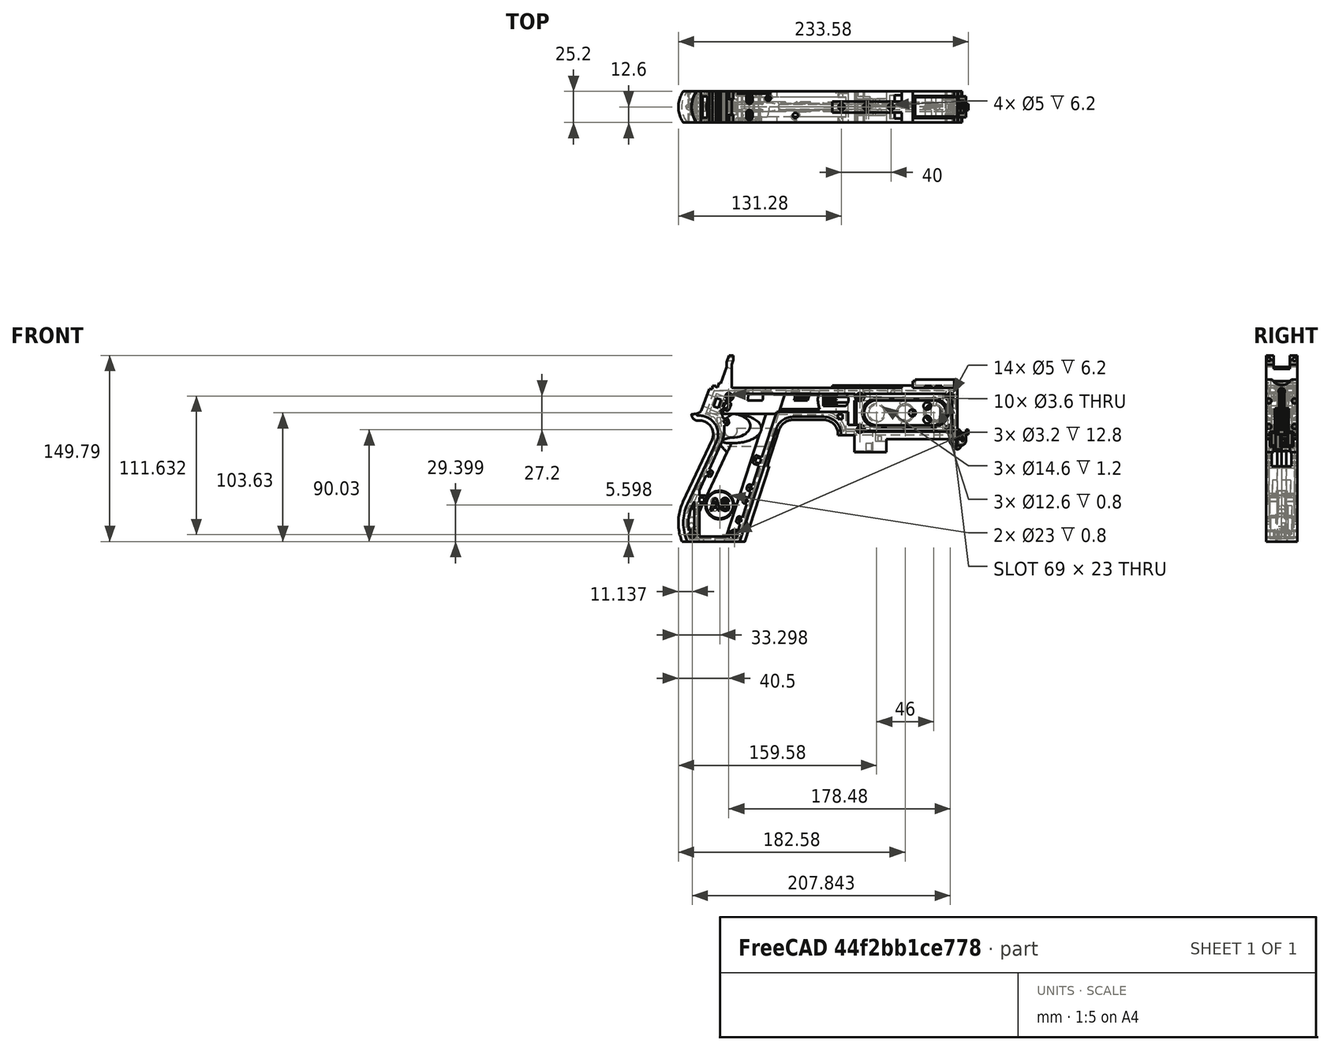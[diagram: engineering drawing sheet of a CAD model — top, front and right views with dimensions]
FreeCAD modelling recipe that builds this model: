
FCSTD DOCUMENT  (FreeCAD 1.0R39319 (Git))
Label: PICON-OF_ver_49
License: All rights reserved
LicenseURL: https://en.wikipedia.org/wiki/All_rights_reserved
objects: Sketcher::SketchObject×121, Part::Extrusion×62, Part::Cut×48, PartDesign::Pad×29, PartDesign::Pocket×20, PartDesign::Chamfer×15, PartDesign::Body×10, PartDesign::Fillet×6, Part::MultiFuse×4, Part::Part2DObjectPython×4, PartDesign::SubtractivePipe×4, PartDesign::SubtractiveLoft×4, PartDesign::Plane×2, PartDesign::SubShapeBinder×2, Part::Sweep×1, PartDesign::ShapeBinder×1, Mesh::Feature×1
note: 610 computed .brp shape members not serialized (recipe doc carries the construction recipe); baked Part::Feature solids carry a one-line shape summary decoded from their .brp

FEATURE [Sketcher::SketchObject] Sketch  label="corpo principale"
  ArcFitTolerance = 1e-06
  AttacherType = Attacher::AttachEngine3D
  AttachmentSupport = -> [XZ_Plane]
  FullyConstrained = true
  MakeInternals = false
  MapMode = 5
  Placement = pos=(0,0,0) rot=(1,0,0;1.5708rad)
  sketch-geometry (65):
    g0: LineSegment StartX=0 StartY=0 StartZ=0 EndX=-57.2 EndY=0 EndZ=0
    g1: LineSegment StartX=-57.2 StartY=0 StartZ=0 EndX=-57.2 EndY=-10.4 EndZ=0
    g2: LineSegment StartX=-57.2 StartY=-10.4 StartZ=0 EndX=-82.8 EndY=-10.4 EndZ=0
    g3: LineSegment StartX=-82.8 StartY=-10.4 StartZ=0 EndX=-82.8 EndY=3.2 EndZ=0
    g4: LineSegment StartX=-82.8 StartY=3.2 StartZ=0 EndX=-93.6 EndY=3.2 EndZ=0
    g5: LineSegment StartX=-93.6 StartY=3.2 StartZ=0 EndX=-93.6 EndY=4 EndZ=0
    g6: LineSegment StartX=-107.6 StartY=18 StartZ=0 EndX=-132.428 EndY=18 EndZ=0
    g7: LineSegment StartX=-145.743 StartY=8.32624 StartZ=0 EndX=-175.232 EndY=-82.4316 EndZ=0
    g8: LineSegment StartX=-175.232 StartY=-82.4316 StartZ=0 EndX=-217.232 EndY=-82.4316 EndZ=0
    g9: LineSegment StartX=-217.232 StartY=-52.1862 StartZ=0 EndX=-193.988 EndY=-2.33927 EndZ=0
    g10: LineSegment StartX=-206.196 StartY=23.0857 StartZ=0 EndX=-199.861 EndY=40.4914 EndZ=0
    g11: LineSegment StartX=-199.861 StartY=40.4914 StartZ=0 EndX=-197.061 EndY=40.4914 EndZ=0
    g12: LineSegment StartX=-197.061 StartY=40.4914 StartZ=0 EndX=-197.061 EndY=42.8914 EndZ=0
    g13: LineSegment StartX=-197.061 StartY=42.8914 StartZ=0 EndX=-194.261 EndY=42.8914 EndZ=0
    g14: LineSegment StartX=-194.261 StartY=42.8914 StartZ=0 EndX=-194.535 EndY=42.1397 EndZ=0
    g15: LineSegment StartX=-194.535 StartY=42.1397 StartZ=0 EndX=-193.031 EndY=41.5924 EndZ=0
    g16: LineSegment StartX=-193.031 StartY=41.5924 StartZ=0 EndX=-191.663 EndY=45.3512 EndZ=0
    g17: LineSegment StartX=-191.663 StartY=45.3512 StartZ=0 EndX=-190.536 EndY=44.9408 EndZ=0
    g18: LineSegment StartX=-190.536 StartY=44.9408 StartZ=0 EndX=-185.747 EndY=58.0965 EndZ=0
    g19: LineSegment StartX=-185.747 StartY=58.0965 StartZ=0 EndX=-185.747 EndY=62.0965 EndZ=0
    g20: LineSegment StartX=-185.747 StartY=62.0965 StartZ=0 EndX=-183.832 EndY=67.3588 EndZ=0
    g21: LineSegment StartX=-183.832 StartY=67.3588 StartZ=0 EndX=-180.232 EndY=67.3588 EndZ=0
    g22: LineSegment StartX=-180.232 StartY=67.3588 StartZ=0 EndX=-180.232 EndY=63.7588 EndZ=0
    g23: LineSegment StartX=-180.232 StartY=63.7588 StartZ=0 EndX=-181.6 EndY=60 EndZ=0
    g24: LineSegment StartX=-181.6 StartY=60 StartZ=0 EndX=-181.6 EndY=41.2 EndZ=0
    g25: LineSegment StartX=-181.6 StartY=41.2 StartZ=0 EndX=-100.8 EndY=41.2 EndZ=0
    g26: LineSegment StartX=-36 StartY=43.2 StartZ=0 EndX=-36 EndY=41.2 EndZ=0
    g27: LineSegment StartX=0 StartY=48 StartZ=0 EndX=0 EndY=0 EndZ=0
    g28: LineSegment StartX=-209.901 StartY=19.85 StartZ=0 EndX=-209.901 EndY=20.1 EndZ=0
    g29: LineSegment StartX=-208.001 StartY=22 StartZ=0 EndX=-207.747 EndY=22 EndZ=0
    g30: LineSegment StartX=-207.583 StartY=19 StartZ=0 EndX=-209.051 EndY=19 EndZ=0
    g31: ArcOfCircle CenterX=-208.001 CenterY=20.1 CenterZ=0 NormalX=0 NormalY=0 NormalZ=1 AngleXU=0 Radius=1.9 StartAngle=1.5708 EndAngle=3.14159
    g32: GeomPoint [constr] X=-209.901 Y=22 Z=0
    g33: ArcOfCircle CenterX=-209.051 CenterY=19.85 CenterZ=0 NormalX=0 NormalY=0 NormalZ=1 AngleXU=0 Radius=0.85 StartAngle=3.14159 EndAngle=4.71239
    g34: GeomPoint [constr] X=-209.901 Y=19 Z=0
    g35: ArcOfCircle CenterX=-207.747 CenterY=23.65 CenterZ=0 NormalX=0 NormalY=0 NormalZ=1 AngleXU=0 Radius=1.65 StartAngle=4.71239 EndAngle=5.93412
    g36: GeomPoint [constr] X=-206.591 Y=22 Z=0
    g37: LineSegment StartX=-4 StartY=6 StartZ=0 EndX=-4 EndY=36.4 EndZ=0
    g38: LineSegment StartX=-4 StartY=36.4 StartZ=0 EndX=-185.2 EndY=36.4 EndZ=0
    g39: LineSegment StartX=-185.2 StartY=36.4 StartZ=0 EndX=-190.441 EndY=22 EndZ=0
    g40: LineSegment StartX=-214.575 StartY=-78.4316 StartZ=0 EndX=-178.142 EndY=-78.4316 EndZ=0
    g41: LineSegment StartX=-178.142 StartY=-78.4316 StartZ=0 EndX=-145.51 EndY=22 EndZ=0
    g42: LineSegment StartX=-145.51 StartY=22 StartZ=0 EndX=-87.91 EndY=22 EndZ=0
    g43: LineSegment StartX=-87.91 StartY=22 StartZ=0 EndX=-87.91 EndY=11.6 EndZ=0
    g44: LineSegment StartX=-87.91 StartY=11.6 StartZ=0 EndX=-80.11 EndY=11.6 EndZ=0
    g45: LineSegment StartX=-80.11 StartY=11.6 StartZ=0 EndX=-80.11 EndY=6 EndZ=0
    g46: LineSegment StartX=-80.11 StartY=6 StartZ=0 EndX=-4 EndY=6 EndZ=0
    g47: LineSegment StartX=-190.363 StartY=-4.02975 StartZ=0 EndX=-213.607 EndY=-53.8767 EndZ=0
    g48: ArcOfCircle CenterX=-132.428 CenterY=4 CenterZ=0 NormalX=0 NormalY=0 NormalZ=1 AngleXU=0 Radius=14 StartAngle=1.5708 EndAngle=2.82743
    g49: GeomPoint [constr] X=-142.6 Y=18 Z=0
    g50: ArcOfCircle CenterX=-107.6 CenterY=4 CenterZ=0 NormalX=0 NormalY=0 NormalZ=1 AngleXU=0 Radius=14 StartAngle=0 EndAngle=1.5708
    g51: GeomPoint [constr] X=-93.6 Y=18 Z=0
    g52: ArcOfCircle CenterX=-184.801 CenterY=-67.3089 CenterZ=0 NormalX=0 NormalY=0 NormalZ=1 AngleXU=0 Radius=35.7833 StartAngle=2.70526 EndAngle=3.57792
    g53: ArcOfCircle CenterX=-207.583 CenterY=4 CenterZ=0 NormalX=0 NormalY=0 NormalZ=1 AngleXU=0 Radius=15 StartAngle=5.84685 EndAngle=7.85398
    g54: LineSegment [constr] StartX=-213.607 StartY=-53.8767 StartZ=0 EndX=-217.232 EndY=-52.1862 EndZ=0
    g55: ArcOfCircle CenterX=-184.801 CenterY=-67.3089 CenterZ=0 NormalX=0 NormalY=0 NormalZ=1 AngleXU=0 Radius=31.7833 StartAngle=2.70526 EndAngle=3.49911
    g56: ArcOfCircle CenterX=-218.095 CenterY=8.90192 CenterZ=0 NormalX=0 NormalY=0 NormalZ=1 AngleXU=0 Radius=30.5989 StartAngle=5.84685 EndAngle=6.72553
    g57: LineSegment StartX=-44.6 StartY=43.2 StartZ=0 EndX=-36 EndY=43.2 EndZ=0
    g58: LineSegment StartX=-100.8 StartY=41.2 StartZ=0 EndX=-44.6 EndY=41.2 EndZ=0
    g59: LineSegment StartX=-44.6 StartY=41.2 StartZ=0 EndX=-44.6 EndY=43.2 EndZ=0
    g60: LineSegment StartX=-2.4 StartY=48 StartZ=0 EndX=0 EndY=48 EndZ=0
    g61: LineSegment StartX=-36 StartY=41.2 StartZ=0 EndX=-2.4 EndY=41.2 EndZ=0
    g62: LineSegment StartX=-2.4 StartY=41.2 StartZ=0 EndX=-2.4 EndY=48 EndZ=0
    g63: LineSegment [constr] StartX=-181.6 StartY=36.4 StartZ=0 EndX=-152.209 EndY=36.4 EndZ=0
    g64: LineSegment [constr] StartX=-181.6 StartY=36.4 StartZ=0 EndX=-130.41 EndY=36.4 EndZ=0
  constraints (183):
    c: Coincident(g-1,g0)
    c: PointOnObject(g0,g-1)
    c: Coincident(g0,g1)
    c: Vertical(g1)
    c: Coincident(g1,g2)
    c: Horizontal(g2)
    c: Coincident(g2,g3)
    c: Vertical(g3)
    c: Coincident(g3,g4)
    c: Coincident(g4,g5)
    c: Vertical(g5)
    c: Horizontal(g6)
    c: Coincident(g7,g8)
    c: Horizontal(g8)
    c: Coincident(g10,g11)
    c: Horizontal(g11)
    c: Coincident(g11,g12)
    c: Vertical(g12)
    c: Coincident(g12,g13)
    c: Horizontal(g13)
    c: Coincident(g13,g14)
    c: Coincident(g14,g15)
    c: Coincident(g15,g16)
    c: Coincident(g16,g17)
    c: Coincident(g17,g18)
    c: Coincident(g18,g19)
    c: Vertical(g19)
    c: Coincident(g19,g20)
    c: Coincident(g20,g21)
    c: Horizontal(g21)
    c: Coincident(g21,g22)
    c: Vertical(g22)
    c: Coincident(g22,g23)
    c: Coincident(g23,g24)
    c: Vertical(g24)
    c: Coincident(g24,g25)
    c: Horizontal(g25)
    c: Coincident(g57,g26)
    c: Vertical(g26)
    c: Coincident(g26,g61)
    c: PointOnObject(g60,g-2)
    c: Coincident(g60,g27)
    c: Coincident(g27,g0)
    c: DistanceY(g27,g27) = 48
    c: DistanceY(g1,g1) = 10.4
    c: DistanceX(g0,g0) = 57.2
    c: DistanceX(g2,g2) = 25.6
    c: Horizontal(g4)
    c: DistanceY(g3,g3) = 13.6
    c: DistanceX(g4,g4) = 10.8
    c: DistanceY(g5,g51) = 14.8
    c: DistanceX(g49,g51) = 49
    c: Distance(g7,g49) = 105.6
    c: DistanceX(g61,g60) = 36
    c: DistanceX(g25,g25) = 80.8
    c: DistanceY(g24,g24) = 18.8
    c: DistanceY(g22,g22) = 3.6
    c: Distance(g23) = 4
    c: Angle(g-1,g23) = 1.22173
    c: DistanceX(g21,g21) = 3.6
    c: Distance(g20) = 5.6
    c: Angle(g-1,g20) = 1.22173
    c: DistanceY(g19,g19) = 4
    c: Distance(g18) = 14
    c: Angle(g-1,g18) = 1.22173
    c: Distance(g17) = 1.2
    c: Distance(g16) = 4
    c: Angle(g16) = 1.22173
    c: Perpendicular(g18,g17)
    c: Distance(g15) = 1.6
    c: Perpendicular(g16,g15)
    c: Distance(g14) = 0.8
    c: DistanceX(g13,g13) = 2.8
    c: Perpendicular(g15,g14)
    c: DistanceY(g12,g12) = 2.4
    c: DistanceX(g11,g11) = 2.8
    c: Distance(g9) = 55
    c: Angle(g9,g-1) = 2.00713
    c: Horizontal(g29)
    c: Vertical(g28)
    c: Horizontal(g30)
    c: PointOnObject(g32,g29)
    c: PointOnObject(g32,g28)
    c: Tangent(g29,g31) = 1.5708
    c: Tangent(g28,g31) = 1.5708
    c: PointOnObject(g34,g28)
    c: PointOnObject(g34,g30)
    c: Tangent(g28,g33) = 1.5708
    c: Tangent(g30,g33) = 1.5708
    c: PointOnObject(g36,g29)
    c: PointOnObject(g36,g10)
    c: Tangent(g29,g35) = -1.5708
    c: Tangent(g10,g35) = -1.5708
    c: Angle(g-1,g10) = 1.22173
    c: Radius(g35) = 1.65
    c: Vertical(g37)
    c: Coincident(g37,g38)
    c: Horizontal(g38)
    c: Coincident(g38,g39)
    c: Horizontal(g40)
    c: Coincident(g40,g41)
    c: Coincident(g41,g42)
    c: Horizontal(g42)
    c: Coincident(g42,g43)
    c: Vertical(g43)
    c: Coincident(g43,g44)
    c: Horizontal(g44)
    c: Coincident(g44,g45)
    c: Vertical(g45)
    c: Coincident(g45,g46)
    c: Coincident(g46,g37)
    c: Horizontal(g46)
    c: DistanceY(g0,g37) = 6
    c: DistanceX(g37,g0) = 4
    c: DistanceY(g37,g25) = 4.8
    c: DistanceX(g38,g38) = 181.2
    c: DistanceX(g42,g42) = 57.6
    c: DistanceY(g49,g41) = 4
    c: DistanceX(g41,g49) = 2.91
    c: DistanceY(g43,g43) = 10.4
    c: DistanceX(g44,g44) = 7.8
    c: DistanceY(g7,g40) = 4
    c: Distance(g47) = 55
    c: Angle(g-1,g39) = 1.22173
    c: PointOnObject(g49,g7)
    c: PointOnObject(g49,g6)
    c: Tangent(g7,g48) = -1.5708
    c: Tangent(g6,g48) = -1.5708
    c: PointOnObject(g51,g5)
    c: PointOnObject(g51,g6)
    c: Tangent(g5,g50) = -1.5708
    c: Tangent(g6,g50) = -1.5708
    c: Radius(g50) = 14
    c: Radius(g48) = 14
    c: DistanceX(g8,g8) = 42
    c: Angle(g7,g-1) = 1.88496
    c: Parallel(g41,g7)
    c: Parallel(g47,g9)
    c: Coincident(g52,g8)
    c: Tangent(g52,g9) = 1.5708
    c: DistanceX(g9,g8) = 0
    c: Tangent(g53,g9) = -1.5708
    c: Tangent(g53,g30) = -1.5708
    c: Diameter(g53) = 30
    c: DistanceY(g53,g0) = -4
    c: Coincident(g54,g47)
    c: Distance(g54) = 4
    c: Coincident(g54,g9)
    c: Coincident(g55,g40)
    c: Tangent(g55,g47) = -1.5708
    c: Coincident(g52,g55)
    c: Coincident(g56,g39)
    c: Tangent(g56,g47) = 1.5708
    c: Horizontal(g57)
    c: DistanceX(g57,g57) = 8.6
    c: Coincident(g58,g25)
    c: Horizontal(g58)
    c: Coincident(g59,g58)
    c: Vertical(g59)
    c: DistanceY(g58,g57) = 2
    c: DistanceX(g58,g58) = 56.2
    c: Coincident(g59,g57)
    c: DistanceY(g41,g36) = 0
    c: DistanceY(g36,g39) = 0
    c: DistanceY(g28,g28) = 0.25
    c: DistanceX(g30,g36) = 2.46
    c: DistanceX(g28,g29) = 1.9
    c: Coincident(g62,g60)
    c: Horizontal(g60)
    c: DistanceX(g62,g27) = 2.4
    c: Coincident(g61,g62)
    c: DistanceY(g26,g26) = 2
    c: Vertical(g62)
    c: DistanceY(g61,g60) = 6.8
    c: Horizontal(g61)
    c: Distance(g63) = 29.391
    c: PointOnObject(g63,g38)
    c: PointOnObject(g63,g38)
    c: Distance(g64) = 51.19
    c: PointOnObject(g64,g38)
    c: PointOnObject(g64,g38)
    c: DistanceX(g24,g63) = 0
    c: DistanceX(g24,g64) = 0
FEATURE [Part::Extrusion] Extrude  label="Extrude corpo principale"
  Base = -> Sketch
  Dir = (0,-1,2e-16)
  DirMode = 2
  FaceMakerClass = Part::FaceMakerBullseye
  FaceMakerMode = 3
  LengthFwd = 25.2
  LengthRev = 12.6
  Solid = true
  Symmetric = true
FEATURE [Sketcher::SketchObject] Sketch002  label="scavo grilletto"
  ArcFitTolerance = 1e-06
  AttachmentSupport = -> [XZ_Plane]
  ExternalGeometry = -> [Sketch]
  FullyConstrained = true
  MakeInternals = false
  MapMode = 5
  Placement = pos=(0,0,0) rot=(1,0,0;1.5708rad)
  sketch-geometry (4):
    g0: LineSegment StartX=-89.51 StartY=22 StartZ=0 EndX=-152.71 EndY=22 EndZ=0
    g1: LineSegment StartX=-152.71 StartY=22 StartZ=0 EndX=-167.006 EndY=-22 EndZ=0
    g2: LineSegment StartX=-167.006 StartY=-22 StartZ=0 EndX=-89.51 EndY=-22 EndZ=0
    g3: LineSegment StartX=-89.51 StartY=-22 StartZ=0 EndX=-89.51 EndY=22 EndZ=0
  constraints (12):
    c: Horizontal(g0)
    c: Coincident(g0,g1)
    c: Coincident(g1,g2)
    c: Horizontal(g2)
    c: Coincident(g2,g3)
    c: Coincident(g3,g0)
    c: Vertical(g3)
    c: Angle(g1,g0) = 1.88496
    c: DistanceY(g3,g3) = 44
    c: DistanceX(g0,g0) = 63.2
    c: DistanceX(g0,g-3) = 1.6
    c: DistanceY(g-3,g0) = 0
FEATURE [Sketcher::SketchObject] Sketch004  label="traiettoria arrotondamento impugnatura anteriore"
  ArcFitTolerance = 1e-06
  AttachmentSupport = -> [XZ_Plane]
  ExternalGeometry = -> [Sketch]
  FullyConstrained = true
  MakeInternals = false
  MapMode = 5
  Placement = pos=(0,0,0) rot=(1,0,0;1.5708rad)
  sketch-geometry (13):
    g0: LineSegment StartX=-175.232 StartY=-82.4316 StartZ=0 EndX=-145.743 EndY=8.32624 EndZ=0
    g1: LineSegment StartX=-93.6 StartY=3.2 StartZ=0 EndX=-93.6 EndY=4 EndZ=0
    g2: LineSegment StartX=-132.428 StartY=18 StartZ=0 EndX=-107.6 EndY=18 EndZ=0
    g3: ArcOfCircle CenterX=-132.428 CenterY=4 CenterZ=0 NormalX=0 NormalY=0 NormalZ=1 AngleXU=0 Radius=14 StartAngle=1.5708 EndAngle=2.82743
    g4: ArcOfCircle CenterX=-107.6 CenterY=4 CenterZ=0 NormalX=0 NormalY=0 NormalZ=1 AngleXU=0 Radius=14 StartAngle=0 EndAngle=1.5708
    g5: LineSegment StartX=-175.232 StartY=-82.4316 StartZ=0 EndX=-217.232 EndY=-82.4316 EndZ=0
    g6: LineSegment StartX=-217.232 StartY=-52.1862 StartZ=0 EndX=-193.988 EndY=-2.33927 EndZ=0
    g7: LineSegment StartX=-209.051 StartY=19 StartZ=0 EndX=-207.583 EndY=19 EndZ=0
    g8: LineSegment StartX=-209.901 StartY=20.1 StartZ=0 EndX=-209.901 EndY=19.85 EndZ=0
    g9: ArcOfCircle CenterX=-184.801 CenterY=-67.3089 CenterZ=0 NormalX=0 NormalY=0 NormalZ=1 AngleXU=0 Radius=35.7833 StartAngle=2.70526 EndAngle=3.57792
    g10: ArcOfCircle CenterX=-207.583 CenterY=4 CenterZ=0 NormalX=0 NormalY=0 NormalZ=1 AngleXU=0 Radius=15 StartAngle=5.84685 EndAngle=7.85398
    g11: ArcOfCircle CenterX=-209.051 CenterY=19.85 CenterZ=0 NormalX=0 NormalY=0 NormalZ=1 AngleXU=0 Radius=0.85 StartAngle=3.14159 EndAngle=4.71239
    g12: ArcOfCircle CenterX=-208.001 CenterY=20.1 CenterZ=0 NormalX=0 NormalY=0 NormalZ=1 AngleXU=0 Radius=1.9 StartAngle=1.5708 EndAngle=3.14159
  constraints (26):
    c: Coincident(g0,g-3)
    c: Coincident(g0,g-6)
    c: Coincident(g1,g-8)
    c: Coincident(g1,g-7)
    c: Coincident(g2,g-5)
    c: Coincident(g2,g-4)
    c: Coincident(g3,g2)
    c: Tangent(g3,g0) = 1.5708
    c: Coincident(g4,g1)
    c: Tangent(g4,g2) = 1.5708
    c: Coincident(g5,g0)
    c: Coincident(g5,g-9)
    c: Coincident(g6,g-12)
    c: Coincident(g6,g-11)
    c: Coincident(g7,g-15)
    c: Coincident(g7,g-14)
    c: Coincident(g8,g-16)
    c: Coincident(g8,g-17)
    c: Tangent(g9,g6) = 1.5708
    c: Coincident(g9,g5)
    c: Coincident(g10,g7)
    c: Tangent(g10,g6) = -1.5708
    c: Tangent(g11,g7) = -1.5708
    c: Coincident(g11,g8)
    c: Tangent(g12,g8) = -1.5708
    c: Coincident(g12,g-17)
FEATURE [PartDesign::Plane] DatumPlane  label="Piano per disegno arrotondamento impugnatura"
  AttachmentSupport = -> [Sketch]
  Length = 73.6581
  MapMode = 7
  Placement = pos=(-145.743,1.8e-15,8.32624) rot=(0.154555,0.154555,0.97582;1.59527rad)
  ResizeMode = 0
  Width = 303.511
FEATURE [Sketcher::SketchObject] Sketch005  label="forma arrotondamento impugnatura anteriore"
  ArcFitTolerance = 1e-06
  AttachmentSupport = -> [DatumPlane]
  FullyConstrained = true
  MakeInternals = false
  MapMode = 5
  Placement = pos=(-145.743,1.8e-15,8.32624) rot=(0.154555,0.154555,0.97582;1.59527rad)
  sketch-geometry (5):
    g0: GeomPoint [constr] X=0 Y=-4 Z=0
    g1: GeomPoint [constr] X=-12.6 Y=7.1e-15 Z=0
    g2: GeomPoint [constr] X=12.6 Y=4.97e-14 Z=0
    g3: LineSegment StartX=-12.6 StartY=7.1e-15 StartZ=0 EndX=12.6 EndY=4.97e-14 EndZ=0
    g4: ArcOfCircle CenterX=-3.88e-14 CenterY=17.845 CenterZ=0 NormalX=0 NormalY=0 NormalZ=1 AngleXU=0 Radius=21.845 StartAngle=4.09759 EndAngle=5.32718
  constraints (11):
    c: DistanceY(g0,g-1) = 4
    c: DistanceX(g-1,g0) = 0
    c: DistanceX(g1,g-1) = 12.6
    c: DistanceX(g-1,g2) = 12.6
    c: DistanceY(g-1,g2) = 0
    c: DistanceY(g-1,g1) = 0
    c: Coincident(g3,g1)
    c: Coincident(g3,g2)
    c: Coincident(g4,g1)
    c: Coincident(g4,g2)
    c: PointOnObject(g0,g4)
FEATURE [Part::Sweep] Sweep  label="Sweep impugnatura"
  Frenet = true
  Sections = -> [Sketch005]
  Solid = true
  Spine = -> Sketch [Edge32,Edge33,Edge34,Edge35,Edge36,Edge37,Edge38,Edge39,Edge40,Edge41,Edge42,Edge43,Edge44]
  Transition = 1
FEATURE [Sketcher::SketchObject] Sketch008  label="buchi e pulizie varie"
  ArcFitTolerance = 1e-06
  AttachmentSupport = -> [XZ_Plane]
  ExternalGeometry = -> [Sketch]
  FullyConstrained = true
  MakeInternals = false
  MapMode = 5
  Placement = pos=(0,0,0) rot=(1,0,0;1.5708rad)
  sketch-geometry (26):
    g0: LineSegment StartX=-96.278 StartY=20.155 StartZ=0 EndX=-92.278 EndY=20.155 EndZ=0
    g1: LineSegment StartX=-92.278 StartY=20.155 StartZ=0 EndX=-92.278 EndY=16.155 EndZ=0
    g2: LineSegment StartX=-92.278 StartY=16.155 StartZ=0 EndX=-96.278 EndY=16.155 EndZ=0
    g3: LineSegment StartX=-96.278 StartY=16.155 StartZ=0 EndX=-96.278 EndY=20.155 EndZ=0
    g4: LineSegment StartX=-222.232 StartY=-82.4316 StartZ=0 EndX=-170.232 EndY=-82.4316 EndZ=0
    g5: LineSegment StartX=-170.232 StartY=-82.4316 StartZ=0 EndX=-170.232 EndY=-86.4316 EndZ=0
    g6: LineSegment StartX=-170.232 StartY=-86.4316 StartZ=0 EndX=-222.232 EndY=-86.4316 EndZ=0
    g7: LineSegment StartX=-222.232 StartY=-86.4316 StartZ=0 EndX=-222.232 EndY=-82.4316 EndZ=0
    g8: LineSegment StartX=-213.901 StartY=20.1 StartZ=0 EndX=-213.901 EndY=26 EndZ=0
    g9: LineSegment StartX=-213.901 StartY=26 StartZ=0 EndX=-206.196 EndY=26 EndZ=0
    g10: LineSegment StartX=-17.4 StartY=42.8 StartZ=0 EndX=-12.4 EndY=42.8 EndZ=0
    g11: LineSegment StartX=-12.4 StartY=42.8 StartZ=0 EndX=-12.4 EndY=41.2 EndZ=0
    g12: LineSegment StartX=-12.4 StartY=41.2 StartZ=0 EndX=-17.4 EndY=41.2 EndZ=0
    g13: LineSegment StartX=-17.4 StartY=41.2 StartZ=0 EndX=-17.4 EndY=42.8 EndZ=0
    g14: LineSegment StartX=-25.9 StartY=42.8 StartZ=0 EndX=-20.9 EndY=42.8 EndZ=0
    g15: LineSegment StartX=-20.9 StartY=42.8 StartZ=0 EndX=-20.9 EndY=41.2 EndZ=0
    g16: LineSegment StartX=-20.9 StartY=41.2 StartZ=0 EndX=-25.9 EndY=41.2 EndZ=0
    g17: LineSegment StartX=-25.9 StartY=41.2 StartZ=0 EndX=-25.9 EndY=42.8 EndZ=0
    g18: GeomPoint [constr] X=-206.196 Y=23.0857 Z=0
    g19: GeomPoint [constr] X=-213.901 Y=20.1 Z=0
    g20: BSplineCurve PolesCount=4 KnotsCount=2 Degree=3 IsPeriodic=0
    g21-g24: Circle [constr] x4 (B-spline internal-alignment scaffolding for g20; pole/knot coordinates omitted)
    g25: LineSegment StartX=-206.196 StartY=26 StartZ=0 EndX=-206.196 EndY=23.0857 EndZ=0
  constraints (73):
    c: Horizontal(g0)
    c: Coincident(g1,g0)
    c: Vertical(g1)
    c: Coincident(g2,g1)
    c: Horizontal(g2)
    c: Coincident(g3,g2)
    c: Coincident(g3,g0)
    c: Vertical(g3)
    c: DistanceX(g0,g-4) = 4.368
    c: DistanceY(g0,g-4) = 1.845
    c: DistanceY(g1,g1) = 4
    c: DistanceX(g2,g2) = 4
    c: Horizontal(g4)
    c: Coincident(g5,g4)
    c: Vertical(g5)
    c: Coincident(g6,g5)
    c: Horizontal(g6)
    c: Coincident(g7,g6)
    c: Coincident(g7,g4)
    c: Vertical(g7)
    c: DistanceY(g7,g7) = 4
    c: DistanceX(g4,g-5) = 5
    c: DistanceX(g-5,g4) = 5
    c: DistanceY(g4,g-5) = 0
    c: Coincident(g9,g8)
    c: Parallel(g9,g-6)
    c: DistanceX(g8,g-8) = 4
    c: Horizontal(g10)
    c: Coincident(g11,g10)
    c: Vertical(g11)
    c: Coincident(g12,g11)
    c: Horizontal(g12)
    c: Coincident(g13,g12)
    c: Coincident(g13,g10)
    c: Vertical(g13)
    c: Horizontal(g14)
    c: Coincident(g15,g14)
    c: Vertical(g15)
    c: Coincident(g16,g15)
    c: Horizontal(g16)
    c: Coincident(g17,g16)
    c: Coincident(g17,g14)
    c: Vertical(g17)
    c: DistanceY(g11,g10) = 1.6
    c: DistanceX(g10,g10) = 5
    c: DistanceY(g15,g14) = 1.6
    c: DistanceX(g14,g14) = 5
    c: DistanceX(g15,g12) = 3.5
    c: DistanceX(g11,g-9) = 10
    c: DistanceY(g-9,g11) = 0
    c: DistanceY(g-9,g15) = 0
    c: Perpendicular(g8,g9)
    c: DistanceY(g-7,g9) = 4
    c: DistanceY(g8,g-8) = 0
    c: InternalAlignment(g18,g20)
    c: InternalAlignment(g19,g20)
    c: InternalAlignment(g21,g20)
    c: Weight(g21) = 1
    c: InternalAlignment(g22,g20)
    c: Equal(g22,g21)
    c: InternalAlignment(g23,g20)
    c: Equal(g23,g21)
    c: InternalAlignment(g24,g20)
    c: Equal(g24,g21)
    c: Coincident(g18,g-12)
    c: Coincident(g19,g8)
    c: Coincident(g25,g9)
    c: Coincident(g25,g20)
    c: Vertical(g25)
    c: DistanceY(g20,g23) = 0
    c: DistanceY(g22,g18) = 2.26
    c: DistanceX(g22,g18) = 0.93
    c: DistanceX(g20,g23) = 2.9
FEATURE [Part::Extrusion] Extrude004  label="Extrude Buchi e pulizie varie"
  Base = -> Sketch008
  Dir = (0,-1,2e-16)
  DirMode = 2
  FaceMakerClass = Part::FaceMakerBullseye
  FaceMakerMode = 3
  LengthFwd = 25.2
  LengthRev = 0
  Solid = true
  Symmetric = true
FEATURE [Sketcher::SketchObject] Sketch009  label="rinforzi"
  ArcFitTolerance = 1e-06
  AttachmentSupport = -> [XZ_Plane]
  ExternalGeometry = -> [Sketch]
  FullyConstrained = true
  MakeInternals = false
  MapMode = 5
  Placement = pos=(0,0,0) rot=(1,0,0;1.5708rad)
  sketch-geometry (9):
    g0: LineSegment StartX=-87.91 StartY=22 StartZ=0 EndX=-87.91 EndY=36.4 EndZ=0
    g1: LineSegment StartX=-87.91 StartY=36.4 StartZ=0 EndX=-97.91 EndY=36.4 EndZ=0
    g2: LineSegment StartX=-97.91 StartY=36.4 StartZ=0 EndX=-97.91 EndY=22 EndZ=0
    g3: LineSegment StartX=-97.91 StartY=22 StartZ=0 EndX=-87.91 EndY=22 EndZ=0
    g4: LineSegment StartX=-149.713 StartY=9.06563 StartZ=0 EndX=-154.586 EndY=-5.93437 EndZ=0
    g5: LineSegment StartX=-154.586 StartY=-5.93437 StartZ=0 EndX=-191.863 EndY=-5.93437 EndZ=0
    g6: LineSegment StartX=-191.863 StartY=-5.93437 StartZ=0 EndX=-191.863 EndY=9.06563 EndZ=0
    g7: LineSegment StartX=-191.863 StartY=9.06563 StartZ=0 EndX=-149.713 EndY=9.06563 EndZ=0
    g8: LineSegment [constr] StartX=-145.51 StartY=22 StartZ=0 EndX=-149.713 EndY=9.06563 EndZ=0
  constraints (25):
    c: Vertical(g0)
    c: Coincident(g1,g0)
    c: Horizontal(g1)
    c: Coincident(g2,g1)
    c: Vertical(g2)
    c: Coincident(g3,g2)
    c: Coincident(g3,g0)
    c: Horizontal(g3)
    c: Coincident(g0,g-4)
    c: DistanceX(g3,g3) = 10
    c: DistanceY(g0,g-3) = 0
    c: Coincident(g5,g4)
    c: Horizontal(g5)
    c: Coincident(g6,g5)
    c: Vertical(g6)
    c: Coincident(g7,g6)
    c: Coincident(g7,g4)
    c: Horizontal(g7)
    c: Distance(g8) = 13.6
    c: Parallel(g-6,g8)
    c: Coincident(g-6,g8)
    c: Parallel(g4,g-6)
    c: DistanceY(g4,g4) = 15
    c: Coincident(g4,g8)
    c: DistanceX(g-5,g5) = -1.5
FEATURE [Part::Extrusion] Extrude001  label="Extrude scavo grilletto"
  Base = -> Sketch002
  Dir = (0,-1,2e-16)
  DirMode = 2
  FaceMakerClass = Part::FaceMakerBullseye
  FaceMakerMode = 3
  LengthFwd = 16
  LengthRev = 0
  Solid = true
  Symmetric = true
FEATURE [Part::Extrusion] Extrude005  label="Extrude Rinforzi"
  Base = -> Sketch009
  Dir = (0,-1,2e-16)
  DirMode = 2
  FaceMakerClass = Part::FaceMakerBullseye
  FaceMakerMode = 3
  LengthFwd = 2
  LengthRev = 0
  Placement = pos=(0,12.6,0) rot=(0,0,1;0rad)
  Solid = true
  Symmetric = false
FEATURE [PartDesign::ShapeBinder] CopyCut
  TraceSupport = false
FEATURE [PartDesign::Plane] DatumPlane001
  AttachmentSupport = -> [CopyCut]
  Length = 283.944
  MapMode = 5
  Placement = pos=(0,12.6,0) rot=(0,0.707107,0.707107;3.14159rad)
  ResizeMode = 0
  Width = 188.15
FEATURE [Sketcher::SketchObject] Sketch010  label="buco neopixel"
  ArcFitTolerance = 1e-06
  AttachmentSupport = -> [XZ_Plane]
  ExternalGeometry = -> [Sketch]
  FullyConstrained = true
  MakeInternals = false
  MapMode = 5
  Placement = pos=(0,0,0) rot=(1,0,0;1.5708rad)
  sketch-geometry (5):
    g0: LineSegment [constr] StartX=-199.861 StartY=40.4914 StartZ=0 EndX=-201.368 EndY=36.3521 EndZ=0
    g1: LineSegment StartX=-201.368 StartY=36.3521 StartZ=0 EndX=-204.932 EndY=26.5605 EndZ=0
    g2: LineSegment StartX=-201.368 StartY=36.3521 StartZ=0 EndX=-180.2 EndY=28.6477 EndZ=0
    g3: LineSegment StartX=-180.2 StartY=28.6477 StartZ=0 EndX=-183.764 EndY=18.8561 EndZ=0
    g4: LineSegment StartX=-183.764 StartY=18.8561 StartZ=0 EndX=-204.932 EndY=26.5605 EndZ=0
  constraints (14):
    c: Parallel(g0,g-3)
    c: Distance(g0) = 4.405
    c: Coincident(g0,g-3)
    c: Coincident(g2,g1)
    c: Coincident(g3,g2)
    c: Coincident(g4,g3)
    c: Coincident(g4,g1)
    c: Parallel(g1,g-3)
    c: Distance(g1) = 10.42
    c: Coincident(g1,g0)
    c: Parallel(g2,g4)
    c: Perpendicular(g1,g2)
    c: DistanceX(g-4,g2) = 5
    c: Parallel(g3,g1)
FEATURE [Part::Extrusion] Extrude006  label="Extrude buco neopixel"
  Base = -> Sketch010
  Dir = (0,-1,2e-16)
  DirMode = 2
  FaceMakerClass = Part::FaceMakerBullseye
  FaceMakerMode = 3
  LengthFwd = 17.2
  LengthRev = 0
  Solid = true
  Symmetric = true
FEATURE [Sketcher::SketchObject] Sketch011  label="fermo grilletto"
  ArcFitTolerance = 1e-06
  AttachmentSupport = -> [XZ_Plane]
  ExternalGeometry = -> [Sketch]
  FullyConstrained = true
  MakeInternals = false
  MapMode = 5
  Placement = pos=(0,0,0) rot=(1,0,0;1.5708rad)
  sketch-geometry (18):
    g0: LineSegment [constr] StartX=-145.51 StartY=22 StartZ=0 EndX=-157.347 EndY=-14.4293 EndZ=0
    g1: LineSegment [constr] StartX=-157.347 StartY=-14.4293 StartZ=0 EndX=-157.841 EndY=-15.951 EndZ=0
    g2: LineSegment StartX=-161.151 StartY=-13.1932 StartZ=0 EndX=-155.825 EndY=-14.9237 EndZ=0
    g3: LineSegment StartX=-163.167 StartY=-14.2205 StartZ=0 EndX=-164.403 EndY=-18.0247 EndZ=0
    g4: LineSegment StartX=-163.376 StartY=-20.0408 StartZ=0 EndX=-158.05 EndY=-21.7713 EndZ=0
    g5: LineSegment StartX=-158.05 StartY=-21.7713 StartZ=0 EndX=-155.825 EndY=-14.9237 EndZ=0
    g6: LineSegment StartX=-161.645 StartY=-14.7149 StartZ=0 EndX=-157.841 EndY=-15.951 EndZ=0
    g7: LineSegment StartX=-157.841 StartY=-15.951 StartZ=0 EndX=-159.077 EndY=-19.7552 EndZ=0
    g8: LineSegment StartX=-159.077 StartY=-19.7552 StartZ=0 EndX=-162.881 EndY=-18.5191 EndZ=0
    g9: LineSegment StartX=-162.881 StartY=-18.5191 StartZ=0 EndX=-161.645 EndY=-14.7149 EndZ=0
    g10: LineSegment [constr] StartX=-161.645 StartY=-14.7149 StartZ=0 EndX=-161.151 EndY=-13.1932 EndZ=0
    g11: LineSegment [constr] StartX=-159.077 StartY=-19.7552 StartZ=0 EndX=-157.555 EndY=-20.2496 EndZ=0
    g12: LineSegment [constr] StartX=-159.077 StartY=-19.7552 StartZ=0 EndX=-159.572 EndY=-21.2769 EndZ=0
    g13: LineSegment [constr] StartX=-161.645 StartY=-14.7149 StartZ=0 EndX=-163.167 EndY=-14.2205 EndZ=0
    g14: ArcOfCircle CenterX=-161.645 CenterY=-14.7149 CenterZ=0 NormalX=0 NormalY=0 NormalZ=1 AngleXU=0 Radius=1.6 StartAngle=1.25664 EndAngle=2.82743
    g15: GeomPoint [constr] X=-162.673 Y=-12.6988 Z=0
    g16: ArcOfCircle CenterX=-162.881 CenterY=-18.5191 CenterZ=0 NormalX=0 NormalY=0 NormalZ=1 AngleXU=0 Radius=1.6 StartAngle=2.82743 EndAngle=4.39823
    g17: GeomPoint [constr] X=-164.897 Y=-19.5464 Z=0
  constraints (48):
    c: Parallel(g0,g-3)
    c: Distance(g0) = 38.304
    c: Coincident(g0,g-3)
    c: Parallel(g1,g-3)
    c: Distance(g1) = 1.6
    c: Coincident(g1,g0)
    c: Coincident(g5,g4)
    c: Coincident(g5,g2)
    c: Coincident(g7,g6)
    c: Coincident(g8,g7)
    c: Coincident(g9,g8)
    c: Coincident(g9,g6)
    c: Parallel(g7,g-3)
    c: Parallel(g9,g7)
    c: Perpendicular(g6,g7)
    c: Parallel(g6,g8)
    c: Distance(g6) = 4
    c: Distance(g9) = 4
    c: Parallel(g5,g7)
    c: Parallel(g9,g3)
    c: Parallel(g2,g6)
    c: Parallel(g4,g8)
    c: Parallel(g13,g6)
    c: Parallel(g10,g9)
    c: Parallel(g11,g8)
    c: Parallel(g12,g7)
    c: Distance(g10) = 1.6
    c: Distance(g13) = 1.6
    c: Distance(g12) = 1.6
    c: Distance(g11) = 1.6
    c: Coincident(g10,g6)
    c: Coincident(g13,g6)
    c: Coincident(g12,g7)
    c: Coincident(g11,g7)
    c: Distance(g10,g15) = 1.6
    c: Distance(g15,g13) = 1.6
    c: Distance(g4,g12) = 1.6
    c: Distance(g4,g11) = 1.6
    c: PointOnObject(g15,g2)
    c: Tangent(g3,g14) = -1.5708
    c: Tangent(g2,g14) = 1.5708
    c: PointOnObject(g17,g4)
    c: PointOnObject(g17,g3)
    c: Tangent(g4,g16) = -1.5708
    c: Tangent(g3,g16) = -1.5708
    c: Equal(g16,g14)
    c: Coincident(g16,g8)
    c: Coincident(g6,g1)
FEATURE [Part::Extrusion] Extrude007  label="Extrude fermo grilletto"
  Base = -> Sketch011
  Dir = (0,-1,2e-16)
  DirMode = 2
  FaceMakerClass = Part::FaceMakerBullseye
  FaceMakerMode = 3
  LengthFwd = 25.2
  LengthRev = 0
  Solid = true
  Symmetric = true
FEATURE [Sketcher::SketchObject] Sketch012  label="buco oled"
  ArcFitTolerance = 1e-06
  AttachmentSupport = -> [XZ_Plane]
  ExternalGeometry = -> [Sketch]
  FullyConstrained = true
  MakeInternals = false
  MapMode = 5
  Placement = pos=(0,0,0) rot=(1,0,0;1.5708rad)
  sketch-geometry (4):
    g0: LineSegment StartX=-185.747 StartY=58.0965 StartZ=0 EndX=-180.232 EndY=56.0891 EndZ=0
    g1: LineSegment StartX=-185.747 StartY=58.0965 StartZ=0 EndX=-185.747 EndY=67.3588 EndZ=0
    g2: LineSegment StartX=-185.747 StartY=67.3588 StartZ=0 EndX=-180.232 EndY=67.3588 EndZ=0
    g3: LineSegment StartX=-180.232 StartY=67.3588 StartZ=0 EndX=-180.232 EndY=56.0891 EndZ=0
  constraints (10):
    c: Coincident(g1,g0)
    c: Coincident(g2,g1)
    c: Coincident(g3,g2)
    c: Coincident(g3,g0)
    c: Parallel(g1,g-5)
    c: Perpendicular(g-3,g0)
    c: Parallel(g2,g-6)
    c: Parallel(g3,g-4)
    c: Coincident(g0,g-5)
    c: Coincident(g2,g-6)
FEATURE [Part::Extrusion] Extrude008  label="Extrude buco oled"
  Base = -> Sketch012
  Dir = (0,-1,2e-16)
  DirMode = 2
  FaceMakerClass = Part::FaceMakerBullseye
  FaceMakerMode = 3
  LengthFwd = 12.8
  LengthRev = 0
  Solid = true
  Symmetric = true
FEATURE [Sketcher::SketchObject] Sketch013  label="buco pompa"
  ArcFitTolerance = 1e-06
  AttachmentSupport = -> [XZ_Plane]
  ExternalGeometry = -> [Sketch]
  FullyConstrained = true
  MakeInternals = false
  MapMode = 5
  Placement = pos=(0,0,0) rot=(1,0,0;1.5708rad)
  sketch-geometry (8):
    g0: LineSegment StartX=-82.8 StartY=-10.4 StartZ=0 EndX=-82.8 EndY=-9.6 EndZ=0
    g1: LineSegment StartX=-82.8 StartY=-9.6 StartZ=0 EndX=-67.9 EndY=-9.6 EndZ=0
    g2: LineSegment StartX=-67.9 StartY=-9.6 StartZ=0 EndX=-67.9 EndY=6 EndZ=0
    g3: LineSegment StartX=-67.9 StartY=6 StartZ=0 EndX=-65.9 EndY=6 EndZ=0
    g4: LineSegment StartX=-65.9 StartY=6 StartZ=0 EndX=-65.9 EndY=-1.7 EndZ=0
    g5: LineSegment StartX=-65.9 StartY=-1.7 StartZ=0 EndX=-57.2 EndY=-1.7 EndZ=0
    g6: LineSegment StartX=-57.2 StartY=-1.7 StartZ=0 EndX=-57.2 EndY=-10.4 EndZ=0
    g7: LineSegment StartX=-57.2 StartY=-10.4 StartZ=0 EndX=-82.8 EndY=-10.4 EndZ=0
  constraints (22):
    c: Vertical(g0)
    c: Coincident(g1,g0)
    c: Horizontal(g1)
    c: Coincident(g2,g1)
    c: Vertical(g2)
    c: Coincident(g3,g2)
    c: Horizontal(g3)
    c: Coincident(g4,g3)
    c: Vertical(g4)
    c: Coincident(g5,g4)
    c: Horizontal(g5)
    c: Coincident(g6,g5)
    c: Vertical(g6)
    c: Coincident(g7,g6)
    c: Coincident(g7,g0)
    c: DistanceY(g0,g0) = 0.8
    c: DistanceY(g6,g6) = 8.7
    c: DistanceX(g1,g1) = 14.9
    c: DistanceX(g3,g3) = 2
    c: Coincident(g0,g-4)
    c: DistanceY(g2,g-6) = 0
    c: Coincident(g6,g-5)
FEATURE [Part::Extrusion] Extrude009  label="Extrude buco pompa"
  Base = -> Sketch013
  Dir = (0,-1,2e-16)
  DirMode = 2
  FaceMakerClass = Part::FaceMakerBullseye
  FaceMakerMode = 3
  LengthFwd = 13.2
  LengthRev = 0
  Solid = true
  Symmetric = true
FEATURE [Sketcher::SketchObject] Sketch014  label="buco frontale"
  ArcFitTolerance = 1e-06
  AttachmentSupport = -> [XZ_Plane]
  ExternalGeometry = -> [Sketch]
  FullyConstrained = true
  MakeInternals = false
  MapMode = 5
  Placement = pos=(0,0,0) rot=(1,0,0;1.5708rad)
  sketch-geometry (10):
    g0: LineSegment StartX=0 StartY=0 StartZ=0 EndX=0 EndY=24.671 EndZ=0
    g1: LineSegment StartX=0 StartY=24.671 StartZ=0 EndX=-4 EndY=24.671 EndZ=0
    g2: LineSegment StartX=-4 StartY=24.671 StartZ=0 EndX=-4 EndY=16 EndZ=0
    g3: LineSegment StartX=-4 StartY=16 StartZ=0 EndX=-2.4 EndY=16 EndZ=0
    g4: LineSegment StartX=-2.4 StartY=16 StartZ=0 EndX=-2.4 EndY=10 EndZ=0
    g5: LineSegment StartX=-2.4 StartY=10 StartZ=0 EndX=-12 EndY=10 EndZ=0
    g6: LineSegment StartX=-12 StartY=10 StartZ=0 EndX=-12 EndY=6 EndZ=0
    g7: LineSegment StartX=-12 StartY=6 StartZ=0 EndX=-2.4 EndY=6 EndZ=0
    g8: LineSegment StartX=-2.4 StartY=6 StartZ=0 EndX=-2.4 EndY=0 EndZ=0
    g9: LineSegment StartX=-2.4 StartY=0 StartZ=0 EndX=0 EndY=0 EndZ=0
  constraints (29):
    c: Vertical(g0)
    c: Coincident(g1,g0)
    c: Horizontal(g1)
    c: Coincident(g2,g1)
    c: Vertical(g2)
    c: Coincident(g3,g2)
    c: Horizontal(g3)
    c: Coincident(g4,g3)
    c: Vertical(g4)
    c: Coincident(g5,g4)
    c: Horizontal(g5)
    c: Coincident(g6,g5)
    c: Vertical(g6)
    c: Coincident(g7,g6)
    c: Coincident(g8,g7)
    c: Vertical(g8)
    c: Coincident(g9,g8)
    c: Coincident(g9,g0)
    c: Horizontal(g9)
    c: DistanceY(g0,g0) = 24.671
    c: Horizontal(g7)
    c: DistanceY(g6,g6) = 4
    c: DistanceY(g4,g4) = 6
    c: DistanceX(g9,g9) = 2.4
    c: Coincident(g0,g-1)
    c: DistanceY(g-3,g7) = 0
    c: DistanceX(g8,g4) = 0
    c: DistanceX(g-3,g1) = 0
    c: DistanceX(g6,g-3) = 8
FEATURE [Part::Extrusion] Extrude010  label="Extrude buco frontale"
  Base = -> Sketch014
  Dir = (0,-1,2e-16)
  DirMode = 2
  FaceMakerClass = Part::FaceMakerBullseye
  FaceMakerMode = 3
  LengthFwd = 11.2
  LengthRev = 0
  Solid = true
  Symmetric = true
FEATURE [Sketcher::SketchObject] Sketch015  label="guida rail"
  ArcFitTolerance = 1e-06
  AttachmentSupport = -> [XZ_Plane]
  ExternalGeometry = -> [Sketch]
  FullyConstrained = true
  MakeInternals = false
  MapMode = 5
  Placement = pos=(0,0,0) rot=(1,0,0;1.5708rad)
  sketch-geometry (4):
    g0: LineSegment StartX=-100.8 StartY=43.2 StartZ=0 EndX=-44.6 EndY=43.2 EndZ=0
    g1: LineSegment StartX=-44.6 StartY=43.2 StartZ=0 EndX=-44.6 EndY=41.2 EndZ=0
    g2: LineSegment StartX=-44.6 StartY=41.2 StartZ=0 EndX=-100.8 EndY=41.2 EndZ=0
    g3: LineSegment StartX=-100.8 StartY=41.2 StartZ=0 EndX=-100.8 EndY=43.2 EndZ=0
  constraints (9):
    c: Horizontal(g0)
    c: Coincident(g1,g0)
    c: Coincident(g2,g1)
    c: Coincident(g3,g2)
    c: Coincident(g3,g0)
    c: Vertical(g3)
    c: Coincident(g2,g-3)
    c: Coincident(g1,g-3)
    c: Coincident(g0,g-4)
FEATURE [Part::Extrusion] Extrude011  label="Extrude guida rail"
  Base = -> Sketch015
  Dir = (0,-1,2e-16)
  DirMode = 2
  FaceMakerClass = Part::FaceMakerBullseye
  FaceMakerMode = 3
  LengthFwd = 9
  LengthRev = 0
  Solid = true
  Symmetric = true
FEATURE [Sketcher::SketchObject] Sketch016  label="guide per coperture laterali"
  ArcFitTolerance = 1e-06
  AttachmentSupport = -> [XZ_Plane]
  ExternalGeometry = -> [Sketch]
  FullyConstrained = true
  MakeInternals = false
  MapMode = 5
  Placement = pos=(0,0,0) rot=(1,0,0;1.5708rad)
  sketch-geometry (14):
    g0: Circle CenterX=-5.6 CenterY=7.6 CenterZ=0 NormalX=0 NormalY=0 NormalZ=1 AngleXU=0 Radius=1.6
    g1: Circle CenterX=-5.6 CenterY=7.6 CenterZ=0 NormalX=0 NormalY=0 NormalZ=1 AngleXU=0 Radius=4
    g2: Circle CenterX=-5.6 CenterY=34.8 CenterZ=0 NormalX=0 NormalY=0 NormalZ=1 AngleXU=0 Radius=1.6
    g3: Circle CenterX=-5.6 CenterY=34.8 CenterZ=0 NormalX=0 NormalY=0 NormalZ=1 AngleXU=0 Radius=4
    g4: Circle CenterX=-184.08 CenterY=34.8 CenterZ=0 NormalX=0 NormalY=0 NormalZ=1 AngleXU=0 Radius=1.6
    g5: Circle CenterX=-184.08 CenterY=34.8 CenterZ=0 NormalX=0 NormalY=0 NormalZ=1 AngleXU=0 Radius=4
    g6: Circle CenterX=-179.305 CenterY=-76.8316 CenterZ=0 NormalX=0 NormalY=0 NormalZ=1 AngleXU=0 Radius=1.6
    g7: Circle CenterX=-179.305 CenterY=-76.8316 CenterZ=0 NormalX=0 NormalY=0 NormalZ=1 AngleXU=0 Radius=4
    g8: Circle CenterX=-213.443 CenterY=-76.8316 CenterZ=0 NormalX=0 NormalY=0 NormalZ=1 AngleXU=0 Radius=1.6
    g9: Circle CenterX=-213.443 CenterY=-76.8316 CenterZ=0 NormalX=0 NormalY=0 NormalZ=1 AngleXU=0 Radius=4
    g10: Circle CenterX=-78.51 CenterY=7.6 CenterZ=0 NormalX=0 NormalY=0 NormalZ=1 AngleXU=0 Radius=1.6
    g11: Circle CenterX=-78.51 CenterY=7.6 CenterZ=0 NormalX=0 NormalY=0 NormalZ=1 AngleXU=0 Radius=4
    g12: Circle CenterX=-78.51 CenterY=34.8 CenterZ=0 NormalX=0 NormalY=0 NormalZ=1 AngleXU=0 Radius=1.6
    g13: Circle CenterX=-78.51 CenterY=34.8 CenterZ=0 NormalX=0 NormalY=0 NormalZ=1 AngleXU=0 Radius=4
  constraints (35):
    c: Diameter(g0) = 3.2
    c: Diameter(g1) = 8
    c: Coincident(g0,g1)
    c: Diameter(g2) = 3.2
    c: Diameter(g3) = 8
    c: Coincident(g3,g2)
    c: Tangent(g2,g-7)
    c: Diameter(g4) = 3.2
    c: Diameter(g5) = 8
    c: Coincident(g5,g4)
    c: Tangent(g4,g-7)
    c: Tangent(g4,g-8)
    c: Diameter(g6) = 3.2
    c: Diameter(g7) = 8
    c: Coincident(g7,g6)
    c: Tangent(g6,g-9)
    c: Tangent(g6,g-10)
    c: Diameter(g8) = 3.2
    c: Diameter(g9) = 8
    c: Coincident(g9,g8)
    c: Tangent(g8,g-10)
    c: Tangent(g8,g-11)
    c: Diameter(g10) = 3.2
    c: Diameter(g11) = 8
    c: Diameter(g12) = 3.2
    c: Diameter(g13) = 8
    c: Coincident(g12,g13)
    c: Coincident(g10,g11)
    c: Tangent(g12,g-7)
    c: DistanceX(g12,g10) = 0
    c: Tangent(g2,g-6)
    c: Tangent(g0,g-6)
    c: Tangent(g0,g-3)
    c: Tangent(g10,g-3)
    c: Tangent(g10,g-4)
FEATURE [Part::Extrusion] Extrude012  label="extrude guide per coperture laterali"
  Base = -> Sketch016
  Dir = (0,-1,2e-16)
  DirMode = 2
  FaceMakerClass = Part::FaceMakerBullseye
  FaceMakerMode = 3
  LengthFwd = 25.2
  LengthRev = 0
  Solid = true
  Symmetric = true
FEATURE [Sketcher::SketchObject] Sketch017  label="supporto CAM"
  ArcFitTolerance = 1e-06
  AttachmentSupport = -> [XZ_Plane]
  ExternalGeometry = -> [Sketch]
  FullyConstrained = true
  MakeInternals = false
  MapMode = 5
  Placement = pos=(0,0,0) rot=(1,0,0;1.5708rad)
  sketch-geometry (6):
    g0: LineSegment StartX=-2.4 StartY=48 StartZ=0 EndX=-2.4 EndY=41.2 EndZ=0
    g1: LineSegment StartX=-2.4 StartY=48 StartZ=0 EndX=-34 EndY=48 EndZ=0
    g2: LineSegment StartX=-34 StartY=48 StartZ=0 EndX=-34 EndY=46.72 EndZ=0
    g3: LineSegment StartX=-34 StartY=46.72 StartZ=0 EndX=-36 EndY=46.72 EndZ=0
    g4: LineSegment StartX=-36 StartY=46.72 StartZ=0 EndX=-36 EndY=41.2 EndZ=0
    g5: LineSegment StartX=-36 StartY=41.2 StartZ=0 EndX=-2.4 EndY=41.2 EndZ=0
  constraints (15):
    c: Coincident(g1,g0)
    c: Horizontal(g1)
    c: Coincident(g2,g1)
    c: Vertical(g2)
    c: Coincident(g3,g2)
    c: Horizontal(g3)
    c: Coincident(g4,g3)
    c: Coincident(g5,g4)
    c: DistanceX(g1,g0) = 31.6
    c: Coincident(g5,g0)
    c: Vertical(g4)
    c: DistanceY(g2,g1) = 1.28
    c: Coincident(g0,g-3)
    c: Coincident(g0,g-3)
    c: Coincident(g4,g-4)
FEATURE [Part::Extrusion] Extrude013  label="Extrude supporto CAM"
  Base = -> Sketch017
  Dir = (0,-1,2e-16)
  DirMode = 2
  FaceMakerClass = Part::FaceMakerBullseye
  FaceMakerMode = 3
  LengthFwd = 17.8
  LengthRev = 0
  Solid = true
  Symmetric = true
FEATURE [Sketcher::SketchObject] Sketch018  label="Scavo CAM"
  ArcFitTolerance = 1e-06
  AttachmentSupport = -> [YZ_Plane]
  ExternalGeometry = -> [Sketch]
  FullyConstrained = true
  MakeInternals = false
  MapMode = 5
  Placement = pos=(0,0,0) rot=(0.57735,0.57735,0.57735;2.0944rad)
  sketch-geometry (4):
    g0: LineSegment StartX=-7.73 StartY=48 StartZ=0 EndX=7.73 EndY=48 EndZ=0
    g1: LineSegment [constr] StartX=1.07e-14 StartY=48 StartZ=0 EndX=0 EndY=43.5155 EndZ=0
    g2: ArcOfCircle CenterX=9e-15 CenterY=52.42 CenterZ=0 NormalX=0 NormalY=0 NormalZ=1 AngleXU=0 Radius=8.90445 StartAngle=3.66102 EndAngle=5.76376
    g3: Circle [constr] CenterX=9e-15 CenterY=52.42 CenterZ=0 NormalX=0 NormalY=0 NormalZ=1 AngleXU=0 Radius=8.9
  constraints (13):
    c: Horizontal(g0)
    c: DistanceY(g-3,g0) = 0
    c: DistanceX(g0,g0) = 15.46
    c: DistanceX(g0,g-3) = 7.73
    c: DistanceX(g-3) = 0
    c: Coincident(g1,g-3)
    c: PointOnObject(g1,g-2)
    c: Coincident(g2,g0)
    c: Coincident(g2,g0)
    c: PointOnObject(g1,g2)
    c: Diameter(g3) = 17.8
    c: DistanceY(g1,g3) = 4.42
    c: Coincident(g2,g3)
FEATURE [Part::Extrusion] Extrude014  label="Extrude Scavo CAM"
  Base = -> Sketch018
  Dir = (1,0,0)
  DirMode = 2
  FaceMakerClass = Part::FaceMakerBullseye
  FaceMakerMode = 3
  LengthFwd = -34
  LengthRev = 0
  Solid = true
  Symmetric = false
FEATURE [Sketcher::SketchObject] Sketch019  label="scavo rumble"
  ArcFitTolerance = 1e-06
  AttachmentSupport = -> [XZ_Plane]
  ExternalGeometry = -> [Sketch]
  FullyConstrained = true
  MakeInternals = false
  MapMode = 5
  Placement = pos=(0,0,0) rot=(1,0,0;1.5708rad)
  sketch-geometry (6):
    g0: LineSegment StartX=-163.771 StartY=-21.9058 StartZ=0 EndX=-158.636 EndY=-23.5745 EndZ=0
    g1: LineSegment StartX=-158.636 StartY=-23.5745 StartZ=0 EndX=-165.743 EndY=-45.4488 EndZ=0
    g2: LineSegment StartX=-165.743 StartY=-45.4488 StartZ=0 EndX=-170.879 EndY=-43.7801 EndZ=0
    g3: LineSegment StartX=-170.879 StartY=-43.7801 StartZ=0 EndX=-163.771 EndY=-21.9058 EndZ=0
    g4: LineSegment [constr] StartX=-145.51 StartY=22 StartZ=0 EndX=-160.157 EndY=-23.0801 EndZ=0
    g5: LineSegment [constr] StartX=-158.636 StartY=-23.5745 StartZ=0 EndX=-160.157 EndY=-23.0801 EndZ=0
  constraints (17):
    c: Coincident(g1,g0)
    c: Coincident(g2,g1)
    c: Coincident(g3,g2)
    c: Coincident(g3,g0)
    c: Parallel(g3,g-3)
    c: Parallel(g3,g1)
    c: Perpendicular(g3,g0)
    c: Perpendicular(g2,g3)
    c: Distance(g2,g0) = 23
    c: Parallel(g4,g-3)
    c: Distance(g4) = 47.4
    c: Coincident(g4,g-3)
    c: Parallel(g5,g0)
    c: Distance(g5) = 1.6
    c: Coincident(g5,g0)
    c: Distance(g5,g0) = 3.8
    c: Coincident(g5,g4)
FEATURE [Part::Extrusion] Extrude015  label="scavo rumble001"
  Base = -> Sketch019
  Dir = (0,-1,2e-16)
  DirMode = 2
  FaceMakerClass = Part::FaceMakerBullseye
  FaceMakerMode = 3
  LengthFwd = 21
  LengthRev = 0
  Solid = true
  Symmetric = true
FEATURE [Sketcher::SketchObject] Sketch020  label="fermo rumble"
  ArcFitTolerance = 1e-06
  AttachmentSupport = -> [XZ_Plane]
  ExternalGeometry = -> [Sketch019,Sketch]
  FullyConstrained = true
  MakeInternals = false
  MapMode = 5
  Placement = pos=(0,0,0) rot=(1,0,0;1.5708rad)
  sketch-geometry (16):
    g0: LineSegment [constr] StartX=-165.905 StartY=-40.7697 StartZ=0 EndX=-167.265 EndY=-44.9544 EndZ=0
    g1: LineSegment [constr] StartX=-167.265 StartY=-44.9544 StartZ=0 EndX=-165.743 EndY=-45.4488 EndZ=0
    g2: LineSegment StartX=-167.318 StartY=-37.9976 StartZ=0 EndX=-165.225 EndY=-38.6774 EndZ=0
    g3: LineSegment StartX=-165.225 StartY=-38.6774 StartZ=0 EndX=-165.905 EndY=-40.7697 EndZ=0
    g4: LineSegment StartX=-165.905 StartY=-40.7697 StartZ=0 EndX=-167.997 EndY=-40.0899 EndZ=0
    g5: LineSegment StartX=-167.997 StartY=-40.0899 StartZ=0 EndX=-167.318 EndY=-37.9976 EndZ=0
    g6: LineSegment StartX=-166.823 StartY=-36.4759 StartZ=0 EndX=-163.399 EndY=-37.5883 EndZ=0
    g7: LineSegment StartX=-163.399 StartY=-37.5883 StartZ=0 EndX=-165.006 EndY=-42.5338 EndZ=0
    g8: LineSegment StartX=-165.006 StartY=-42.5338 StartZ=0 EndX=-168.43 EndY=-41.4214 EndZ=0
    g9: LineSegment StartX=-169.457 StartY=-39.4053 StartZ=0 EndX=-168.839 EndY=-37.5031 EndZ=0
    g10: LineSegment [constr] StartX=-168.839 StartY=-37.5031 StartZ=0 EndX=-168.345 EndY=-35.9815 EndZ=0
    g11: LineSegment [constr] StartX=-168.345 StartY=-35.9815 StartZ=0 EndX=-166.823 EndY=-36.4759 EndZ=0
    g12: ArcOfCircle CenterX=-167.936 CenterY=-39.8997 CenterZ=0 NormalX=0 NormalY=0 NormalZ=1 AngleXU=0 Radius=1.6 StartAngle=2.82743 EndAngle=4.39823
    g13: GeomPoint [constr] X=-169.952 Y=-40.9269 Z=0
    g14: ArcOfCircle CenterX=-167.318 CenterY=-37.9976 CenterZ=0 NormalX=0 NormalY=0 NormalZ=1 AngleXU=0 Radius=1.6 StartAngle=1.25664 EndAngle=2.82743
    g15: GeomPoint [constr] X=-168.345 Y=-35.9815 Z=0
  constraints (42):
    c: Parallel(g0,g-4)
    c: Distance(g0) = 4.4
    c: Coincident(g1,g0)
    c: Perpendicular(g0,g1)
    c: Distance(g1) = 1.6
    c: Coincident(g1,g-5)
    c: Coincident(g3,g2)
    c: Coincident(g4,g3)
    c: Coincident(g5,g4)
    c: Coincident(g5,g2)
    c: Parallel(g3,g-4)
    c: Parallel(g3,g5)
    c: Perpendicular(g2,g3)
    c: Parallel(g4,g2)
    c: Distance(g2) = 2.2
    c: Distance(g3) = 2.2
    c: Coincident(g7,g6)
    c: Coincident(g8,g7)
    c: Parallel(g7,g-4)
    c: Parallel(g7,g9)
    c: Perpendicular(g6,g7)
    c: Parallel(g6,g8)
    c: Distance(g6,g15) = 5.2
    c: Distance(g7) = 5.2
    c: Coincident(g11,g10)
    c: Parallel(g10,g9)
    c: Parallel(g11,g6)
    c: Distance(g10) = 1.6
    c: Distance(g11) = 1.6
    c: Coincident(g10,g15)
    c: Distance(g11,g2) = 1.6
    c: Distance(g2,g10) = 1.6
    c: PointOnObject(g13,g8)
    c: PointOnObject(g13,g9)
    c: Tangent(g8,g12) = 1.5708
    c: Tangent(g9,g12) = 1.5708
    c: PointOnObject(g15,g9)
    c: Tangent(g6,g14) = 1.5708
    c: Tangent(g9,g14) = 1.5708
    c: Equal(g12,g14)
    c: Coincident(g6,g11)
    c: Coincident(g3,g0)
FEATURE [Part::Extrusion] Extrude016  label="Extrude fermo rumble"
  Base = -> Sketch020
  Dir = (0,-1,2e-16)
  DirMode = 2
  FaceMakerClass = Part::FaceMakerBullseye
  FaceMakerMode = 3
  LengthFwd = 25.2
  LengthRev = 0
  Solid = true
  Symmetric = true
FEATURE [Sketcher::SketchObject] Sketch021  label="perno fermo rumble001"
  ArcFitTolerance = 1e-06
  AttachmentSupport = -> [XZ_Plane001]
  FullyConstrained = true
  MakeInternals = false
  MapMode = 5
  Placement = pos=(0,0,0) rot=(1,0,0;1.5708rad)
  sketch-geometry (16):
    g0: LineSegment StartX=0 StartY=0.45 StartZ=0 EndX=0 EndY=1.55 EndZ=0
    g1: LineSegment StartX=0.45 StartY=2 StartZ=0 EndX=1.55 EndY=2 EndZ=0
    g2: LineSegment StartX=2 StartY=1.55 StartZ=0 EndX=2 EndY=0.45 EndZ=0
    g3: LineSegment StartX=1.55 StartY=0 StartZ=0 EndX=0.45 EndY=0 EndZ=0
    g4: ArcOfCircle [constr] CenterX=0.45 CenterY=1.55 CenterZ=0 NormalX=0 NormalY=0 NormalZ=1 AngleXU=0 Radius=0.45 StartAngle=1.5708 EndAngle=3.14159
    g5: GeomPoint [constr] X=0 Y=2 Z=0
    g6: LineSegment StartX=0.45 StartY=2 StartZ=0 EndX=0 EndY=1.55 EndZ=0
    g7: ArcOfCircle [constr] CenterX=1.55 CenterY=1.55 CenterZ=0 NormalX=0 NormalY=0 NormalZ=1 AngleXU=0 Radius=0.45 StartAngle=0 EndAngle=1.5708
    g8: GeomPoint [constr] X=2 Y=2 Z=0
    g9: LineSegment StartX=2 StartY=1.55 StartZ=0 EndX=1.55 EndY=2 EndZ=0
    g10: ArcOfCircle [constr] CenterX=1.55 CenterY=0.45 CenterZ=0 NormalX=0 NormalY=0 NormalZ=1 AngleXU=0 Radius=0.45 StartAngle=4.71239 EndAngle=6.28319
    g11: GeomPoint [constr] X=2 Y=0 Z=0
    g12: LineSegment StartX=1.55 StartY=0 StartZ=0 EndX=2 EndY=0.45 EndZ=0
    g13: ArcOfCircle [constr] CenterX=0.45 CenterY=0.45 CenterZ=0 NormalX=0 NormalY=0 NormalZ=1 AngleXU=0 Radius=0.45 StartAngle=3.14159 EndAngle=4.71239
    g14: GeomPoint [constr] X=0 Y=0 Z=0
    g15: LineSegment StartX=0 StartY=0.45 StartZ=0 EndX=0.45 EndY=0 EndZ=0
  constraints (35):
    c: Coincident(g14,g-1)
    c: PointOnObject(g5,g-2)
    c: Horizontal(g1)
    c: Vertical(g2)
    c: Horizontal(g3)
    c: DistanceX(g5,g8) = 2
    c: DistanceY(g11,g8) = 2
    c: PointOnObject(g5,g0)
    c: PointOnObject(g5,g1)
    c: Tangent(g0,g4) = 1.5708
    c: Tangent(g1,g4) = 1.5708
    c: Coincident(g6,g0)
    c: Coincident(g6,g1)
    c: PointOnObject(g8,g2)
    c: PointOnObject(g8,g1)
    c: Tangent(g2,g7) = 1.5708
    c: Tangent(g1,g7) = 1.5708
    c: Coincident(g9,g2)
    c: Coincident(g9,g1)
    c: PointOnObject(g11,g2)
    c: PointOnObject(g11,g3)
    c: Tangent(g2,g10) = 1.5708
    c: Tangent(g3,g10) = 1.5708
    c: Coincident(g12,g2)
    c: Coincident(g12,g3)
    c: PointOnObject(g14,g0)
    c: PointOnObject(g14,g3)
    c: Tangent(g0,g13) = 1.5708
    c: Tangent(g3,g13) = 1.5708
    c: Coincident(g15,g0)
    c: Coincident(g15,g3)
    c: Equal(g6,g9)
    c: Equal(g9,g12)
    c: Equal(g12,g15)
    c: DistanceX(g14,g3) = 0.45
FEATURE [Sketcher::SketchObject] Sketch022  label="fori per M3x5(OD)x6(L)"
  ArcFitTolerance = 1e-06
  AttachmentSupport = -> [XZ_Plane]
  ExternalGeometry = -> [Sketch016]
  FullyConstrained = true
  MakeInternals = false
  MapMode = 5
  Placement = pos=(0,0,0) rot=(1,0,0;1.5708rad)
  sketch-geometry (7):
    g0: Circle CenterX=-5.6 CenterY=34.8 CenterZ=0 NormalX=0 NormalY=0 NormalZ=1 AngleXU=0 Radius=2.5
    g1: Circle CenterX=-5.6 CenterY=7.6 CenterZ=0 NormalX=0 NormalY=0 NormalZ=1 AngleXU=0 Radius=2.5
    g2: Circle CenterX=-78.51 CenterY=34.8 CenterZ=0 NormalX=0 NormalY=0 NormalZ=1 AngleXU=0 Radius=2.5
    g3: Circle CenterX=-78.51 CenterY=7.6 CenterZ=0 NormalX=0 NormalY=0 NormalZ=1 AngleXU=0 Radius=2.5
    g4: Circle CenterX=-184.08 CenterY=34.8 CenterZ=0 NormalX=0 NormalY=0 NormalZ=1 AngleXU=0 Radius=2.5
    g5: Circle CenterX=-179.305 CenterY=-76.8316 CenterZ=0 NormalX=0 NormalY=0 NormalZ=1 AngleXU=0 Radius=2.5
    g6: Circle CenterX=-213.443 CenterY=-76.8316 CenterZ=0 NormalX=0 NormalY=0 NormalZ=1 AngleXU=0 Radius=2.5
  constraints (14):
    c: Diameter(g0) = 5
    c: Diameter(g1) = 5
    c: Diameter(g2) = 5
    c: Diameter(g3) = 5
    c: Diameter(g4) = 5
    c: Diameter(g5) = 5
    c: Diameter(g6) = 5
    c: Coincident(g0,g-8)
    c: Coincident(g1,g-9)
    c: Coincident(g2,g-6)
    c: Coincident(g3,g-7)
    c: Coincident(g4,g-5)
    c: Coincident(g5,g-4)
    c: Coincident(g6,g-3)
FEATURE [Part::Extrusion] Extrude018  label="Extrude fori M3x5x6 - dx"
  Base = -> Sketch022
  Dir = (0,-1,2e-16)
  DirMode = 2
  FaceMakerClass = Part::FaceMakerBullseye
  FaceMakerMode = 3
  LengthFwd = 6.2
  LengthRev = 0
  Placement = pos=(0,-9.5,0) rot=(0,0,1;0rad)
  Solid = true
  Symmetric = true
FEATURE [Part::Extrusion] Extrude019  label="Extrude fori M3x5x6 - sx"
  Base = -> Sketch022
  Dir = (0,-1,2e-16)
  DirMode = 2
  FaceMakerClass = Part::FaceMakerBullseye
  FaceMakerMode = 3
  LengthFwd = 6.2
  LengthRev = 0
  Placement = pos=(0,9.5,0) rot=(0,0,1;0rad)
  Solid = true
  Symmetric = true
FEATURE [Sketcher::SketchObject] Sketch023  label="foro anteriore M3x5x6"
  ArcFitTolerance = 1e-06
  AttachmentSupport = -> [YZ_Plane]
  FullyConstrained = true
  MakeInternals = false
  MapMode = 5
  Placement = pos=(0,0,0) rot=(0.57735,0.57735,0.57735;2.0944rad)
  sketch-geometry (2):
    g0: LineSegment [constr] StartX=0 StartY=0 StartZ=0 EndX=0 EndY=38.6 EndZ=0
    g1: Circle CenterX=0 CenterY=38.6 CenterZ=0 NormalX=0 NormalY=0 NormalZ=1 AngleXU=0 Radius=2.5
  constraints (5):
    c: Coincident(g0,g-1)
    c: PointOnObject(g0,g-2)
    c: DistanceY(g0,g0) = 38.6
    c: Diameter(g1) = 5
    c: Coincident(g1,g0)
FEATURE [Part::Extrusion] Extrude020  label="Extrude foro anteriore M3x5x6"
  Base = -> Sketch023
  Dir = (1,0,0)
  DirMode = 2
  FaceMakerClass = Part::FaceMakerBullseye
  FaceMakerMode = 3
  LengthFwd = -6.2
  LengthRev = 0
  Solid = true
  Symmetric = false
FEATURE [Sketcher::SketchObject] Sketch024  label="fori per viti frontale"
  ArcFitTolerance = 1e-06
  AttachmentSupport = -> [YZ_Plane]
  FullyConstrained = true
  MakeInternals = false
  MapMode = 5
  Placement = pos=(0,0,0) rot=(0.57735,0.57735,0.57735;2.0944rad)
  sketch-geometry (9):
    g0: LineSegment [constr] StartX=-10.3 StartY=30.721 StartZ=0 EndX=10.3 EndY=30.721 EndZ=0
    g1: LineSegment [constr] StartX=10.3 StartY=30.721 StartZ=0 EndX=10.3 EndY=10.121 EndZ=0
    g2: LineSegment [constr] StartX=10.3 StartY=10.121 StartZ=0 EndX=-10.3 EndY=10.121 EndZ=0
    g3: LineSegment [constr] StartX=-10.3 StartY=10.121 StartZ=0 EndX=-10.3 EndY=30.721 EndZ=0
    g4: LineSegment [constr] StartX=0 StartY=0 StartZ=0 EndX=0 EndY=10.121 EndZ=0
    g5: Circle CenterX=-10.3 CenterY=30.721 CenterZ=0 NormalX=0 NormalY=0 NormalZ=1 AngleXU=0 Radius=2
    g6: Circle CenterX=10.3 CenterY=30.721 CenterZ=0 NormalX=0 NormalY=0 NormalZ=1 AngleXU=0 Radius=2
    g7: Circle CenterX=-10.3 CenterY=10.121 CenterZ=0 NormalX=0 NormalY=0 NormalZ=1 AngleXU=0 Radius=2
    g8: Circle CenterX=10.3 CenterY=10.121 CenterZ=0 NormalX=0 NormalY=0 NormalZ=1 AngleXU=0 Radius=2
  constraints (22):
    c: Horizontal(g0)
    c: Coincident(g1,g0)
    c: Vertical(g1)
    c: Coincident(g2,g1)
    c: Horizontal(g2)
    c: Coincident(g3,g2)
    c: Coincident(g3,g0)
    c: Vertical(g3)
    c: DistanceX(g0,g0) = 20.6
    c: DistanceY(g3,g3) = 20.6
    c: Coincident(g4,g-1)
    c: PointOnObject(g4,g-2)
    c: DistanceY(g4,g4) = 10.121
    c: Symmetric(g2,g2,g4)
    c: Diameter(g5) = 4
    c: Diameter(g6) = 4
    c: Diameter(g7) = 4
    c: Diameter(g8) = 4
    c: Coincident(g5,g0)
    c: Coincident(g6,g0)
    c: Coincident(g7,g2)
    c: Coincident(g8,g1)
FEATURE [Part::Extrusion] Extrude021  label="Extrude fori per viti frontale"
  Base = -> Sketch024
  Dir = (1,0,0)
  DirMode = 2
  FaceMakerClass = Part::FaceMakerBullseye
  FaceMakerMode = 3
  LengthFwd = -2.4
  LengthRev = 0
  Solid = true
  Symmetric = false
FEATURE [Sketcher::SketchObject] Sketch025  label="foro per filo CAM"
  ArcFitTolerance = 1e-06
  AttachmentSupport = -> [XZ_Plane]
  ExternalGeometry = -> [Sketch]
  FullyConstrained = true
  MakeInternals = false
  MapMode = 5
  Placement = pos=(0,0,0) rot=(1,0,0;1.5708rad)
  sketch-geometry (4):
    g0: LineSegment StartX=-44.6 StartY=41.2 StartZ=0 EndX=-44.6 EndY=36.4 EndZ=0
    g1: LineSegment StartX=-44.6 StartY=36.4 StartZ=0 EndX=-54.6 EndY=36.4 EndZ=0
    g2: LineSegment StartX=-54.6 StartY=36.4 StartZ=0 EndX=-50.4 EndY=41.2 EndZ=0
    g3: LineSegment StartX=-50.4 StartY=41.2 StartZ=0 EndX=-44.6 EndY=41.2 EndZ=0
  constraints (11):
    c: Vertical(g0)
    c: Coincident(g1,g0)
    c: Horizontal(g1)
    c: Coincident(g2,g1)
    c: Coincident(g3,g2)
    c: Coincident(g3,g0)
    c: Horizontal(g3)
    c: Coincident(g0,g-3)
    c: DistanceY(g0,g-4) = 0
    c: DistanceX(g3,g3) = 5.8
    c: DistanceX(g1,g1) = 10
FEATURE [Part::Extrusion] Extrude022  label="Extrude foro per filo CAM dx"
  Base = -> Sketch025
  Dir = (0,-1,2e-16)
  DirMode = 2
  FaceMakerClass = Part::FaceMakerBullseye
  FaceMakerMode = 3
  LengthFwd = 4.9
  LengthRev = 0
  Placement = pos=(0,6.95,0) rot=(0,0,1;0rad)
  Solid = true
  Symmetric = true
FEATURE [Part::Extrusion] Extrude023  label="Extrude foro per filo CAM sx"
  Base = -> Sketch025
  Dir = (0,-1,2e-16)
  DirMode = 2
  FaceMakerClass = Part::FaceMakerBullseye
  FaceMakerMode = 3
  LengthFwd = 4.9
  LengthRev = 0
  Placement = pos=(0,-6.95,0) rot=(0,0,1;0rad)
  Solid = true
  Symmetric = true
FEATURE [Sketcher::SketchObject] Sketch026  label="foro sotto anteriore M3x5x6"
  ArcFitTolerance = 1e-06
  AttachmentSupport = -> [XY_Plane]
  FullyConstrained = true
  MakeInternals = false
  MapMode = 5
  sketch-geometry (2):
    g0: LineSegment [constr] StartX=0 StartY=0 StartZ=0 EndX=-16.5 EndY=0 EndZ=0
    g1: Circle CenterX=-16.5 CenterY=0 CenterZ=0 NormalX=0 NormalY=0 NormalZ=1 AngleXU=0 Radius=2.5
  constraints (5):
    c: Distance(g0) = 16.5
    c: Coincident(g0,g-1)
    c: PointOnObject(g0,g-1)
    c: Diameter(g1) = 5
    c: Coincident(g0,g1)
FEATURE [Sketcher::SketchObject] Sketch027  label="foro sotto posteriore M3x5x6"
  ArcFitTolerance = 1e-06
  AttachmentSupport = -> [XY_Plane]
  ExternalGeometry = -> [Sketch]
  FullyConstrained = true
  MakeInternals = false
  MapMode = 5
  sketch-geometry (2):
    g0: LineSegment [constr] StartX=-82.8 StartY=2e-16 StartZ=0 EndX=-71.3 EndY=2e-16 EndZ=0
    g1: Circle CenterX=-71.3 CenterY=2e-16 CenterZ=0 NormalX=0 NormalY=0 NormalZ=1 AngleXU=0 Radius=2.5
  constraints (5):
    c: Distance(g0) = 11.5
    c: Coincident(g0,g-3)
    c: PointOnObject(g0,g-3)
    c: Diameter(g1) = 5
    c: Coincident(g1,g0)
FEATURE [Sketcher::SketchObject] Sketch029  label="fori sotto impugnatura"
  ArcFitTolerance = 1e-06
  AttachmentSupport = -> [XY_Plane]
  ExternalGeometry = -> [Sketch]
  FullyConstrained = true
  MakeInternals = false
  MapMode = 5
  sketch-geometry (15):
    g0: LineSegment [constr] StartX=-175.232 StartY=-1.83e-14 StartZ=0 EndX=-191.232 EndY=0 EndZ=0
    g1: Circle CenterX=-191.232 CenterY=0 CenterZ=0 NormalX=0 NormalY=0 NormalZ=1 AngleXU=0 Radius=3.95
    g2: LineSegment [constr] StartX=-175.232 StartY=-1.83e-14 StartZ=0 EndX=-204.275 EndY=0 EndZ=0
    g3: LineSegment StartX=-204.275 StartY=3.525 StartZ=0 EndX=-204.275 EndY=-3.525 EndZ=0
    g4: LineSegment StartX=-205.4 StartY=-4.65 StartZ=0 EndX=-206.65 EndY=-4.65 EndZ=0
    g5: LineSegment StartX=-207.775 StartY=-3.525 StartZ=0 EndX=-207.775 EndY=3.525 EndZ=0
    g6: LineSegment StartX=-206.65 StartY=4.65 StartZ=0 EndX=-205.4 EndY=4.65 EndZ=0
    g7: ArcOfCircle CenterX=-206.65 CenterY=3.525 CenterZ=0 NormalX=0 NormalY=0 NormalZ=1 AngleXU=0 Radius=1.125 StartAngle=1.5708 EndAngle=3.14159
    g8: GeomPoint [constr] X=-207.775 Y=4.65 Z=0
    g9: ArcOfCircle CenterX=-205.4 CenterY=3.525 CenterZ=0 NormalX=0 NormalY=0 NormalZ=1 AngleXU=0 Radius=1.125 StartAngle=0 EndAngle=1.5708
    g10: GeomPoint [constr] X=-204.275 Y=4.65 Z=0
    g11: ArcOfCircle CenterX=-205.4 CenterY=-3.525 CenterZ=0 NormalX=0 NormalY=0 NormalZ=1 AngleXU=0 Radius=1.125 StartAngle=4.71239 EndAngle=6.28319
    g12: GeomPoint [constr] X=-204.275 Y=-4.65 Z=0
    g13: ArcOfCircle CenterX=-206.65 CenterY=-3.525 CenterZ=0 NormalX=0 NormalY=0 NormalZ=1 AngleXU=0 Radius=1.125 StartAngle=3.14159 EndAngle=4.71239
    g14: GeomPoint [constr] X=-207.775 Y=-4.65 Z=0
  constraints (35):
    c: Distance(g0) = 16
    c: Coincident(g0,g-3)
    c: PointOnObject(g0,g-1)
    c: Diameter(g1) = 7.9
    c: Coincident(g1,g0)
    c: Coincident(g2,g0)
    c: PointOnObject(g2,g-1)
    c: Vertical(g3)
    c: Horizontal(g4)
    c: Vertical(g5)
    c: Horizontal(g6)
    c: DistanceY(g12,g10) = 9.3
    c: DistanceX(g8,g10) = 3.5
    c: Symmetric(g10,g12,g2)
    c: PointOnObject(g8,g5)
    c: PointOnObject(g8,g6)
    c: Tangent(g5,g7) = 1.5708
    c: Tangent(g6,g7) = 1.5708
    c: PointOnObject(g10,g3)
    c: PointOnObject(g10,g6)
    c: Tangent(g3,g9) = 1.5708
    c: Tangent(g6,g9) = 1.5708
    c: PointOnObject(g12,g3)
    c: PointOnObject(g12,g4)
    c: Tangent(g3,g11) = 1.5708
    c: Tangent(g4,g11) = 1.5708
    c: PointOnObject(g14,g4)
    c: PointOnObject(g14,g5)
    c: Tangent(g4,g13) = 1.5708
    c: Tangent(g5,g13) = 1.5708
    c: Equal(g7,g9)
    c: Equal(g9,g11)
    c: Equal(g11,g13)
    c: DistanceX(g6,g6) = 1.25
    c: DistanceX(g-5,g5) = 6.8
FEATURE [Sketcher::SketchObject] Sketch030  label="fori superiori per solenoide e oled"
  ArcFitTolerance = 1e-06
  AttachmentSupport = -> [XY_Plane]
  ExternalGeometry = -> [Sketch]
  FullyConstrained = true
  MakeInternals = false
  MapMode = 5
  sketch-geometry (33):
    g0: LineSegment [constr] StartX=-181.6 StartY=1.12e-14 StartZ=0 EndX=-169.91 EndY=0 EndZ=0
    g1: LineSegment [constr] StartX=-169.91 StartY=0 StartZ=0 EndX=-169.91 EndY=-2.6 EndZ=0
    g2: LineSegment [constr] StartX=-169.91 StartY=0 StartZ=0 EndX=-169.91 EndY=2.6 EndZ=0
    g3: LineSegment StartX=-169.91 StartY=4.975 StartZ=0 EndX=-169.91 EndY=8.225 EndZ=0
    g4: LineSegment StartX=-167.535 StartY=10.6 StartZ=0 EndX=-167.285 EndY=10.6 EndZ=0
    g5: LineSegment StartX=-164.91 StartY=8.225 StartZ=0 EndX=-164.91 EndY=4.975 EndZ=0
    g6: LineSegment StartX=-167.285 StartY=2.6 StartZ=0 EndX=-167.535 EndY=2.6 EndZ=0
    g7: LineSegment StartX=-169.91 StartY=-4.975 StartZ=0 EndX=-169.91 EndY=-8.225 EndZ=0
    g8: LineSegment StartX=-167.535 StartY=-10.6 StartZ=0 EndX=-167.285 EndY=-10.6 EndZ=0
    g9: LineSegment StartX=-164.91 StartY=-8.225 StartZ=0 EndX=-164.91 EndY=-4.975 EndZ=0
    g10: LineSegment StartX=-167.285 StartY=-2.6 StartZ=0 EndX=-167.535 EndY=-2.6 EndZ=0
    g11: ArcOfCircle CenterX=-167.535 CenterY=8.225 CenterZ=0 NormalX=0 NormalY=0 NormalZ=1 AngleXU=0 Radius=2.375 StartAngle=1.5708 EndAngle=3.14159
    g12: GeomPoint [constr] X=-169.91 Y=10.6 Z=0
    g13: ArcOfCircle CenterX=-167.285 CenterY=8.225 CenterZ=0 NormalX=0 NormalY=0 NormalZ=1 AngleXU=0 Radius=2.375 StartAngle=0 EndAngle=1.5708
    g14: GeomPoint [constr] X=-164.91 Y=10.6 Z=0
    g15: ArcOfCircle CenterX=-167.285 CenterY=4.975 CenterZ=0 NormalX=0 NormalY=0 NormalZ=1 AngleXU=0 Radius=2.375 StartAngle=4.71239 EndAngle=6.28319
    g16: GeomPoint [constr] X=-164.91 Y=2.6 Z=0
    g17: ArcOfCircle CenterX=-167.535 CenterY=4.975 CenterZ=0 NormalX=0 NormalY=0 NormalZ=1 AngleXU=0 Radius=2.375 StartAngle=3.14159 EndAngle=4.71239
    g18: GeomPoint [constr] X=-169.91 Y=2.6 Z=0
    g19: ArcOfCircle CenterX=-167.535 CenterY=-4.975 CenterZ=0 NormalX=0 NormalY=0 NormalZ=1 AngleXU=0 Radius=2.375 StartAngle=1.5708 EndAngle=3.14159
    g20: GeomPoint [constr] X=-169.91 Y=-2.6 Z=0
    g21: ArcOfCircle CenterX=-167.285 CenterY=-4.975 CenterZ=0 NormalX=0 NormalY=0 NormalZ=1 AngleXU=0 Radius=2.375 StartAngle=0 EndAngle=1.5708
    g22: GeomPoint [constr] X=-164.91 Y=-2.6 Z=0
    g23: ArcOfCircle CenterX=-167.285 CenterY=-8.225 CenterZ=0 NormalX=0 NormalY=0 NormalZ=1 AngleXU=0 Radius=2.375 StartAngle=4.71239 EndAngle=6.28319
    g24: GeomPoint [constr] X=-164.91 Y=-10.6 Z=0
    g25: ArcOfCircle CenterX=-167.535 CenterY=-8.225 CenterZ=0 NormalX=0 NormalY=0 NormalZ=1 AngleXU=0 Radius=2.375 StartAngle=3.14159 EndAngle=4.71239
    g26: GeomPoint [constr] X=-169.91 Y=-10.6 Z=0
    g27: LineSegment [constr] StartX=-181.6 StartY=1.12e-14 StartZ=0 EndX=-152.209 EndY=0 EndZ=0
    g28: LineSegment [constr] StartX=-181.6 StartY=1.12e-14 StartZ=0 EndX=-130.41 EndY=0 EndZ=0
    g29: LineSegment [constr] StartX=-152.209 StartY=0 StartZ=0 EndX=-152.209 EndY=6.95 EndZ=0
    g30: LineSegment [constr] StartX=-130.41 StartY=0 StartZ=0 EndX=-130.41 EndY=-6.95 EndZ=0
    g31: Circle CenterX=-152.209 CenterY=6.95 CenterZ=0 NormalX=0 NormalY=0 NormalZ=1 AngleXU=0 Radius=2.1
    g32: Circle CenterX=-130.41 CenterY=-6.95 CenterZ=0 NormalX=0 NormalY=0 NormalZ=1 AngleXU=0 Radius=2.1
  constraints (79):
    c: Distance(g0) = 11.69
    c: PointOnObject(g0,g-1)
    c: Coincident(g-4,g0)
    c: Distance(g1) = 2.6
    c: Coincident(g1,g0)
    c: Vertical(g1)
    c: Distance(g2) = 2.6
    c: Coincident(g2,g0)
    c: Vertical(g2)
    c: Distance(g18,g12) = 8
    c: Coincident(g18,g2)
    c: Vertical(g3)
    c: Distance(g14,g12) = 5
    c: Horizontal(g4)
    c: Distance(g16,g14) = 8
    c: Vertical(g5)
    c: Distance(g26,g20) = 8
    c: Coincident(g20,g1)
    c: Vertical(g7)
    c: Distance(g26,g24) = 5
    c: Horizontal(g8)
    c: Distance(g24,g22) = 8
    c: Vertical(g9)
    c: PointOnObject(g12,g3)
    c: PointOnObject(g12,g4)
    c: Tangent(g3,g11) = 1.5708
    c: Tangent(g4,g11) = 1.5708
    c: PointOnObject(g14,g5)
    c: PointOnObject(g14,g4)
    c: Tangent(g5,g13) = 1.5708
    c: Tangent(g4,g13) = 1.5708
    c: PointOnObject(g16,g5)
    c: PointOnObject(g16,g6)
    c: Tangent(g5,g15) = 1.5708
    c: Tangent(g6,g15) = 1.5708
    c: PointOnObject(g18,g3)
    c: PointOnObject(g18,g6)
    c: Tangent(g3,g17) = 1.5708
    c: Tangent(g6,g17) = 1.5708
    c: Equal(g11,g13)
    c: Equal(g13,g15)
    c: Equal(g15,g17)
    c: DistanceX(g4,g4) = 0.25
    c: PointOnObject(g20,g7)
    c: PointOnObject(g20,g10)
    c: Tangent(g7,g19) = -1.5708
    c: Tangent(g10,g19) = -1.5708
    c: PointOnObject(g22,g9)
    c: PointOnObject(g22,g10)
    c: Tangent(g9,g21) = -1.5708
    c: Tangent(g10,g21) = -1.5708
    c: PointOnObject(g24,g9)
    c: PointOnObject(g24,g8)
    c: Tangent(g9,g23) = -1.5708
    c: Tangent(g8,g23) = -1.5708
    c: PointOnObject(g26,g8)
    c: PointOnObject(g26,g7)
    c: Tangent(g8,g25) = -1.5708
    c: Tangent(g7,g25) = -1.5708
    c: Equal(g19,g21)
    c: Equal(g21,g23)
    c: Equal(g23,g25)
    c: DistanceX(g10,g10) = 0.25
    c: Distance(g27) = 29.391
    c: Coincident(g27,g0)
    c: PointOnObject(g27,g-1)
    c: Distance(g28) = 51.19
    c: Coincident(g28,g0)
    c: PointOnObject(g28,g-1)
    c: Distance(g29) = 6.95
    c: Coincident(g29,g27)
    c: Vertical(g29)
    c: Distance(g30) = 6.95
    c: Coincident(g30,g28)
    c: Vertical(g30)
    c: Diameter(g31) = 4.2
    c: Diameter(g32) = 4.2
    c: Coincident(g32,g30)
    c: Coincident(g31,g29)
FEATURE [Sketcher::SketchObject] Sketch031  label="fori inferiori switch pompa"
  ArcFitTolerance = 1e-06
  AttachmentSupport = -> [XY_Plane]
  ExternalGeometry = -> [Sketch]
  FullyConstrained = true
  MakeInternals = false
  MapMode = 5
  sketch-geometry (4):
    g0: LineSegment [constr] StartX=-57.2 StartY=1.9e-15 StartZ=0 EndX=-62.45 EndY=1.9e-15 EndZ=0
    g1: LineSegment [constr] StartX=-62.45 StartY=3.25 StartZ=0 EndX=-62.45 EndY=-3.25 EndZ=0
    g2: Circle CenterX=-62.45 CenterY=3.25 CenterZ=0 NormalX=0 NormalY=0 NormalZ=1 AngleXU=0 Radius=1.6
    g3: Circle CenterX=-62.45 CenterY=-3.25 CenterZ=0 NormalX=0 NormalY=0 NormalZ=1 AngleXU=0 Radius=1.6
  constraints (10):
    c: Distance(g0) = 5.25
    c: Coincident(g0,g-3)
    c: PointOnObject(g0,g-3)
    c: Vertical(g1)
    c: DistanceY(g1,g1) = 6.5
    c: Symmetric(g1,g1,g0)
    c: Diameter(g2) = 3.2
    c: Diameter(g3) = 3.2
    c: Coincident(g2,g1)
    c: Coincident(g3,g1)
FEATURE [Sketcher::SketchObject] Sketch032  label="spazio per PILA 18650"
  ArcFitTolerance = 1e-06
  AttachmentSupport = -> [XY_Plane]
  ExternalGeometry = -> [Sketch]
  FullyConstrained = true
  MakeInternals = false
  MapMode = 5
  sketch-geometry (2):
    g0: LineSegment [constr] StartX=-178.142 StartY=-1.74e-14 StartZ=0 EndX=-191.142 EndY=-1.83e-14 EndZ=0
    g1: Circle CenterX=-191.142 CenterY=-1.83e-14 CenterZ=0 NormalX=0 NormalY=0 NormalZ=1 AngleXU=0 Radius=10.5
  constraints (5):
    c: Distance(g0) = 13
    c: Coincident(g0,g-3)
    c: PointOnObject(g0,g-4)
    c: Diameter(g1) = 21
    c: Coincident(g1,g0)
FEATURE [Part::Extrusion] Extrude030  label="Extrude spazio per PILA 18650"
  Base = -> Sketch032
  Dir = (0,0,1)
  DirLink = -> Sketch [Edge45]
  DirMode = 2
  FaceMakerClass = Part::FaceMakerBullseye
  FaceMakerMode = 3
  LengthFwd = 76
  LengthRev = 0
  Placement = pos=(6,0,-72) rot=(0,0,1;0rad)
  Solid = true
  Symmetric = false
FEATURE [Sketcher::SketchObject] Sketch033  label="fermo per scheda micro"
  ArcFitTolerance = 1e-06
  AttachmentSupport = -> [XZ_Plane]
  ExternalGeometry = -> [Sketch]
  FullyConstrained = true
  MakeInternals = false
  MapMode = 5
  Placement = pos=(0,0,0) rot=(1,0,0;1.5708rad)
  sketch-geometry (12):
    g0: LineSegment StartX=-11.6 StartY=6 StartZ=0 EndX=-4 EndY=6 EndZ=0
    g1: LineSegment StartX=-4 StartY=6 StartZ=0 EndX=-4 EndY=36.4 EndZ=0
    g2: LineSegment StartX=-4 StartY=36.4 StartZ=0 EndX=-11.6 EndY=36.4 EndZ=0
    g3: LineSegment StartX=-11.6 StartY=36.4 StartZ=0 EndX=-11.6 EndY=6 EndZ=0
    g4: LineSegment StartX=-80.11 StartY=11.6 StartZ=0 EndX=-70.51 EndY=11.6 EndZ=0
    g5: LineSegment StartX=-70.51 StartY=11.6 StartZ=0 EndX=-70.51 EndY=6 EndZ=0
    g6: LineSegment StartX=-70.51 StartY=6 StartZ=0 EndX=-80.11 EndY=6 EndZ=0
    g7: LineSegment StartX=-80.11 StartY=6 StartZ=0 EndX=-80.11 EndY=11.6 EndZ=0
    g8: LineSegment StartX=-78.51 StartY=36.4 StartZ=0 EndX=-70.51 EndY=36.4 EndZ=0
    g9: LineSegment StartX=-70.51 StartY=36.4 StartZ=0 EndX=-70.51 EndY=30.8 EndZ=0
    g10: LineSegment StartX=-70.51 StartY=30.8 StartZ=0 EndX=-78.51 EndY=30.8 EndZ=0
    g11: LineSegment StartX=-78.51 StartY=30.8 StartZ=0 EndX=-78.51 EndY=36.4 EndZ=0
  constraints (33):
    c: Horizontal(g0)
    c: Coincident(g1,g0)
    c: Coincident(g2,g1)
    c: Horizontal(g2)
    c: Coincident(g3,g2)
    c: Coincident(g3,g0)
    c: Vertical(g3)
    c: DistanceX(g2,g2) = 7.6
    c: Coincident(g1,g-3)
    c: Coincident(g0,g-3)
    c: Horizontal(g4)
    c: Coincident(g5,g4)
    c: Vertical(g5)
    c: Coincident(g6,g5)
    c: Horizontal(g6)
    c: Coincident(g7,g6)
    c: Coincident(g7,g4)
    c: Vertical(g7)
    c: DistanceY(g5,g5) = 5.6
    c: DistanceX(g4,g4) = 9.6
    c: Coincident(g9,g8)
    c: Vertical(g9)
    c: Coincident(g10,g9)
    c: Horizontal(g10)
    c: Coincident(g11,g10)
    c: Coincident(g11,g8)
    c: Vertical(g11)
    c: DistanceY(g9,g9) = 5.6
    c: DistanceX(g10,g10) = 8
    c: Coincident(g4,g-4)
    c: DistanceX(g4,g10) = 1.6
    c: Horizontal(g8)
    c: DistanceY(g8,g1) = 0
FEATURE [Sketcher::SketchObject] Sketch034  label="buchi guida rail"
  ArcFitTolerance = 1e-06
  AttachmentSupport = -> [XY_Plane]
  ExternalGeometry = -> [Sketch]
  FullyConstrained = true
  MakeInternals = false
  MapMode = 5
  sketch-geometry (6):
    g0: LineSegment [constr] StartX=-100.8 StartY=9.1e-15 StartZ=0 EndX=-93.3 EndY=0 EndZ=0
    g1: LineSegment [constr] StartX=-93.3 StartY=0 StartZ=0 EndX=-73.3 EndY=0 EndZ=0
    g2: LineSegment [constr] StartX=-73.3 StartY=0 StartZ=0 EndX=-53.3 EndY=0 EndZ=0
    g3: Circle CenterX=-93.3 CenterY=0 CenterZ=0 NormalX=0 NormalY=0 NormalZ=1 AngleXU=0 Radius=2.5
    g4: Circle CenterX=-73.3 CenterY=0 CenterZ=0 NormalX=0 NormalY=0 NormalZ=1 AngleXU=0 Radius=2.5
    g5: Circle CenterX=-53.3 CenterY=0 CenterZ=0 NormalX=0 NormalY=0 NormalZ=1 AngleXU=0 Radius=2.5
  constraints (15):
    c: Distance(g0) = 7.5
    c: Coincident(g0,g-3)
    c: PointOnObject(g0,g-1)
    c: Distance(g1) = 20
    c: Coincident(g1,g0)
    c: PointOnObject(g1,g-1)
    c: Distance(g2) = 20
    c: Coincident(g2,g1)
    c: PointOnObject(g2,g-1)
    c: Diameter(g3) = 5
    c: Diameter(g4) = 5
    c: Diameter(g5) = 5
    c: Coincident(g3,g0)
    c: Coincident(g4,g1)
    c: Coincident(g5,g2)
FEATURE [Part::Extrusion] Extrude032  label="Extrude buchi guida rail"
  Base = -> Sketch034
  Dir = (0,0,1)
  DirMode = 2
  FaceMakerClass = Part::FaceMakerBullseye
  FaceMakerMode = 3
  LengthFwd = -6.2
  LengthRev = 0
  Placement = pos=(0,0,43.2) rot=(0,0,1;0rad)
  Solid = true
  Symmetric = false
FEATURE [Part::Extrusion] Extrude033  label="Extrude fori superiori per solenoide e oled001"
  Base = -> Sketch030
  Dir = (0,0,1)
  DirMode = 2
  FaceMakerClass = Part::FaceMakerBullseye
  FaceMakerMode = 3
  LengthFwd = -4.8
  LengthRev = 0
  Placement = pos=(0,0,41.2) rot=(0,0,1;0rad)
  Solid = true
  Symmetric = false
FEATURE [Part::Extrusion] Extrude034  label="Extrude fori sotto impugnatura001"
  Base = -> Sketch029
  Dir = (0,0,1)
  DirMode = 2
  FaceMakerClass = Part::FaceMakerBullseye
  FaceMakerMode = 3
  LengthFwd = 5
  LengthRev = 0
  Placement = pos=(0,0,-83) rot=(0,0,1;0rad)
  Solid = true
  Symmetric = false
FEATURE [Part::Extrusion] Extrude035  label="Extrude fori inferiori switch pompa001"
  Base = -> Sketch031
  Dir = (0,0,1)
  DirMode = 2
  FaceMakerClass = Part::FaceMakerBullseye
  FaceMakerMode = 3
  LengthFwd = 4
  LengthRev = 0
  Placement = pos=(0,0,-1.7) rot=(0,0,1;0rad)
  Solid = true
  Symmetric = false
FEATURE [Part::Extrusion] Extrude036  label="Extrude foro sotto posteriore M3x5x007"
  Base = -> Sketch027
  Dir = (0,0,1)
  DirMode = 2
  FaceMakerClass = Part::FaceMakerBullseye
  FaceMakerMode = 3
  LengthFwd = 6.2
  LengthRev = 0
  Placement = pos=(0,0,-9.6) rot=(0,0,1;0rad)
  Solid = true
  Symmetric = false
FEATURE [Part::Extrusion] Extrude037  label="Extrude foro sotto anteriore M3x5x007"
  Base = -> Sketch026
  Dir = (0,0,1)
  DirMode = 2
  FaceMakerClass = Part::FaceMakerBullseye
  FaceMakerMode = 3
  LengthFwd = 6.2
  LengthRev = 0
  Solid = true
  Symmetric = false
FEATURE [Sketcher::SketchObject] Sketch035  label="foro per fissaggio micro"
  ArcFitTolerance = 1e-06
  AttachmentSupport = -> [XZ_Plane]
  ExternalGeometry = -> [Sketch,Sketch033]
  FullyConstrained = true
  MakeInternals = false
  MapMode = 5
  Placement = pos=(0,0,0) rot=(1,0,0;1.5708rad)
  sketch-geometry (3):
    g0: Circle CenterX=-7.8 CenterY=21.2 CenterZ=0 NormalX=0 NormalY=0 NormalZ=1 AngleXU=0 Radius=1.6
    g1: GeomPoint [constr] X=-4 Y=21.2 Z=0
    g2: LineSegment [constr] StartX=-4 StartY=21.2 StartZ=0 EndX=-11.6 EndY=21.2 EndZ=0
  constraints (6):
    c: Diameter(g0) = 3.2
    c: Symmetric(g-3,g-3,g1)
    c: Coincident(g2,g1)
    c: Horizontal(g2)
    c: DistanceX(g-4,g2) = 0
    c: Symmetric(g2,g1,g0)
FEATURE [Part::Extrusion] Extrude038  label="Extrude foro per fissaggio micro"
  Base = -> Sketch035
  Dir = (0,-1,2e-16)
  DirMode = 2
  FaceMakerClass = Part::FaceMakerBullseye
  FaceMakerMode = 3
  LengthFwd = 3
  LengthRev = 0
  Placement = pos=(0,8.6,0) rot=(0,0,1;0rad)
  Solid = true
  Symmetric = false
FEATURE [Sketcher::SketchObject] Sketch036  label="supporto per alimentatore"
  ArcFitTolerance = 1e-06
  AttachmentSupport = -> [XZ_Plane]
  ExternalGeometry = -> [Sketch,Sketch016,Sketch022]
  FullyConstrained = true
  MakeInternals = false
  MapMode = 5
  Placement = pos=(0,0,0) rot=(1,0,0;1.5708rad)
  sketch-geometry (5):
    g0: LineSegment StartX=-211.843 StartY=-50.0944 StartZ=0 EndX=-211.843 EndY=-80.4316 EndZ=0
    g1: LineSegment StartX=-211.843 StartY=-50.0944 StartZ=0 EndX=-207.775 EndY=-41.3701 EndZ=0
    g2: LineSegment [constr] StartX=-209.443 StartY=-50.0944 StartZ=0 EndX=-209.443 EndY=-80.4316 EndZ=0
    g3: LineSegment StartX=-207.775 StartY=-41.3701 StartZ=0 EndX=-207.775 EndY=-80.4316 EndZ=0
    g4: LineSegment StartX=-211.843 StartY=-80.4316 StartZ=0 EndX=-207.775 EndY=-80.4316 EndZ=0
  constraints (15):
    c: Vertical(g0)
    c: Coincident(g1,g0)
    c: Vertical(g2)
    c: Tangent(g2,g-5)
    c: Coincident(g3,g1)
    c: Vertical(g3)
    c: DistanceY(g-3,g3) = -2
    c: Tangent(g1,g-8)
    c: DistanceY(g-3,g0) = -2
    c: Coincident(g4,g0)
    c: Coincident(g4,g3)
    c: Tangent(g0,g-6)
    c: DistanceY(g-3,g2) = -2
    c: DistanceY(g2,g0) = 0
    c: DistanceX(g-3,g3) = 6.8
FEATURE [Part::Extrusion] Extrude039  label="Extrude039 supporto alimentatore"
  Base = -> Sketch036
  Dir = (0,-1,2e-16)
  DirMode = 2
  FaceMakerClass = Part::FaceMakerBullseye
  FaceMakerMode = 3
  LengthFwd = 25.2
  LengthRev = 0
  Solid = true
  Symmetric = true
FEATURE [Sketcher::SketchObject] Sketch037  label="scavo per alimentatore"
  ArcFitTolerance = 1e-06
  AttachmentSupport = -> [XZ_Plane]
  ExternalGeometry = -> [Sketch036]
  FullyConstrained = true
  MakeInternals = false
  MapMode = 5
  Placement = pos=(0,0,0) rot=(1,0,0;1.5708rad)
  sketch-geometry (4):
    g0: LineSegment StartX=-209.575 StartY=-50.4316 StartZ=0 EndX=-209.575 EndY=-80.4316 EndZ=0
    g1: LineSegment StartX=-209.575 StartY=-50.4316 StartZ=0 EndX=-207.775 EndY=-50.4316 EndZ=0
    g2: LineSegment StartX=-207.775 StartY=-50.4316 StartZ=0 EndX=-207.775 EndY=-80.4316 EndZ=0
    g3: LineSegment StartX=-207.775 StartY=-80.4316 StartZ=0 EndX=-209.575 EndY=-80.4316 EndZ=0
  constraints (11):
    c: Vertical(g0)
    c: Coincident(g1,g0)
    c: Horizontal(g1)
    c: Coincident(g2,g1)
    c: Vertical(g2)
    c: Coincident(g3,g2)
    c: Coincident(g3,g0)
    c: Horizontal(g3)
    c: DistanceX(g1,g1) = 1.8
    c: Coincident(g2,g-3)
    c: DistanceY(g2,g2) = 30
FEATURE [Part::Extrusion] Extrude040  label="Extrude040 scavo alimentatore"
  Base = -> Sketch037
  Dir = (0,-1,2e-16)
  DirMode = 2
  FaceMakerClass = Part::FaceMakerBullseye
  FaceMakerMode = 3
  LengthFwd = 19.5
  LengthRev = 0
  Solid = true
  Symmetric = true
FEATURE [Part::Extrusion] Extrude031  label="Extrude fermo per scheda micro"
  Base = -> Sketch033
  Dir = (0,-1,2e-16)
  DirMode = 2
  FaceMakerClass = Part::FaceMakerBullseye
  FaceMakerMode = 3
  LengthFwd = 3
  LengthRev = 0
  Placement = pos=(0,8.6,0) rot=(0,0,1;0rad)
  Solid = true
  Symmetric = false
FEATURE [Sketcher::SketchObject] Sketch038  label="scavo driver solenoide"
  ArcFitTolerance = 1e-06
  AttachmentSupport = -> [XZ_Plane]
  ExternalGeometry = -> [Sketch,Sketch036]
  FullyConstrained = true
  MakeInternals = false
  MapMode = 5
  Placement = pos=(0,0,0) rot=(1,0,0;1.5708rad)
  sketch-geometry (7):
    g0: LineSegment StartX=-192.222 StartY=-8.0175 StartZ=0 EndX=-194.941 EndY=-6.74965 EndZ=0
    g1: LineSegment StartX=-194.941 StartY=-6.74965 StartZ=0 EndX=-212.269 EndY=-43.9083 EndZ=0
    g2: LineSegment StartX=-192.222 StartY=-8.0175 StartZ=0 EndX=-188.779 EndY=-9.62345 EndZ=0
    g3: LineSegment StartX=-188.779 StartY=-9.62345 StartZ=0 EndX=-205.357 EndY=-45.1761 EndZ=0
    g4: LineSegment StartX=-205.357 StartY=-45.1761 StartZ=0 EndX=-209.55 EndY=-45.1761 EndZ=0
    g5: LineSegment [constr] StartX=-212.269 StartY=-43.9083 StartZ=0 EndX=-209.55 EndY=-45.1761 EndZ=0
    g6: LineSegment StartX=-212.269 StartY=-43.9083 StartZ=0 EndX=-209.55 EndY=-45.1761 EndZ=0
  constraints (20):
    c: Coincident(g1,g0)
    c: Coincident(g3,g2)
    c: Coincident(g4,g3)
    c: Distance(g2) = 3.8
    c: Distance(g1) = 41
    c: Coincident(g5,g1)
    c: Distance(g5) = 3
    c: Perpendicular(g5,g-3)
    c: Parallel(g1,g-3)
    c: Perpendicular(g1,g0)
    c: Distance(g0) = 3
    c: Coincident(g6,g1)
    c: Parallel(g3,g-3)
    c: Perpendicular(g2,g3)
    c: Coincident(g2,g0)
    c: Perpendicular(g-4,g4)
    c: PointOnObject(g5,g-3)
    c: Distance(g-3,g5) = 9.6
    c: Coincident(g4,g5)
    c: Coincident(g6,g4)
FEATURE [Part::Extrusion] Extrude041  label="Extrude scavo driver solenoide"
  Base = -> Sketch038
  Dir = (0,-1,2e-16)
  DirMode = 2
  FaceMakerClass = Part::FaceMakerBullseye
  FaceMakerMode = 3
  LengthFwd = 20.6
  LengthRev = 0
  Solid = true
  Symmetric = true
FEATURE [Sketcher::SketchObject] Sketch039  label="scavo per cavo usb per micro"
  ArcFitTolerance = 1e-06
  AttachmentSupport = -> [XZ_Plane]
  ExternalGeometry = -> [Sketch,Sketch016]
  FullyConstrained = true
  MakeInternals = false
  MapMode = 5
  Placement = pos=(0,0,0) rot=(1,0,0;1.5708rad)
  sketch-geometry (4):
    g0: LineSegment StartX=-82.51 StartY=36.4 StartZ=0 EndX=-74.51 EndY=36.4 EndZ=0
    g1: LineSegment StartX=-74.51 StartY=36.4 StartZ=0 EndX=-74.51 EndY=30.8 EndZ=0
    g2: LineSegment StartX=-74.51 StartY=30.8 StartZ=0 EndX=-82.51 EndY=30.8 EndZ=0
    g3: LineSegment StartX=-82.51 StartY=30.8 StartZ=0 EndX=-82.51 EndY=36.4 EndZ=0
  constraints (11):
    c: Coincident(g1,g0)
    c: Vertical(g1)
    c: Coincident(g2,g1)
    c: Horizontal(g2)
    c: Coincident(g3,g2)
    c: Coincident(g3,g0)
    c: Vertical(g3)
    c: Tangent(g0,g-3)
    c: Tangent(g2,g-4)
    c: Tangent(g3,g-4)
    c: Tangent(g1,g-4)
FEATURE [Part::Extrusion] Extrude042  label="Extrude scavo per cavo usb per micro"
  Base = -> Sketch039
  Dir = (0,-1,2e-16)
  DirMode = 2
  FaceMakerClass = Part::FaceMakerBullseye
  FaceMakerMode = 3
  LengthFwd = 11.2
  LengthRev = 0
  Solid = true
  Symmetric = true
FEATURE [Sketcher::SketchObject] Sketch040  label="scavo saldature alimentatore connettore 5v"
  ArcFitTolerance = 1e-06
  AttachmentSupport = -> [XZ_Plane]
  ExternalGeometry = -> [Sketch037]
  FullyConstrained = true
  MakeInternals = false
  MapMode = 5
  Placement = pos=(0,0,0) rot=(1,0,0;1.5708rad)
  sketch-geometry (4):
    g0: LineSegment StartX=-211.175 StartY=-52.4316 StartZ=0 EndX=-211.175 EndY=-56.4316 EndZ=0
    g1: LineSegment StartX=-211.175 StartY=-52.4316 StartZ=0 EndX=-209.575 EndY=-52.4316 EndZ=0
    g2: LineSegment StartX=-209.575 StartY=-52.4316 StartZ=0 EndX=-209.575 EndY=-56.4316 EndZ=0
    g3: LineSegment StartX=-209.575 StartY=-56.4316 StartZ=0 EndX=-211.175 EndY=-56.4316 EndZ=0
  constraints (11):
    c: Vertical(g0)
    c: Coincident(g1,g0)
    c: Horizontal(g1)
    c: Coincident(g2,g1)
    c: Coincident(g3,g2)
    c: Coincident(g3,g0)
    c: Horizontal(g3)
    c: DistanceX(g1,g1) = 1.6
    c: DistanceY(g2,g2) = 4
    c: Tangent(g2,g-3)
    c: DistanceY(g1,g-3) = 2
FEATURE [Part::Extrusion] Extrude043  label="Extrude scavo saldature alimentatore connettore 5v"
  Base = -> Sketch040
  Dir = (0,-1,2e-16)
  DirMode = 2
  FaceMakerClass = Part::FaceMakerBullseye
  FaceMakerMode = 3
  LengthFwd = 8
  LengthRev = 0
  Solid = true
  Symmetric = true
FEATURE [Sketcher::SketchObject] Sketch041  label="scavo saldature alimentatore connettore 5v verticali"
  ArcFitTolerance = 1e-06
  AttachmentSupport = -> [XZ_Plane]
  ExternalGeometry = -> [Sketch037]
  FullyConstrained = true
  MakeInternals = false
  MapMode = 5
  Placement = pos=(0,0,0) rot=(1,0,0;1.5708rad)
  sketch-geometry (4):
    g0: LineSegment StartX=-211.175 StartY=-53.6316 StartZ=0 EndX=-209.575 EndY=-53.6316 EndZ=0
    g1: LineSegment StartX=-209.575 StartY=-53.6316 StartZ=0 EndX=-209.575 EndY=-76.6316 EndZ=0
    g2: LineSegment StartX=-209.575 StartY=-76.6316 StartZ=0 EndX=-211.175 EndY=-76.6316 EndZ=0
    g3: LineSegment StartX=-211.175 StartY=-76.6316 StartZ=0 EndX=-211.175 EndY=-53.6316 EndZ=0
  constraints (11):
    c: Horizontal(g0)
    c: Coincident(g1,g0)
    c: Coincident(g2,g1)
    c: Horizontal(g2)
    c: Coincident(g3,g2)
    c: Coincident(g3,g0)
    c: Vertical(g3)
    c: DistanceY(g3,g3) = 23
    c: DistanceX(g0,g0) = 1.6
    c: Tangent(g1,g-3)
    c: DistanceY(g0,g-3) = 3.2
FEATURE [Part::Extrusion] Extrude044  label="Extrude scavo saldature alimentatore connettore 5v verticali"
  Base = -> Sketch041
  Dir = (0,-1,2e-16)
  DirMode = 2
  FaceMakerClass = Part::FaceMakerBullseye
  FaceMakerMode = 3
  LengthFwd = 3.2
  LengthRev = 0
  Placement = pos=(0,8.3,0) rot=(0,0,1;0rad)
  Solid = true
  Symmetric = false
FEATURE [Sketcher::SketchObject] Sketch042  label="fermi per driver solenoide e alimentatore"
  ArcFitTolerance = 1e-06
  AttachmentSupport = -> [XZ_Plane]
  ExternalGeometry = -> [Sketch036,Sketch037,Sketch,Sketch038]
  FullyConstrained = true
  MakeInternals = false
  MapMode = 5
  Placement = pos=(0,0,0) rot=(1,0,0;1.5708rad)
  sketch-geometry (27):
    g0: LineSegment StartX=-200.506 StartY=-25.7811 StartZ=0 EndX=-201.436 EndY=-27.775 EndZ=0
    g1: LineSegment StartX=-201.436 StartY=-27.775 StartZ=0 EndX=-199.442 EndY=-28.7048 EndZ=0
    g2: LineSegment StartX=-199.442 StartY=-28.7048 StartZ=0 EndX=-198.512 EndY=-26.7109 EndZ=0
    g3: LineSegment StartX=-198.512 StartY=-26.7109 StartZ=0 EndX=-200.506 EndY=-25.7811 EndZ=0
    g4: LineSegment StartX=-201.28 StartY=-23.6549 StartZ=0 EndX=-203.562 EndY=-28.5489 EndZ=0
    g5: LineSegment StartX=-203.562 StartY=-28.5489 StartZ=0 EndX=-200.118 EndY=-30.1549 EndZ=0
    g6: LineSegment StartX=-197.992 StartY=-29.381 StartZ=0 EndX=-197.062 EndY=-27.3871 EndZ=0
    g7: LineSegment StartX=-197.836 StartY=-25.2608 StartZ=0 EndX=-201.28 EndY=-23.6549 EndZ=0
    g8: LineSegment [constr] StartX=-198.668 StartY=-30.8311 StartZ=0 EndX=-197.992 EndY=-29.381 EndZ=0
    g9: LineSegment [constr] StartX=-198.668 StartY=-30.8311 StartZ=0 EndX=-200.118 EndY=-30.1549 EndZ=0
    g10: ArcOfCircle CenterX=-198.512 CenterY=-26.7109 CenterZ=0 NormalX=0 NormalY=0 NormalZ=1 AngleXU=0 Radius=1.6 StartAngle=5.84685 EndAngle=7.41765
    g11: GeomPoint [constr] X=-196.386 Y=-25.937 Z=0
    g12: ArcOfCircle CenterX=-199.442 CenterY=-28.7048 CenterZ=0 NormalX=0 NormalY=0 NormalZ=1 AngleXU=0 Radius=1.6 StartAngle=4.27606 EndAngle=5.84685
    g13: GeomPoint [constr] X=-198.668 Y=-30.8311 Z=0
    g14: LineSegment StartX=-207.775 StartY=-46.8316 StartZ=0 EndX=-207.775 EndY=-50.8316 EndZ=0
    g15: LineSegment StartX=-207.775 StartY=-46.8316 StartZ=0 EndX=-203.775 EndY=-46.8316 EndZ=0
    g16: LineSegment StartX=-203.775 StartY=-46.8316 StartZ=0 EndX=-203.775 EndY=-50.8316 EndZ=0
    g17: LineSegment StartX=-207.775 StartY=-50.8316 StartZ=0 EndX=-203.775 EndY=-50.8316 EndZ=0
    g18: LineSegment StartX=-209.375 StartY=-52.4316 StartZ=0 EndX=-203.775 EndY=-52.4316 EndZ=0
    g19: LineSegment StartX=-202.175 StartY=-50.8316 StartZ=0 EndX=-202.175 EndY=-46.8316 EndZ=0
    g20: LineSegment StartX=-203.775 StartY=-45.2316 StartZ=0 EndX=-209.375 EndY=-45.2316 EndZ=0
    g21: LineSegment StartX=-209.375 StartY=-45.2316 StartZ=0 EndX=-209.375 EndY=-52.4316 EndZ=0
    g22: ArcOfCircle CenterX=-203.775 CenterY=-46.8316 CenterZ=0 NormalX=0 NormalY=0 NormalZ=1 AngleXU=0 Radius=1.6 StartAngle=1.8e-15 EndAngle=1.5708
    g23: GeomPoint [constr] X=-202.175 Y=-45.2316 Z=0
    g24: ArcOfCircle CenterX=-203.775 CenterY=-50.8316 CenterZ=0 NormalX=0 NormalY=0 NormalZ=1 AngleXU=0 Radius=1.6 StartAngle=4.71239 EndAngle=6.28319
    g25: GeomPoint [constr] X=-202.175 Y=-52.4316 Z=0
    g26: LineSegment [constr] StartX=-207.775 StartY=-50.4316 StartZ=0 EndX=-207.775 EndY=-50.8316 EndZ=0
  constraints (69):
    c: Coincident(g1,g0)
    c: Coincident(g2,g1)
    c: Coincident(g3,g2)
    c: Coincident(g3,g0)
    c: Parallel(g0,g2)
    c: Perpendicular(g3,g0)
    c: Perpendicular(g1,g0)
    c: Coincident(g5,g4)
    c: Coincident(g7,g4)
    c: Distance(g3) = 2.2
    c: Distance(g2) = 2.2
    c: Parallel(g6,g2)
    c: Parallel(g6,g4)
    c: Perpendicular(g5,g6)
    c: Perpendicular(g7,g6)
    c: Distance(g13,g11) = 5.4
    c: Distance(g5,g13) = 5.4
    c: Coincident(g9,g8)
    c: Distance(g8) = 1.6
    c: Distance(g9) = 1.6
    c: Perpendicular(g9,g8)
    c: Parallel(g8,g6)
    c: Coincident(g8,g13)
    c: Distance(g8,g1) = 1.6
    c: Distance(g9,g1) = 1.6
    c: Tangent(g0,g-5)
    c: Distance(g0,g-6) = 19.2
    c: PointOnObject(g11,g7)
    c: PointOnObject(g11,g6)
    c: Tangent(g7,g10) = -1.5708
    c: Tangent(g6,g10) = -1.5708
    c: PointOnObject(g13,g5)
    c: Tangent(g5,g12) = -1.5708
    c: Tangent(g6,g12) = -1.5708
    c: Equal(g10,g12)
    c: Coincident(g10,g2)
    c: Vertical(g14)
    c: Coincident(g15,g14)
    c: Horizontal(g15)
    c: Coincident(g16,g15)
    c: Vertical(g16)
    c: Coincident(g17,g14)
    c: Coincident(g17,g16)
    c: Horizontal(g17)
    c: Distance(g16) = 4
    c: Distance(g15) = 4
    c: Horizontal(g18)
    c: Vertical(g19)
    c: Horizontal(g20)
    c: Coincident(g21,g20)
    c: Coincident(g21,g18)
    c: Vertical(g21)
    c: Distance(g20,g23) = 7.2
    c: Distance(g25,g23) = 7.2
    c: DistanceY(g18,g14) = 1.6
    c: DistanceX(g18,g14) = 1.6
    c: PointOnObject(g23,g20)
    c: PointOnObject(g23,g19)
    c: Tangent(g20,g22) = -1.5708
    c: Tangent(g19,g22) = -1.5708
    c: PointOnObject(g25,g19)
    c: Tangent(g18,g24) = -1.5708
    c: Tangent(g19,g24) = -1.5708
    c: Equal(g22,g24)
    c: Coincident(g22,g15)
    c: Vertical(g26)
    c: Distance(g26) = 0.4
    c: Coincident(g26,g-4)
    c: Coincident(g14,g26)
FEATURE [Part::Extrusion] Extrude045  label="Extrude fermi per driver solenoide e alimentatore"
  Base = -> Sketch042
  Dir = (0,-1,2e-16)
  DirMode = 2
  FaceMakerClass = Part::FaceMakerBullseye
  FaceMakerMode = 3
  LengthFwd = 25.2
  LengthRev = 0
  Solid = true
  Symmetric = true
FEATURE [Sketcher::SketchObject] Sketch043  label="scavo pulizia fermo alimentatore"
  ArcFitTolerance = 1e-06
  AttachmentSupport = -> [XZ_Plane]
  ExternalGeometry = -> [Sketch042,Sketch036,Sketch037]
  FullyConstrained = true
  MakeInternals = false
  MapMode = 5
  Placement = pos=(0,0,0) rot=(1,0,0;1.5708rad)
  sketch-geometry (6):
    g0: LineSegment StartX=-209.375 StartY=-52.4316 StartZ=0 EndX=-209.375 EndY=-50.4316 EndZ=0
    g1: LineSegment StartX=-209.375 StartY=-50.4316 StartZ=0 EndX=-207.775 EndY=-50.4316 EndZ=0
    g2: LineSegment StartX=-207.775 StartY=-50.4316 StartZ=0 EndX=-207.775 EndY=-45.2316 EndZ=0
    g3: LineSegment StartX=-207.775 StartY=-45.2316 StartZ=0 EndX=-202.175 EndY=-45.2316 EndZ=0
    g4: LineSegment StartX=-202.175 StartY=-45.2316 StartZ=0 EndX=-202.175 EndY=-52.4316 EndZ=0
    g5: LineSegment StartX=-202.175 StartY=-52.4316 StartZ=0 EndX=-209.375 EndY=-52.4316 EndZ=0
  constraints (13):
    c: Vertical(g0)
    c: Coincident(g1,g0)
    c: Coincident(g2,g1)
    c: Coincident(g3,g2)
    c: Coincident(g4,g3)
    c: Coincident(g5,g4)
    c: Coincident(g5,g0)
    c: Horizontal(g5)
    c: Coincident(g0,g-6)
    c: Tangent(g1,g-8)
    c: Tangent(g2,g-4)
    c: Tangent(g3,g-7)
    c: Tangent(g4,g-3)
FEATURE [Part::Extrusion] Extrude046  label="Extrude scavo pulizia fermo alimentatore"
  Base = -> Sketch043
  Dir = (0,-1,2e-16)
  DirMode = 2
  FaceMakerClass = Part::FaceMakerBullseye
  FaceMakerMode = 3
  LengthFwd = 19.5
  LengthRev = 0
  Solid = true
  Symmetric = true
FEATURE [Sketcher::SketchObject] Sketch044  label="buchini per fissaggio oled"
  ArcFitTolerance = 1e-06
  AttachmentSupport = -> [YZ_Plane]
  ExternalGeometry = -> [Sketch]
  FullyConstrained = true
  MakeInternals = false
  MapMode = 5
  Placement = pos=(0,0,0) rot=(0.57735,0.57735,0.57735;2.0944rad)
  sketch-geometry (5):
    g0: LineSegment [constr] StartX=1.5e-14 StartY=67.3588 StartZ=0 EndX=0 EndY=64.3588 EndZ=0
    g1: LineSegment [constr] StartX=0 StartY=64.3588 StartZ=0 EndX=10.4 EndY=64.3588 EndZ=0
    g2: LineSegment [constr] StartX=0 StartY=64.3588 StartZ=0 EndX=-10.4 EndY=64.3588 EndZ=0
    g3: Circle CenterX=10.4 CenterY=64.3588 CenterZ=0 NormalX=0 NormalY=0 NormalZ=1 AngleXU=0 Radius=1.5
    g4: Circle CenterX=-10.4 CenterY=64.3588 CenterZ=0 NormalX=0 NormalY=0 NormalZ=1 AngleXU=0 Radius=1.5
  constraints (13):
    c: Distance(g0) = 3
    c: PointOnObject(g0,g-2)
    c: Coincident(g1,g0)
    c: Horizontal(g1)
    c: Coincident(g2,g0)
    c: Horizontal(g2)
    c: DistanceX(g1,g1) = 10.4
    c: Coincident(g3,g1)
    c: Diameter(g4) = 3
    c: Coincident(g4,g2)
    c: Coincident(g0,g-7)
    c: Equal(g1,g2)
    c: Equal(g4,g3)
FEATURE [Part::Extrusion] Extrude047  label="Extrude buchini per fissaggio oled"
  Base = -> Sketch044
  Dir = (1,0,0)
  DirMode = 2
  FaceMakerClass = Part::FaceMakerBullseye
  FaceMakerMode = 3
  LengthFwd = 10
  LengthRev = 0
  Placement = pos=(-186,0,0) rot=(0,0,1;0rad)
  Solid = true
  Symmetric = false
FEATURE [Sketcher::SketchObject] Sketch046  label="scavo 5x5 neopixel"
  ArcFitTolerance = 1e-06
  AttachmentSupport = -> [YZ_Plane002]
  FullyConstrained = true
  MakeInternals = false
  MapMode = 5
  Placement = pos=(0,0,0) rot=(0.57735,0.57735,0.57735;2.0944rad)
  sketch-geometry (4):
    g0: LineSegment StartX=-2.7 StartY=2.7 StartZ=0 EndX=2.7 EndY=2.7 EndZ=0
    g1: LineSegment StartX=2.7 StartY=2.7 StartZ=0 EndX=2.7 EndY=-2.7 EndZ=0
    g2: LineSegment StartX=2.7 StartY=-2.7 StartZ=0 EndX=-2.7 EndY=-2.7 EndZ=0
    g3: LineSegment StartX=-2.7 StartY=-2.7 StartZ=0 EndX=-2.7 EndY=2.7 EndZ=0
  constraints (11):
    c: Horizontal(g0)
    c: Coincident(g1,g0)
    c: Vertical(g1)
    c: Coincident(g2,g1)
    c: Horizontal(g2)
    c: Coincident(g3,g2)
    c: Coincident(g3,g0)
    c: Vertical(g3)
    c: DistanceX(g0,g0) = 5.4
    c: DistanceY(g1,g1) = 5.4
    c: Symmetric(g0,g1,g-1)
FEATURE [Sketcher::SketchObject] Sketch047  label="scavo 10x10 neopixel corpo"
  ArcFitTolerance = 1e-06
  AttachmentOffset = pos=(0,0,1) rot=(0,0,1;0rad)
  AttachmentSupport = -> [YZ_Plane002]
  FullyConstrained = true
  MakeInternals = false
  MapMode = 5
  Placement = pos=(1,0,0) rot=(0.57735,0.57735,0.57735;2.0944rad)
  sketch-geometry (4):
    g0: LineSegment StartX=-5 StartY=5.1 StartZ=0 EndX=5 EndY=5.1 EndZ=0
    g1: LineSegment StartX=5 StartY=5.1 StartZ=0 EndX=5 EndY=-5.1 EndZ=0
    g2: LineSegment StartX=5 StartY=-5.1 StartZ=0 EndX=-5 EndY=-5.1 EndZ=0
    g3: LineSegment StartX=-5 StartY=-5.1 StartZ=0 EndX=-5 EndY=5.1 EndZ=0
  constraints (11):
    c: Horizontal(g0)
    c: Coincident(g1,g0)
    c: Vertical(g1)
    c: Coincident(g2,g1)
    c: Horizontal(g2)
    c: Coincident(g3,g2)
    c: Coincident(g3,g0)
    c: Vertical(g3)
    c: DistanceX(g0,g0) = 10
    c: DistanceY(g1,g1) = 10.2
    c: Symmetric(g0,g2,g-1)
FEATURE [Sketcher::SketchObject] Sketch048  label="buco per perno blocco neopixel"
  ArcFitTolerance = 1e-06
  AttachmentSupport = -> [XZ_Plane002]
  FullyConstrained = true
  MakeInternals = false
  MapMode = 5
  Placement = pos=(0,0,0) rot=(1,0,0;1.5708rad)
  sketch-geometry (4):
    g0: LineSegment StartX=3 StartY=1.2 StartZ=0 EndX=3 EndY=-1.2 EndZ=0
    g1: LineSegment StartX=3 StartY=-1.2 StartZ=0 EndX=5.4 EndY=-1.2 EndZ=0
    g2: LineSegment StartX=5.4 StartY=-1.2 StartZ=0 EndX=5.4 EndY=1.2 EndZ=0
    g3: LineSegment StartX=5.4 StartY=1.2 StartZ=0 EndX=3 EndY=1.2 EndZ=0
  constraints (11):
    c: Coincident(g1,g0)
    c: Horizontal(g1)
    c: Coincident(g2,g1)
    c: Vertical(g2)
    c: Coincident(g3,g2)
    c: Coincident(g3,g0)
    c: Horizontal(g3)
    c: DistanceX(g1,g1) = 2.4
    c: DistanceY(g2,g2) = 2.4
    c: Symmetric(g0,g0,g-1)
    c: DistanceX(g-1,g0) = 3
FEATURE [Sketcher::SketchObject] Sketch045  label="blocco principale per neopixel"
  ArcFitTolerance = 1e-06
  AttachmentSupport = -> [XZ_Plane002]
  ExternalGeometry = -> [Sketch048]
  FullyConstrained = true
  MakeInternals = false
  MapMode = 5
  Placement = pos=(0,0,0) rot=(1,0,0;1.5708rad)
  sketch-geometry (6):
    g0: LineSegment StartX=0 StartY=5.1 StartZ=0 EndX=0 EndY=-5.1 EndZ=0
    g1: LineSegment StartX=0 StartY=-5.1 StartZ=0 EndX=3 EndY=-5.1 EndZ=0
    g2: LineSegment StartX=7 StartY=-1.1 StartZ=0 EndX=7 EndY=5.1 EndZ=0
    g3: LineSegment StartX=7 StartY=5.1 StartZ=0 EndX=0 EndY=5.1 EndZ=0
    g4: ArcOfCircle CenterX=3 CenterY=-1.1 CenterZ=0 NormalX=0 NormalY=0 NormalZ=1 AngleXU=0 Radius=4 StartAngle=4.71239 EndAngle=6.28319
    g5: GeomPoint [constr] X=7 Y=-5.1 Z=0
  constraints (15):
    c: Vertical(g0)
    c: Coincident(g1,g0)
    c: Horizontal(g1)
    c: Vertical(g2)
    c: Coincident(g3,g2)
    c: Coincident(g3,g0)
    c: Horizontal(g3)
    c: DistanceY(g0,g0) = 10.2
    c: Symmetric(g0,g0,g-1)
    c: DistanceX(g3,g3) = 7
    c: PointOnObject(g5,g2)
    c: PointOnObject(g5,g1)
    c: Tangent(g2,g4) = -1.5708
    c: Tangent(g1,g4) = -1.5708
    c: DistanceX(g-3,g1) = 0
FEATURE [Sketcher::SketchObject] Sketch049  label="rinforzi esterni per corpo neopoixel"
  ArcFitTolerance = 1e-06
  AttachmentSupport = -> [XZ_Plane002]
  ExternalGeometry = -> [Sketch045]
  FullyConstrained = true
  MakeInternals = false
  MapMode = 5
  Placement = pos=(0,0,0) rot=(1,0,0;1.5708rad)
  sketch-geometry (8):
    g0: LineSegment StartX=1 StartY=-4.1 StartZ=0 EndX=2 EndY=-4.1 EndZ=0
    g1: LineSegment StartX=2 StartY=-4.1 StartZ=0 EndX=2 EndY=-5.1 EndZ=0
    g2: LineSegment StartX=2 StartY=-5.1 StartZ=0 EndX=1 EndY=-5.1 EndZ=0
    g3: LineSegment StartX=1 StartY=-5.1 StartZ=0 EndX=1 EndY=-4.1 EndZ=0
    g4: LineSegment StartX=1 StartY=5.1 StartZ=0 EndX=2 EndY=5.1 EndZ=0
    g5: LineSegment StartX=2 StartY=5.1 StartZ=0 EndX=2 EndY=4.1 EndZ=0
    g6: LineSegment StartX=2 StartY=4.1 StartZ=0 EndX=1 EndY=4.1 EndZ=0
    g7: LineSegment StartX=1 StartY=4.1 StartZ=0 EndX=1 EndY=5.1 EndZ=0
  constraints (24):
    c: Horizontal(g0)
    c: Coincident(g1,g0)
    c: Vertical(g1)
    c: Coincident(g2,g1)
    c: Horizontal(g2)
    c: Coincident(g3,g2)
    c: Coincident(g3,g0)
    c: Vertical(g3)
    c: Horizontal(g4)
    c: Coincident(g5,g4)
    c: Vertical(g5)
    c: Coincident(g6,g5)
    c: Horizontal(g6)
    c: Coincident(g7,g6)
    c: Coincident(g7,g4)
    c: Vertical(g7)
    c: DistanceX(g4,g4) = 1
    c: DistanceY(g5,g5) = 1
    c: DistanceX(g0,g0) = 1
    c: DistanceY(g1,g1) = 1
    c: DistanceX(g-3,g4) = 1
    c: DistanceY(g-3,g4) = 0
    c: DistanceX(g-4,g2) = 1
    c: DistanceY(g2,g-4) = 0
FEATURE [Sketcher::SketchObject] Sketch052  label="scavo saldature driver solenoide"
  ArcFitTolerance = 1e-06
  AttachmentSupport = -> [XZ_Plane]
  ExternalGeometry = -> [Sketch038]
  FullyConstrained = true
  MakeInternals = false
  MapMode = 5
  Placement = pos=(0,0,0) rot=(1,0,0;1.5708rad)
  sketch-geometry (4):
    g0: LineSegment StartX=-195.304 StartY=-6.5806 StartZ=0 EndX=-196.994 EndY=-10.2058 EndZ=0
    g1: LineSegment StartX=-196.994 StartY=-10.2058 StartZ=0 EndX=-196.632 EndY=-10.3749 EndZ=0
    g2: LineSegment StartX=-196.632 StartY=-10.3749 StartZ=0 EndX=-194.941 EndY=-6.74965 EndZ=0
    g3: LineSegment StartX=-194.941 StartY=-6.74965 StartZ=0 EndX=-195.304 EndY=-6.5806 EndZ=0
  constraints (11):
    c: Coincident(g1,g0)
    c: Coincident(g2,g1)
    c: Coincident(g3,g2)
    c: Coincident(g3,g0)
    c: Parallel(g2,g0)
    c: Perpendicular(g2,g3)
    c: Perpendicular(g1,g2,g1) = 1.5708
    c: Parallel(g2,g-3)
    c: Distance(g2) = 4
    c: Distance(g3) = 0.4
    c: Coincident(g2,g-3)
FEATURE [Part::Extrusion] Extrude055  label="Extrude scavo saldature driver solenoide"
  Base = -> Sketch052
  Dir = (0,-1,2e-16)
  DirMode = 2
  FaceMakerClass = Part::FaceMakerBullseye
  FaceMakerMode = 3
  LengthFwd = 6
  LengthRev = 0
  Solid = true
  Symmetric = true
FEATURE [Sketcher::SketchObject] Sketch053  label="scavo saldature rumble"
  ArcFitTolerance = 1e-06
  AttachmentSupport = -> [XZ_Plane]
  ExternalGeometry = -> [Sketch019]
  FullyConstrained = true
  MakeInternals = false
  MapMode = 5
  Placement = pos=(0,0,0) rot=(1,0,0;1.5708rad)
  sketch-geometry (4):
    g0: LineSegment StartX=-164.507 StartY=-41.6446 StartZ=0 EndX=-165.743 EndY=-45.4488 EndZ=0
    g1: LineSegment StartX=-165.743 StartY=-45.4488 StartZ=0 EndX=-164.602 EndY=-45.8196 EndZ=0
    g2: LineSegment StartX=-164.602 StartY=-45.8196 StartZ=0 EndX=-163.366 EndY=-42.0154 EndZ=0
    g3: LineSegment StartX=-163.366 StartY=-42.0154 StartZ=0 EndX=-164.507 EndY=-41.6446 EndZ=0
  constraints (11):
    c: Coincident(g1,g0)
    c: Coincident(g2,g1)
    c: Coincident(g3,g2)
    c: Coincident(g3,g0)
    c: Parallel(g0,g2)
    c: Perpendicular(g3,g0)
    c: Perpendicular(g1,g0)
    c: Parallel(g0,g-3)
    c: Distance(g0) = 4
    c: Distance(g1) = 1.2
    c: Coincident(g0,g-3)
FEATURE [Part::Extrusion] Extrude056  label="Extrude scavo saldature rumble"
  Base = -> Sketch053
  Dir = (0,-1,2e-16)
  DirMode = 2
  FaceMakerClass = Part::FaceMakerBullseye
  FaceMakerMode = 3
  LengthFwd = 8.4
  LengthRev = 0
  Solid = true
  Symmetric = true
FEATURE [Sketcher::SketchObject] Sketch054  label="scavo saldature alimentatore connettore USB"
  ArcFitTolerance = 1e-06
  AttachmentSupport = -> [XZ_Plane]
  ExternalGeometry = -> [Sketch037]
  FullyConstrained = true
  MakeInternals = false
  MapMode = 5
  Placement = pos=(0,0,0) rot=(1,0,0;1.5708rad)
  sketch-geometry (4):
    g0: LineSegment StartX=-209.575 StartY=-80.4316 StartZ=0 EndX=-210.375 EndY=-80.4316 EndZ=0
    g1: LineSegment StartX=-210.375 StartY=-80.4316 StartZ=0 EndX=-210.375 EndY=-72.4316 EndZ=0
    g2: LineSegment StartX=-210.375 StartY=-72.4316 StartZ=0 EndX=-209.575 EndY=-72.4316 EndZ=0
    g3: LineSegment StartX=-209.575 StartY=-72.4316 StartZ=0 EndX=-209.575 EndY=-80.4316 EndZ=0
  constraints (11):
    c: Horizontal(g0)
    c: Coincident(g1,g0)
    c: Vertical(g1)
    c: Coincident(g2,g1)
    c: Horizontal(g2)
    c: Coincident(g3,g2)
    c: Coincident(g3,g0)
    c: Vertical(g3)
    c: DistanceX(g0,g0) = 0.8
    c: DistanceY(g3,g3) = 8
    c: Coincident(g0,g-4)
FEATURE [Part::Extrusion] Extrude057  label="Extrude scavo saldature alimentatore connettore USB"
  Base = -> Sketch054
  Dir = (0,-1,2e-16)
  DirMode = 2
  FaceMakerClass = Part::FaceMakerBullseye
  FaceMakerMode = 3
  LengthFwd = 11
  LengthRev = 0
  Solid = true
  Symmetric = true
FEATURE [Sketcher::SketchObject] Sketch055  label="buco interno per micro switch"
  ArcFitTolerance = 1e-06
  AttachmentSupport = -> [XZ_Plane]
  ExternalGeometry = -> [Sketch]
  FullyConstrained = true
  MakeInternals = false
  MapMode = 5
  Placement = pos=(0,0,0) rot=(1,0,0;1.5708rad)
  sketch-geometry (11):
    g0: LineSegment [constr] StartX=-194.483 StartY=34.2854 StartZ=0 EndX=-196.022 EndY=30.0568 EndZ=0
    g1: LineSegment [constr] StartX=-196.022 StartY=30.0568 StartZ=0 EndX=-197.561 EndY=25.8282 EndZ=0
    g2: LineSegment [constr] StartX=-196.022 StartY=30.0568 StartZ=0 EndX=-194.143 EndY=29.3727 EndZ=0
    g3: LineSegment [constr] StartX=-196.022 StartY=30.0568 StartZ=0 EndX=-197.902 EndY=30.7408 EndZ=0
    g4: LineSegment StartX=-196.362 StartY=34.9694 StartZ=0 EndX=-192.604 EndY=33.6014 EndZ=0
    g5: LineSegment StartX=-199.441 StartY=26.5122 StartZ=0 EndX=-195.682 EndY=25.1441 EndZ=0
    g6: LineSegment StartX=-192.604 StartY=33.6014 StartZ=0 EndX=-195.682 EndY=25.1441 EndZ=0
    g7: LineSegment StartX=-196.362 StartY=34.9694 StartZ=0 EndX=-199.441 EndY=26.5122 EndZ=0
    g8: GeomPoint [constr] X=-187.821 Y=29.2 Z=0
    g9: LineSegment [constr] StartX=-188.505 StartY=27.3206 StartZ=0 EndX=-196.022 EndY=30.0568 EndZ=0
    g10: LineSegment [constr] StartX=-187.821 StartY=29.2 StartZ=0 EndX=-188.505 EndY=27.3206 EndZ=0
  constraints (27):
    c: Coincident(g2,g0)
    c: Parallel(g0,g-3)
    c: Tangent(g1,g0) = -1.5708
    c: Perpendicular(g0,g2)
    c: Tangent(g2,g3)
    c: Distance(g0,g1) = 9
    c: Equal(g0,g1)
    c: Distance(g3,g2) = 4
    c: Equal(g2,g3)
    c: Parallel(g3,g4)
    c: Symmetric(g4,g4,g0)
    c: Parallel(g6,g1)
    c: Parallel(g7,g1)
    c: Symmetric(g6,g6,g2)
    c: Symmetric(g5,g5,g1)
    c: Symmetric(g7,g7,g3)
    c: Coincident(g7,g4)
    c: Coincident(g6,g4)
    c: Coincident(g5,g6)
    c: Symmetric(g-3,g-3,g8)
    c: Perpendicular(g-3,g9)
    c: Distance(g9) = 8
    c: Coincident(g3,g9)
    c: Coincident(g10,g8)
    c: Parallel(g10,g-3)
    c: Distance(g10) = 2
    c: Coincident(g10,g9)
FEATURE [Sketcher::SketchObject] Sketch056  label="buco esterno per micro switch"
  ArcFitTolerance = 1e-06
  AttachmentSupport = -> [XZ_Plane]
  ExternalGeometry = -> [Sketch055]
  FullyConstrained = true
  MakeInternals = false
  MapMode = 5
  Placement = pos=(0,0,0) rot=(1,0,0;1.5708rad)
  sketch-geometry (17):
    g0: GeomPoint [constr] X=-194.143 Y=29.3727 Z=0
    g1: GeomPoint [constr] X=-194.483 Y=34.2854 Z=0
    g2: GeomPoint [constr] X=-197.902 Y=30.7408 Z=0
    g3: GeomPoint [constr] X=-197.561 Y=25.8282 Z=0
    g4: GeomPoint [constr] X=-196.022 Y=30.0568 Z=0
    g5: LineSegment [constr] StartX=-194.483 StartY=34.2854 StartZ=0 EndX=-196.022 EndY=30.0568 EndZ=0
    g6: LineSegment [constr] StartX=-196.022 StartY=30.0568 StartZ=0 EndX=-197.561 EndY=25.8282 EndZ=0
    g7: LineSegment [constr] StartX=-197.902 StartY=30.7408 StartZ=0 EndX=-196.022 EndY=30.0568 EndZ=0
    g8: LineSegment [constr] StartX=-196.022 StartY=30.0568 StartZ=0 EndX=-194.143 EndY=29.3727 EndZ=0
    g9: LineSegment [constr] StartX=-195.338 StartY=31.9362 StartZ=0 EndX=-196.022 EndY=30.0568 EndZ=0
    g10: LineSegment [constr] StartX=-196.022 StartY=30.0568 StartZ=0 EndX=-196.706 EndY=28.1774 EndZ=0
    g11: LineSegment [constr] StartX=-196.022 StartY=30.0568 StartZ=0 EndX=-196.821 EndY=30.3475 EndZ=0
    g12: LineSegment [constr] StartX=-196.022 StartY=30.0568 StartZ=0 EndX=-195.223 EndY=29.7661 EndZ=0
    g13: LineSegment StartX=-194.539 StartY=31.6454 StartZ=0 EndX=-195.907 EndY=27.8867 EndZ=0
    g14: LineSegment StartX=-196.137 StartY=32.2269 StartZ=0 EndX=-197.505 EndY=28.4681 EndZ=0
    g15: LineSegment StartX=-196.137 StartY=32.2269 StartZ=0 EndX=-194.539 EndY=31.6454 EndZ=0
    g16: LineSegment StartX=-197.505 StartY=28.4681 StartZ=0 EndX=-195.907 EndY=27.8867 EndZ=0
  constraints (34):
    c: Symmetric(g-5,g-5,g1)
    c: Symmetric(g-5,g-6,g0)
    c: Symmetric(g-6,g-6,g3)
    c: Symmetric(g-5,g-6,g2)
    c: Coincident(g5,g1)
    c: Coincident(g5,g4)
    c: Coincident(g6,g4)
    c: Coincident(g6,g3)
    c: Equal(g5,g6)
    c: Coincident(g7,g2)
    c: Coincident(g7,g4)
    c: Coincident(g8,g4)
    c: Coincident(g8,g0)
    c: Equal(g7,g8)
    c: Coincident(g11,g9)
    c: Coincident(g12,g9)
    c: Tangent(g10,g9) = -1.5708
    c: Perpendicular(g11,g9)
    c: Parallel(g9,g-4)
    c: Equal(g9,g10)
    c: Parallel(g12,g11)
    c: Equal(g11,g12)
    c: Distance(g11,g12) = 1.7
    c: Distance(g9,g10) = 4
    c: Symmetric(g13,g13,g12)
    c: Parallel(g13,g9)
    c: Symmetric(g14,g14,g11)
    c: Symmetric(g15,g15,g9)
    c: Parallel(g15,g11)
    c: Symmetric(g16,g16,g10)
    c: Coincident(g16,g14)
    c: Coincident(g15,g14)
    c: Coincident(g13,g15)
    c: Coincident(g9,g4)
FEATURE [Sketcher::SketchObject] Sketch057  label="buco interno per SWITCH"
  ArcFitTolerance = 1e-06
  AttachmentSupport = -> [XZ_Plane]
  ExternalGeometry = -> [Sketch]
  FullyConstrained = true
  MakeInternals = false
  MapMode = 5
  Placement = pos=(0,0,0) rot=(1,0,0;1.5708rad)
  sketch-geometry (10):
    g0: GeomPoint [constr] X=-187.821 Y=29.2 Z=0
    g1: LineSegment [constr] StartX=-188.505 StartY=27.3206 StartZ=0 EndX=-193.203 EndY=29.0307 EndZ=0
    g2: LineSegment [constr] StartX=-190.809 StartY=35.6086 StartZ=0 EndX=-195.597 EndY=22.4529 EndZ=0
    g3: GeomPoint [constr] X=-193.203 Y=29.0307 Z=0
    g4: LineSegment [constr] StartX=-196.492 StartY=30.2278 StartZ=0 EndX=-189.914 EndY=27.8336 EndZ=0
    g5: LineSegment StartX=-194.098 StartY=36.8056 StartZ=0 EndX=-187.52 EndY=34.4115 EndZ=0
    g6: LineSegment StartX=-194.098 StartY=36.8056 StartZ=0 EndX=-198.886 EndY=23.6499 EndZ=0
    g7: LineSegment StartX=-187.52 StartY=34.4115 StartZ=0 EndX=-192.308 EndY=21.2558 EndZ=0
    g8: LineSegment StartX=-198.886 StartY=23.6499 StartZ=0 EndX=-192.308 EndY=21.2558 EndZ=0
    g9: LineSegment [constr] StartX=-187.821 StartY=29.2 StartZ=0 EndX=-188.505 EndY=27.3206 EndZ=0
  constraints (23):
    c: Symmetric(g-3,g-3,g0)
    c: Perpendicular(g1,g-3)
    c: Parallel(g2,g-3)
    c: Symmetric(g2,g2,g3)
    c: Perpendicular(g2,g4)
    c: Symmetric(g4,g4,g3)
    c: Distance(g2) = 14
    c: Distance(g4) = 7
    c: Distance(g1) = 5
    c: Parallel(g5,g4)
    c: Parallel(g7,g2)
    c: Symmetric(g5,g5,g2)
    c: Symmetric(g6,g6,g4)
    c: Symmetric(g7,g7,g4)
    c: Symmetric(g8,g8,g2)
    c: Coincident(g6,g5)
    c: Coincident(g7,g5)
    c: Coincident(g8,g7)
    c: Coincident(g3,g1)
    c: Coincident(g9,g0)
    c: Parallel(g9,g-3)
    c: Distance(g9) = 2
    c: Coincident(g1,g9)
FEATURE [Sketcher::SketchObject] Sketch058  label="buco esterno per SWITCH"
  ArcFitTolerance = 1e-06
  AttachmentSupport = -> [XZ_Plane]
  ExternalGeometry = -> [Sketch057]
  FullyConstrained = true
  MakeInternals = false
  MapMode = 5
  Placement = pos=(0,0,0) rot=(1,0,0;1.5708rad)
  sketch-geometry (12):
    g0: GeomPoint [constr] X=-190.809 Y=35.6086 Z=0
    g1: GeomPoint [constr] X=-196.492 Y=30.2278 Z=0
    g2: GeomPoint [constr] X=-189.914 Y=27.8336 Z=0
    g3: GeomPoint [constr] X=-195.597 Y=22.4529 Z=0
    g4: GeomPoint [constr] X=-193.203 Y=29.0307 Z=0
    g5: LineSegment [constr] StartX=-192.006 StartY=32.3196 StartZ=0 EndX=-194.4 EndY=25.7418 EndZ=0
    g6: GeomPoint [constr] X=-193.203 Y=29.0307 Z=0
    g7: LineSegment [constr] StartX=-195.082 StartY=29.7148 StartZ=0 EndX=-191.324 EndY=28.3467 EndZ=0
    g8: LineSegment StartX=-193.885 StartY=33.0037 StartZ=0 EndX=-190.127 EndY=31.6356 EndZ=0
    g9: LineSegment StartX=-190.127 StartY=31.6356 StartZ=0 EndX=-192.521 EndY=25.0578 EndZ=0
    g10: LineSegment StartX=-196.28 StartY=26.4258 StartZ=0 EndX=-192.521 EndY=25.0578 EndZ=0
    g11: LineSegment StartX=-193.885 StartY=33.0037 StartZ=0 EndX=-196.28 EndY=26.4258 EndZ=0
  constraints (21):
    c: Symmetric(g-6,g-6,g3)
    c: Symmetric(g-4,g-6,g2)
    c: Symmetric(g-5,g-4,g0)
    c: Symmetric(g-5,g-6,g1)
    c: Symmetric(g1,g2,g4)
    c: Parallel(g5,g-4)
    c: Symmetric(g5,g5,g6)
    c: Perpendicular(g7,g5)
    c: Symmetric(g7,g7,g6)
    c: Distance(g5) = 7
    c: Distance(g7) = 4
    c: Parallel(g8,g7)
    c: Parallel(g11,g5)
    c: Symmetric(g8,g8,g5)
    c: Symmetric(g9,g9,g7)
    c: Symmetric(g10,g10,g5)
    c: Symmetric(g11,g11,g7)
    c: Coincident(g11,g8)
    c: Coincident(g9,g8)
    c: Coincident(g9,g10)
    c: Coincident(g6,g4)
FEATURE [Part::Extrusion] Extrude060  label="Extrude buco interno per SWITCH destro"
  Base = -> Sketch057
  Dir = (0,-1,2e-16)
  DirMode = 2
  FaceMakerClass = Part::FaceMakerBullseye
  FaceMakerMode = 3
  LengthFwd = 13.2
  LengthRev = 0
  Placement = pos=(0,2.6,0) rot=(0,0,1;0rad)
  Solid = true
  Symmetric = false
FEATURE [Part::Extrusion] Extrude061  label="Extrude buco esterno per SWITCH destro"
  Base = -> Sketch058
  Dir = (0,-1,2e-16)
  DirMode = 2
  FaceMakerClass = Part::FaceMakerBullseye
  FaceMakerMode = 3
  LengthFwd = 2
  LengthRev = 0
  Placement = pos=(0,-10.6,0) rot=(0,0,1;0rad)
  Solid = true
  Symmetric = false
FEATURE [Sketcher::SketchObject] Sketch059  label="buco per spazio introduzione SWITCH"
  ArcFitTolerance = 1e-06
  AttachmentSupport = -> [XZ_Plane]
  ExternalGeometry = -> [Sketch057,Sketch010]
  FullyConstrained = true
  MakeInternals = false
  MapMode = 5
  Placement = pos=(0,0,0) rot=(1,0,0;1.5708rad)
  sketch-geometry (8):
    g0: LineSegment [constr] StartX=-201.368 StartY=36.3521 StartZ=0 EndX=-195.094 EndY=34.0687 EndZ=0
    g1: LineSegment [constr] StartX=-194.098 StartY=36.8056 StartZ=0 EndX=-195.094 EndY=34.0687 EndZ=0
    g2: LineSegment StartX=-198.658 StartY=24.2771 StartZ=0 EndX=-199.654 EndY=21.5401 EndZ=0
    g3: LineSegment StartX=-199.654 StartY=21.5401 StartZ=0 EndX=-181.196 EndY=14.822 EndZ=0
    g4: LineSegment StartX=-181.196 StartY=14.822 StartZ=0 EndX=-180.2 EndY=17.559 EndZ=0
    g5: LineSegment StartX=-180.2 StartY=17.559 StartZ=0 EndX=-198.658 EndY=24.2771 EndZ=0
    g6: LineSegment [constr] StartX=-204.932 StartY=26.5605 StartZ=0 EndX=-198.658 EndY=24.2771 EndZ=0
    g7: LineSegment [constr] StartX=-198.658 StartY=24.2771 StartZ=0 EndX=-199.654 EndY=21.5401 EndZ=0
  constraints (20):
    c: Parallel(g1,g-3)
    c: Parallel(g0,g-4)
    c: Coincident(g0,g-4)
    c: Coincident(g1,g-3)
    c: Coincident(g0,g1)
    c: Coincident(g3,g2)
    c: Coincident(g4,g3)
    c: Coincident(g5,g4)
    c: Coincident(g5,g2)
    c: Parallel(g5,g-5)
    c: Parallel(g3,g-5)
    c: Parallel(g4,g-6)
    c: DistanceX(g-6,g4) = 0
    c: Coincident(g6,g-5)
    c: Equal(g6,g0)
    c: Coincident(g7,g6)
    c: Equal(g7,g1)
    c: Tangent(g7,g-3)
    c: Coincident(g2,g6)
    c: Coincident(g2,g7)
FEATURE [Part::Extrusion] Extrude062  label="Extrude buco per spazio introduzione SWITCH"
  Base = -> Sketch059
  Dir = (0,-1,2e-16)
  DirMode = 2
  FaceMakerClass = Part::FaceMakerBullseye
  FaceMakerMode = 3
  LengthFwd = 13.2
  LengthRev = 0
  Solid = true
  Symmetric = true
FEATURE [Part::Extrusion] Extrude063  label="Extrude buco interno per SWITCH sinistro"
  Base = -> Sketch057
  Dir = (0,-1,2e-16)
  DirMode = 2
  FaceMakerClass = Part::FaceMakerBullseye
  FaceMakerMode = 3
  LengthFwd = 13.2
  LengthRev = 0
  Placement = pos=(0,10.6,0) rot=(0,0,1;0rad)
  Solid = true
  Symmetric = false
FEATURE [Part::Extrusion] Extrude064  label="Extrude buco esterno per SWITCH sinistro"
  Base = -> Sketch058
  Dir = (0,-1,2e-16)
  DirMode = 2
  FaceMakerClass = Part::FaceMakerBullseye
  FaceMakerMode = 3
  LengthFwd = 2
  LengthRev = 0
  Placement = pos=(0,12.6,0) rot=(0,0,1;0rad)
  Solid = true
  Symmetric = false
FEATURE [Sketcher::SketchObject] Sketch061  label="struttura esterna blocco switch"
  ArcFitTolerance = 1e-06
  AttachmentSupport = -> [XZ_Plane003]
  FullyConstrained = true
  MakeInternals = false
  MapMode = 5
  Placement = pos=(0,0,0) rot=(1,0,0;1.5708rad)
  sketch-geometry (5):
    g0: LineSegment StartX=-1 StartY=-5.1 StartZ=0 EndX=1 EndY=-5.1 EndZ=0
    g1: LineSegment StartX=1 StartY=-5.1 StartZ=0 EndX=1 EndY=5.1 EndZ=0
    g2: LineSegment StartX=1 StartY=5.1 StartZ=0 EndX=-1 EndY=5.1 EndZ=0
    g3: LineSegment StartX=-1 StartY=5.1 StartZ=0 EndX=-1 EndY=-5.1 EndZ=0
    g4: GeomPoint [constr] X=0 Y=0 Z=0
  constraints (12):
    c: Coincident(g0,g1)
    c: Coincident(g1,g2)
    c: Coincident(g2,g3)
    c: Coincident(g3,g0)
    c: Horizontal(g0)
    c: Horizontal(g2)
    c: Vertical(g1)
    c: Vertical(g3)
    c: Symmetric(g2,g0,g4)
    c: Distance(g1,g3) = 2
    c: Distance(g0,g2) = 10.2
    c: Coincident(g4,g-1)
FEATURE [Sketcher::SketchObject] Sketch062  label="struttura interna blocco switch"
  ArcFitTolerance = 1e-06
  AttachmentSupport = -> [XZ_Plane003]
  ExternalGeometry = -> [Sketch061]
  FullyConstrained = true
  MakeInternals = false
  MapMode = 5
  Placement = pos=(0,0,0) rot=(1,0,0;1.5708rad)
  sketch-geometry (5):
    g0: LineSegment StartX=-1 StartY=3.1 StartZ=0 EndX=-1 EndY=-3.1 EndZ=0
    g1: LineSegment StartX=-1 StartY=-3.1 StartZ=0 EndX=1 EndY=-3.1 EndZ=0
    g2: LineSegment StartX=1 StartY=-3.1 StartZ=0 EndX=1 EndY=3.1 EndZ=0
    g3: LineSegment StartX=1 StartY=3.1 StartZ=0 EndX=-1 EndY=3.1 EndZ=0
    g4: GeomPoint [constr] X=0 Y=0 Z=0
  constraints (12):
    c: Coincident(g0,g1)
    c: Coincident(g1,g2)
    c: Coincident(g2,g3)
    c: Coincident(g3,g0)
    c: Vertical(g0)
    c: Vertical(g2)
    c: Horizontal(g1)
    c: Horizontal(g3)
    c: Symmetric(g2,g0,g4)
    c: Coincident(g4,g-1)
    c: Distance(g0) = 6.2
    c: Equal(g3,g-3)
FEATURE [Sketcher::SketchObject] Sketch063  label="blocchi tra switch"
  ArcFitTolerance = 1e-06
  AttachmentSupport = -> [XZ_Plane003]
  ExternalGeometry = -> [Sketch061,Sketch062]
  FullyConstrained = true
  MakeInternals = false
  MapMode = 5
  Placement = pos=(0,0,0) rot=(1,0,0;1.5708rad)
  sketch-geometry (8):
    g0: LineSegment StartX=-3 StartY=5.1 StartZ=0 EndX=-1 EndY=5.1 EndZ=0
    g1: LineSegment StartX=-1 StartY=5.1 StartZ=0 EndX=-1 EndY=3.1 EndZ=0
    g2: LineSegment StartX=-1 StartY=3.1 StartZ=0 EndX=-3 EndY=3.1 EndZ=0
    g3: LineSegment StartX=-3 StartY=3.1 StartZ=0 EndX=-3 EndY=5.1 EndZ=0
    g4: LineSegment StartX=-3 StartY=-3.1 StartZ=0 EndX=-1 EndY=-3.1 EndZ=0
    g5: LineSegment StartX=-1 StartY=-3.1 StartZ=0 EndX=-1 EndY=-5.1 EndZ=0
    g6: LineSegment StartX=-1 StartY=-5.1 StartZ=0 EndX=-3 EndY=-5.1 EndZ=0
    g7: LineSegment StartX=-3 StartY=-5.1 StartZ=0 EndX=-3 EndY=-3.1 EndZ=0
  constraints (20):
    c: Horizontal(g0)
    c: Coincident(g1,g0)
    c: Coincident(g2,g1)
    c: Horizontal(g2)
    c: Coincident(g3,g2)
    c: Coincident(g3,g0)
    c: Vertical(g3)
    c: Horizontal(g4)
    c: Coincident(g5,g4)
    c: Coincident(g6,g5)
    c: Horizontal(g6)
    c: Coincident(g7,g6)
    c: Coincident(g7,g4)
    c: Vertical(g7)
    c: Coincident(g0,g-4)
    c: Coincident(g1,g-5)
    c: Coincident(g4,g-6)
    c: Coincident(g5,g-7)
    c: Distance(g0) = 2
    c: Distance(g4) = 2
FEATURE [Sketcher::SketchObject] Sketch066  label="piano per rampino"
  ArcFitTolerance = 1e-06
  AttachmentSupport = -> [XZ_Plane002]
  ExternalGeometry = -> [Sketch045]
  FullyConstrained = true
  MakeInternals = false
  MapMode = 5
  Placement = pos=(0,0,0) rot=(1,0,0;1.5708rad)
  sketch-geometry (4):
    g0: LineSegment StartX=5.4 StartY=5.1 StartZ=0 EndX=5.4 EndY=3.9 EndZ=0
    g1: LineSegment StartX=5.4 StartY=3.9 StartZ=0 EndX=7 EndY=3.9 EndZ=0
    g2: LineSegment StartX=7 StartY=3.9 StartZ=0 EndX=7 EndY=5.1 EndZ=0
    g3: LineSegment StartX=7 StartY=5.1 StartZ=0 EndX=5.4 EndY=5.1 EndZ=0
  constraints (11):
    c: Coincident(g0,g1)
    c: Coincident(g1,g2)
    c: Coincident(g2,g3)
    c: Coincident(g3,g0)
    c: Vertical(g0)
    c: Vertical(g2)
    c: Horizontal(g1)
    c: Horizontal(g3)
    c: Distance(g0,g2) = 1.6
    c: Distance(g1,g3) = 1.2
    c: Coincident(g2,g-3)
FEATURE [Sketcher::SketchObject] Sketch064  label="rampini_per_serraggio_struttura"
  ArcFitTolerance = 1e-06
  AttachmentSupport = -> [XZ_Plane002]
  ExternalGeometry = -> [Sketch066,Sketch045]
  FullyConstrained = true
  MakeInternals = false
  MapMode = 5
  Placement = pos=(0,0,0) rot=(1,0,0;1.5708rad)
  sketch-geometry (7):
    g0: LineSegment StartX=7 StartY=5.1 StartZ=0 EndX=7 EndY=3.9 EndZ=0
    g1: LineSegment StartX=7 StartY=3.9 StartZ=0 EndX=9 EndY=3.9 EndZ=0
    g2: LineSegment StartX=7 StartY=5.1 StartZ=0 EndX=7 EndY=5.1 EndZ=0
    g3: LineSegment StartX=7 StartY=5.1 StartZ=0 EndX=7 EndY=7.5 EndZ=0
    g4: LineSegment StartX=9 StartY=5.1 StartZ=0 EndX=9 EndY=3.9 EndZ=0
    g5: LineSegment StartX=7 StartY=7.5 StartZ=0 EndX=9 EndY=7.5 EndZ=0
    g6: LineSegment StartX=9 StartY=7.5 StartZ=0 EndX=9 EndY=5.1 EndZ=0
  constraints (20):
    c: Vertical(g0)
    c: Coincident(g1,g0)
    c: Horizontal(g1)
    c: Coincident(g2,g0)
    c: Horizontal(g2)
    c: Coincident(g3,g2)
    c: Vertical(g3)
    c: Coincident(g5,g3)
    c: Coincident(g4,g6)
    c: Coincident(g4,g1)
    c: Vertical(g4)
    c: Coincident(g0,g-3)
    c: DistanceY(g-4,g3) = 2.4
    c: DistanceX(g1,g1) = 2
    c: DistanceY(g2,g6) = 0
    c: DistanceX(g2,g2) = 0
    c: DistanceY(g0,g0) = 1.2
    c: Coincident(g5,g6)
    c: Horizontal(g5)
    c: Vertical(g6)
FEATURE [Sketcher::SketchObject] Sketch067  label="perno per blocco switch"
  ArcFitTolerance = 1e-06
  AttachmentSupport = -> [XZ_Plane]
  ExternalGeometry = -> [Sketch,Sketch010]
  FullyConstrained = true
  MakeInternals = false
  MapMode = 5
  Placement = pos=(0,0,0) rot=(1,0,0;1.5708rad)
  sketch-geometry (14):
    g0: LineSegment StartX=-191.073 StartY=24.9429 StartZ=0 EndX=-185.81 EndY=23.0276 EndZ=0
    g1: LineSegment StartX=-183.76 StartY=23.9839 StartZ=0 EndX=-182.392 EndY=27.7427 EndZ=0
    g2: LineSegment StartX=-183.348 StartY=29.7934 StartZ=0 EndX=-188.61 EndY=31.7087 EndZ=0
    g3: LineSegment StartX=-188.61 StartY=31.7087 StartZ=0 EndX=-191.073 EndY=24.9429 EndZ=0
    g4: GeomPoint [constr] X=-186.459 Y=27.0946 Z=0
    g5: LineSegment StartX=-189.022 StartY=25.8992 StartZ=0 EndX=-185.263 EndY=24.5311 EndZ=0
    g6: LineSegment StartX=-185.263 StartY=24.5311 StartZ=0 EndX=-183.895 EndY=28.2899 EndZ=0
    g7: LineSegment StartX=-183.895 StartY=28.2899 StartZ=0 EndX=-187.654 EndY=29.658 EndZ=0
    g8: LineSegment StartX=-187.654 StartY=29.658 StartZ=0 EndX=-189.022 EndY=25.8992 EndZ=0
    g9: GeomPoint [constr] X=-186.459 Y=27.0946 Z=0
    g10: ArcOfCircle CenterX=-185.263 CenterY=24.5311 CenterZ=0 NormalX=0 NormalY=0 NormalZ=1 AngleXU=0 Radius=1.6 StartAngle=4.36332 EndAngle=5.93412
    g11: GeomPoint [constr] X=-184.307 Y=22.4804 Z=0
    g12: ArcOfCircle CenterX=-183.895 CenterY=28.2899 CenterZ=0 NormalX=0 NormalY=0 NormalZ=1 AngleXU=0 Radius=1.6 StartAngle=5.93412 EndAngle=7.50492
    g13: GeomPoint [constr] X=-181.844 Y=29.2462 Z=0
  constraints (30):
    c: Coincident(g2,g3)
    c: Coincident(g3,g0)
    c: Symmetric(g13,g0,g4)
    c: Distance(g11,g3) = 7.2
    c: Distance(g0,g2) = 7.2
    c: Parallel(g3,g1)
    c: Parallel(g2,g0)
    c: Perpendicular(g2,g3)
    c: Coincident(g5,g6)
    c: Coincident(g6,g7)
    c: Coincident(g7,g8)
    c: Coincident(g8,g5)
    c: Symmetric(g7,g5,g9)
    c: Distance(g6,g8) = 4
    c: Distance(g5,g7) = 4
    c: Coincident(g9,g4)
    c: Parallel(g8,g6)
    c: Parallel(g7,g5)
    c: Perpendicular(g7,g8)
    c: Tangent(g8,g-3)
    c: Tangent(g2,g-4)
    c: PointOnObject(g11,g1)
    c: PointOnObject(g11,g0)
    c: Tangent(g1,g10) = -1.5708
    c: Tangent(g0,g10) = -1.5708
    c: PointOnObject(g13,g1)
    c: Tangent(g1,g12) = -1.5708
    c: Tangent(g2,g12) = -1.5708
    c: Equal(g10,g12)
    c: Coincident(g10,g5)
FEATURE [Part::Extrusion] Extrude072  label="Extrude perno per blocco switch"
  Base = -> Sketch067
  Dir = (0,-1,2e-16)
  DirMode = 2
  FaceMakerClass = Part::FaceMakerBullseye
  FaceMakerMode = 3
  LengthFwd = 25.2
  LengthRev = 0
  Solid = true
  Symmetric = true
FEATURE [Part::MultiFuse] Fusion
  Refine = true
  Shapes = -> [Extrude,Sweep,Extrude007,Extrude011,Extrude005,Extrude012,Extrude013,Extrude016,Extrude031,Extrude039,Extrude045,Extrude072]
FEATURE [Part::Cut] Cut
  Base = -> Fusion
  Refine = true
  Tool = -> Extrude001
FEATURE [Part::Cut] Cut001
  Base = -> Cut
  Refine = true
  Tool = -> Extrude004
FEATURE [Part::Cut] Cut002
  Base = -> Cut001
  Refine = true
  Tool = -> Extrude006
FEATURE [Part::Cut] Cut003
  Base = -> Cut002
  Refine = true
  Tool = -> Extrude008
FEATURE [Part::Cut] Cut004
  Base = -> Cut003
  Refine = true
  Tool = -> Extrude009
FEATURE [Part::Cut] Cut005
  Base = -> Cut004
  Refine = true
  Tool = -> Extrude010
FEATURE [Part::Cut] Cut006
  Base = -> Cut005
  Refine = true
  Tool = -> Extrude014
FEATURE [Part::Cut] Cut007
  Base = -> Cut006
  Refine = true
  Tool = -> Extrude015
FEATURE [Part::Cut] Cut008
  Base = -> Cut007
  Refine = true
  Tool = -> Extrude018
FEATURE [Part::Cut] Cut009
  Base = -> Cut008
  Refine = true
  Tool = -> Extrude019
FEATURE [Part::Cut] Cut010
  Base = -> Cut009
  Refine = true
  Tool = -> Extrude020
FEATURE [Part::Cut] Cut011
  Base = -> Cut010
  Refine = true
  Tool = -> Extrude021
FEATURE [Part::Cut] Cut012
  Base = -> Cut011
  Refine = true
  Tool = -> Extrude022
FEATURE [Part::Cut] Cut013
  Base = -> Cut012
  Refine = true
  Tool = -> Extrude023
FEATURE [Part::Cut] Cut014
  Base = -> Cut013
  Refine = true
  Tool = -> Extrude032
FEATURE [Part::Cut] Cut015
  Base = -> Cut014
  Refine = true
  Tool = -> Extrude033
FEATURE [Part::Cut] Cut016
  Base = -> Cut015
  Refine = true
  Tool = -> Extrude034
FEATURE [Part::Cut] Cut017
  Base = -> Cut016
  Refine = true
  Tool = -> Extrude035
FEATURE [Part::Cut] Cut018
  Base = -> Cut017
  Refine = true
  Tool = -> Extrude036
FEATURE [Part::Cut] Cut019
  Base = -> Cut018
  Refine = true
  Tool = -> Extrude037
FEATURE [Part::Cut] Cut020
  Base = -> Cut019
  Refine = true
  Tool = -> Extrude030
FEATURE [Part::Cut] Cut022
  Base = -> Cut020
  Refine = true
  Tool = -> Extrude038
FEATURE [Part::Cut] Cut023
  Base = -> Cut022
  Refine = true
  Tool = -> Extrude041
FEATURE [Part::Cut] Cut024
  Base = -> Cut023
  Refine = true
  Tool = -> Extrude040
FEATURE [Part::Cut] Cut025
  Base = -> Cut024
  Refine = true
  Tool = -> Extrude042
FEATURE [Part::Cut] Cut026
  Base = -> Cut025
  Refine = true
  Tool = -> Extrude043
FEATURE [Part::Cut] Cut027
  Base = -> Cut026
  Refine = true
  Tool = -> Extrude044
FEATURE [Part::Cut] Cut028
  Base = -> Cut027
  Refine = true
  Tool = -> Extrude046
FEATURE [Part::Cut] Cut029
  Base = -> Cut028
  Refine = true
  Tool = -> Extrude047
FEATURE [Part::Cut] Cut033
  Base = -> Cut029
  Refine = true
  Tool = -> Extrude055
FEATURE [Part::Cut] Cut034
  Base = -> Cut033
  Refine = true
  Tool = -> Extrude056
FEATURE [Part::Cut] Cut035
  Base = -> Cut034
  Refine = true
  Tool = -> Extrude057
FEATURE [Part::Cut] Cut037
  Base = -> Cut035
  Refine = true
  Tool = -> Extrude060
FEATURE [Part::Cut] Cut038
  Base = -> Cut037
  Refine = true
  Tool = -> Extrude061
FEATURE [Part::Cut] Cut039
  Base = -> Cut038
  Refine = true
  Tool = -> Extrude063
FEATURE [Part::Cut] Cut040
  Base = -> Cut039
  Refine = true
  Tool = -> Extrude064
FEATURE [Part::Cut] Cut041
  Base = -> Cut040
  Refine = true
  Tool = -> Extrude062
FEATURE [Sketcher::SketchObject] Sketch068  label="base con smusso sopra neopixel"
  ArcFitTolerance = 1e-06
  AttachmentSupport = -> [YZ_Plane002]
  FullyConstrained = true
  MakeInternals = false
  MapMode = 5
  Placement = pos=(0,0,0) rot=(0.57735,0.57735,0.57735;2.0944rad)
  sketch-geometry (5):
    g0: LineSegment StartX=-9.5 StartY=-6.1 StartZ=0 EndX=9.5 EndY=-6.1 EndZ=0
    g1: LineSegment StartX=9.5 StartY=-6.1 StartZ=0 EndX=9.5 EndY=6.1 EndZ=0
    g2: LineSegment StartX=9.5 StartY=6.1 StartZ=0 EndX=-9.5 EndY=6.1 EndZ=0
    g3: LineSegment StartX=-9.5 StartY=6.1 StartZ=0 EndX=-9.5 EndY=-6.1 EndZ=0
    g4: GeomPoint [constr] X=0 Y=0 Z=0
  constraints (12):
    c: Coincident(g0,g1)
    c: Coincident(g1,g2)
    c: Coincident(g2,g3)
    c: Coincident(g3,g0)
    c: Horizontal(g0)
    c: Horizontal(g2)
    c: Vertical(g1)
    c: Vertical(g3)
    c: Symmetric(g2,g0,g4)
    c: Distance(g1,g3) = 19
    c: Distance(g0,g2) = 12.2
    c: Coincident(g4,g-1)
FEATURE [Sketcher::SketchObject] Sketch069  label="cilindro minore"
  ArcFitTolerance = 1e-06
  AttachmentSupport = -> [XZ_Plane004]
  FullyConstrained = true
  MakeInternals = false
  MapMode = 5
  Placement = pos=(0,0,0) rot=(1,0,0;1.5708rad)
  sketch-geometry (1):
    g0: Circle CenterX=0 CenterY=0 CenterZ=0 NormalX=0 NormalY=0 NormalZ=1 AngleXU=0 Radius=5.8
  constraints (2):
    c: Diameter(g0) = 11.6
    c: Coincident(g0,g-1)
FEATURE [Sketcher::SketchObject] Sketch070  label="cilindro maggiore"
  ArcFitTolerance = 1e-06
  AttachmentSupport = -> [XZ_Plane004]
  ExternalGeometry = -> [Sketch069]
  FullyConstrained = true
  MakeInternals = false
  MapMode = 5
  Placement = pos=(0,0,0) rot=(1,0,0;1.5708rad)
  sketch-geometry (1):
    g0: Circle CenterX=0 CenterY=0 CenterZ=0 NormalX=0 NormalY=0 NormalZ=1 AngleXU=0 Radius=6.5
  constraints (2):
    c: Coincident(g0,g-1)
    c: Diameter(g0) = 13
FEATURE [Sketcher::SketchObject] Sketch071  label="buco interno"
  ArcFitTolerance = 1e-06
  AttachmentSupport = -> [XZ_Plane004]
  ExternalGeometry = -> [Sketch069]
  FullyConstrained = true
  MakeInternals = false
  MapMode = 5
  Placement = pos=(0,0,0) rot=(1,0,0;1.5708rad)
  sketch-geometry (1):
    g0: Circle CenterX=0 CenterY=0 CenterZ=0 NormalX=0 NormalY=0 NormalZ=1 AngleXU=0 Radius=5
  constraints (2):
    c: Coincident(g0,g-1)
    c: Diameter(g0) = 10
FEATURE [PartDesign::Pad] Pad
  Direction = (0,-1,2e-16)
  Length = 1.2
  Length2 = 10
  Placement = pos=(0,0,0) rot=(1,0,0;1.5708rad)
  Profile = -> Sketch070
  ReferenceAxis = -> Sketch070 [N_Axis]
  Refine = true
  Suppressed = false
  Type = 0
FEATURE [PartDesign::Pad] Pad001
  BaseFeature = -> Pad
  Direction = (0,-1,2e-16)
  Length = 5.6
  Length2 = 10
  Placement = pos=(0,0,0) rot=(1,0,0;1.5708rad)
  Profile = -> Sketch069
  ReferenceAxis = -> Sketch069 [N_Axis]
  Refine = true
  Suppressed = false
  Type = 0
FEATURE [PartDesign::Pocket] Pocket
  BaseFeature = -> Pad001
  Direction = (0,1,-2e-16)
  Length = 7
  Length2 = 5
  Midplane = true
  Placement = pos=(0,0,0) rot=(1,0,0;1.5708rad)
  Profile = -> Sketch071
  ReferenceAxis = -> Sketch071 [N_Axis]
  Refine = true
  Suppressed = false
  Type = 0
FEATURE [PartDesign::Fillet] Fillet
  Base = -> Pocket [Face7]
  BaseFeature = -> Pocket
  Placement = pos=(0,0,0) rot=(1,0,0;1.5708rad)
  Radius = 1
  Refine = true
  SupportTransform = false
  Suppressed = false
  UseAllEdges = false
FEATURE [PartDesign::Body] Body004  label="pulsanti lato sinistro"
  AllowCompound = false
  Group = -> [Sketch069,Sketch070,Sketch071,Pad,Pad001,Pocket,Fillet]
  Origin = -> Origin004
  Tip = -> Fillet
FEATURE [Sketcher::SketchObject] Sketch072  label="buco per saldature e diodo driver solenoide"
  ArcFitTolerance = 1e-06
  AttachmentSupport = -> [XZ_Plane]
  ExternalGeometry = -> [Sketch038]
  FullyConstrained = true
  MakeInternals = false
  MapMode = 5
  Placement = pos=(0,0,0) rot=(1,0,0;1.5708rad)
  sketch-geometry (4):
    g0: LineSegment StartX=-212.269 StartY=-43.9083 StartZ=0 EndX=-207.197 EndY=-33.0326 EndZ=0
    g1: LineSegment StartX=-207.197 StartY=-33.0326 StartZ=0 EndX=-207.56 EndY=-32.8635 EndZ=0
    g2: LineSegment StartX=-207.56 StartY=-32.8635 StartZ=0 EndX=-212.631 EndY=-43.7392 EndZ=0
    g3: LineSegment StartX=-212.631 StartY=-43.7392 StartZ=0 EndX=-212.269 EndY=-43.9083 EndZ=0
  constraints (11):
    c: Coincident(g1,g0)
    c: Coincident(g2,g1)
    c: Coincident(g3,g2)
    c: Coincident(g3,g0)
    c: Parallel(g-3,g0)
    c: Parallel(g0,g2)
    c: Perpendicular(g0,g3)
    c: Perpendicular(g1,g0)
    c: Distance(g3) = 0.4
    c: Distance(g2) = 12
    c: Coincident(g0,g-3)
FEATURE [Part::Extrusion] Extrude074  label="Extrude buco per saldature e diodo driver solenoide"
  Base = -> Sketch072
  Dir = (0,-1,2e-16)
  DirMode = 2
  FaceMakerClass = Part::FaceMakerBullseye
  FaceMakerMode = 3
  LengthFwd = 14.6
  LengthRev = 0
  Solid = true
  Symmetric = true
FEATURE [Part::Cut] Cut042
  Base = -> Cut041
  Refine = true
  Tool = -> Extrude074
FEATURE [Sketcher::SketchObject] Sketch073  label="fori slargati blocco solenoide"
  ArcFitTolerance = 1e-06
  AttachmentSupport = -> [XY_Plane]
  ExternalGeometry = -> [Sketch030]
  FullyConstrained = true
  MakeInternals = false
  MapMode = 5
  sketch-geometry (2):
    g0: Circle CenterX=-152.209 CenterY=6.95 CenterZ=0 NormalX=0 NormalY=0 NormalZ=1 AngleXU=0 Radius=3.7
    g1: Circle CenterX=-130.41 CenterY=-6.95 CenterZ=0 NormalX=0 NormalY=0 NormalZ=1 AngleXU=0 Radius=3.7
  constraints (4):
    c: Diameter(g0) = 7.4
    c: Coincident(g0,g-3)
    c: Diameter(g1) = 7.4
    c: Coincident(g1,g-4)
FEATURE [Part::Extrusion] Extrude075  label="Extrude fori slargati blocco solenoide"
  Base = -> Sketch073
  Dir = (0,0,1)
  DirMode = 2
  FaceMakerClass = Part::FaceMakerBullseye
  FaceMakerMode = 3
  LengthFwd = 1.5
  LengthRev = 0
  Placement = pos=(0,0,36.4) rot=(0,0,1;0rad)
  Solid = true
  Symmetric = false
FEATURE [Part::Cut] Cut043
  Base = -> Cut042
  Refine = true
  Tool = -> Extrude075
FEATURE [Sketcher::SketchObject] Sketch074  label="lato sx pistola"
  ArcFitTolerance = 1e-06
  AttachmentSupport = -> [XZ_Plane]
  ExternalGeometry = -> [Sketch016,Sketch,Sketch058]
  FullyConstrained = true
  MakeInternals = false
  MapMode = 5
  Placement = pos=(0,0,0) rot=(1,0,0;1.5708rad)
  sketch-geometry (37):
    g0: LineSegment StartX=-82.8 StartY=3.2 StartZ=0 EndX=0 EndY=3.2 EndZ=0
    g1: LineSegment StartX=-82.8 StartY=3.2 StartZ=0 EndX=-82.8 EndY=6.2 EndZ=0
    g2: LineSegment [constr] StartX=-107.6 StartY=18 StartZ=0 EndX=-107.6 EndY=20 EndZ=0
    g3: LineSegment [constr] StartX=-132.428 StartY=18 StartZ=0 EndX=-132.428 EndY=20 EndZ=0
    g4: LineSegment StartX=-132.428 StartY=20 StartZ=0 EndX=-107.6 EndY=20 EndZ=0
    g5: ArcOfCircle CenterX=-107.6 CenterY=4 CenterZ=0 NormalX=0 NormalY=0 NormalZ=1 AngleXU=0 Radius=16 StartAngle=0.137937 EndAngle=1.5708
    g6: LineSegment StartX=-82.8 StartY=6.2 StartZ=0 EndX=-91.752 EndY=6.2 EndZ=0
    g7: LineSegment [constr] StartX=-145.743 StartY=8.32624 StartZ=0 EndX=-147.645 EndY=8.94427 EndZ=0
    g8: ArcOfCircle CenterX=-132.428 CenterY=4 CenterZ=0 NormalX=0 NormalY=0 NormalZ=1 AngleXU=0 Radius=16 StartAngle=1.5708 EndAngle=2.82743
    g9: LineSegment StartX=-215.932 StartY=-80.4316 StartZ=0 EndX=-176.685 EndY=-80.4316 EndZ=0
    g10: LineSegment StartX=-147.645 StartY=8.94427 StartZ=0 EndX=-176.685 EndY=-80.4316 EndZ=0
    g11: LineSegment [constr] StartX=-193.988 StartY=-2.33927 StartZ=0 EndX=-192.176 EndY=-3.18451 EndZ=0
    g12: LineSegment [constr] StartX=-217.232 StartY=-52.1862 StartZ=0 EndX=-215.42 EndY=-53.0314 EndZ=0
    g13: LineSegment StartX=-192.176 StartY=-3.18451 StartZ=0 EndX=-215.42 EndY=-53.0314 EndZ=0
    g14: ArcOfCircle CenterX=-184.801 CenterY=-67.3089 CenterZ=0 NormalX=0 NormalY=0 NormalZ=1 AngleXU=0 Radius=33.7833 StartAngle=2.70526 EndAngle=3.54053
    g15: ArcOfCircle CenterX=-207.583 CenterY=4 CenterZ=0 NormalX=0 NormalY=0 NormalZ=1 AngleXU=0 Radius=17 StartAngle=5.84685 EndAngle=7.56663
    g16: LineSegment StartX=-202.765 StartY=20.303 StartZ=0 EndX=-195.887 EndY=39.2 EndZ=0
    g17: LineSegment [constr] StartX=-193.885 StartY=33.0037 StartZ=0 EndX=-197.644 EndY=34.3718 EndZ=0
    g18: LineSegment StartX=-195.887 StartY=39.2 StartZ=0 EndX=0 EndY=39.2 EndZ=0
    g19: LineSegment StartX=0 StartY=3.2 StartZ=0 EndX=0 EndY=39.2 EndZ=0
    g20: LineSegment StartX=-189.939 StartY=31.5672 StartZ=0 EndX=-192.333 EndY=24.9893 EndZ=0
    g21: LineSegment StartX=-196.467 StartY=26.4942 StartZ=0 EndX=-194.073 EndY=33.0721 EndZ=0
    g22: Circle CenterX=-213.443 CenterY=-76.8316 CenterZ=0 NormalX=0 NormalY=0 NormalZ=1 AngleXU=0 Radius=1.8
    g23: Circle CenterX=-179.305 CenterY=-76.8316 CenterZ=0 NormalX=0 NormalY=0 NormalZ=1 AngleXU=0 Radius=1.8
    g24: Circle CenterX=-184.08 CenterY=34.8 CenterZ=0 NormalX=0 NormalY=0 NormalZ=1 AngleXU=0 Radius=1.8
    g25: Circle CenterX=-78.51 CenterY=34.8 CenterZ=0 NormalX=0 NormalY=0 NormalZ=1 AngleXU=0 Radius=1.8
    g26: Circle CenterX=-78.51 CenterY=7.6 CenterZ=0 NormalX=0 NormalY=0 NormalZ=1 AngleXU=0 Radius=1.8
    g27: Circle CenterX=-5.6 CenterY=34.8 CenterZ=0 NormalX=0 NormalY=0 NormalZ=1 AngleXU=0 Radius=1.8
    g28: Circle CenterX=-5.6 CenterY=7.6 CenterZ=0 NormalX=0 NormalY=0 NormalZ=1 AngleXU=0 Radius=1.8
    g29: LineSegment StartX=-190.127 StartY=31.6356 StartZ=0 EndX=-189.939 EndY=31.5672 EndZ=0
    g30: LineSegment StartX=-194.073 StartY=33.0721 StartZ=0 EndX=-193.885 EndY=33.0037 EndZ=0
    g31: LineSegment StartX=-193.885 StartY=33.0037 StartZ=0 EndX=-190.127 EndY=31.6356 EndZ=0
    g32: LineSegment StartX=-196.467 StartY=26.4942 StartZ=0 EndX=-192.333 EndY=24.9893 EndZ=0
    g33: Circle CenterX=-19 CenterY=21.2 CenterZ=0 NormalX=0 NormalY=0 NormalZ=1 AngleXU=0 Radius=6.3
    g34: Circle CenterX=-42 CenterY=21.2 CenterZ=0 NormalX=0 NormalY=0 NormalZ=1 AngleXU=0 Radius=6.3
    g35: Circle CenterX=-65 CenterY=21.2 CenterZ=0 NormalX=0 NormalY=0 NormalZ=1 AngleXU=0 Radius=6.3
    g36: LineSegment [constr] StartX=-4 StartY=21.2 StartZ=0 EndX=-65 EndY=21.2 EndZ=0
  constraints (96):
    c: Coincident(g0,g-41)
    c: Horizontal(g0)
    c: PointOnObject(g0,g-39)
    c: Coincident(g1,g0)
    c: Vertical(g1)
    c: DistanceY(g1,g1) = 3
    c: Coincident(g2,g-17)
    c: Vertical(g2)
    c: Coincident(g3,g-16)
    c: Vertical(g3)
    c: DistanceY(g2,g2) = 2
    c: DistanceY(g3,g3) = 2
    c: Coincident(g4,g3)
    c: Coincident(g4,g2)
    c: Coincident(g5,g-17)
    c: Coincident(g5,g2)
    c: Coincident(g6,g1)
    c: Horizontal(g6)
    c: Coincident(g6,g5)
    c: Coincident(g7,g-15)
    c: Coincident(g8,g7)
    c: Coincident(g8,g3)
    c: Coincident(g8,g-15)
    c: Horizontal(g9)
    c: DistanceY(g-13,g9) = 2
    c: Coincident(g10,g7)
    c: Parallel(g10,g-14)
    c: Coincident(g9,g10)
    c: Distance(g11) = 2
    c: Coincident(g11,g-11)
    c: Perpendicular(g-11,g11)
    c: Distance(g12) = 2
    c: Coincident(g12,g-12)
    c: Perpendicular(g-11,g12)
    c: Coincident(g13,g11)
    c: Coincident(g13,g12)
    c: Coincident(g14,g-32)
    c: Coincident(g14,g12)
    c: Coincident(g14,g9)
    c: Coincident(g15,g-10)
    c: Coincident(g15,g11)
    c: Parallel(g16,g-22)
    c: Distance(g17) = 4
    c: PointOnObject(g17,g16)
    c: Coincident(g15,g16)
    c: Horizontal(g18)
    c: Coincident(g18,g16)
    c: Coincident(g19,g0)
    c: PointOnObject(g19,g-39)
    c: DistanceY(g19,g-36) = 2
    c: Coincident(g18,g19)
    c: Diameter(g22) = 3.6
    c: Coincident(g22,g-9)
    c: Diameter(g23) = 3.6
    c: Coincident(g23,g-8)
    c: Diameter(g24) = 3.6
    c: Diameter(g25) = 3.6
    c: Diameter(g26) = 3.6
    c: Diameter(g27) = 3.6
    c: Diameter(g28) = 3.6
    c: Coincident(g27,g-4)
    c: Coincident(g28,g-3)
    c: Coincident(g25,g-6)
    c: Coincident(g26,g-5)
    c: Coincident(g24,g-7)
    c: Parallel(g20,g-21)
    c: Equal(g20,g-21)
    c: Parallel(g21,g-19)
    c: Equal(g21,g-19)
    c: Distance(g29) = 0.2
    c: Distance(g30) = 0.2
    c: Parallel(g29,g-20)
    c: Parallel(g31,g-20)
    c: Equal(g31,g-20)
    c: Coincident(g30,g31)
    c: Coincident(g31,g29)
    c: Coincident(g29,g-21)
    c: Parallel(g30,g31)
    c: Coincident(g17,g30)
    c: Coincident(g20,g29)
    c: Coincident(g21,g30)
    c: Perpendicular(g16,g17)
    c: Coincident(g32,g21)
    c: Coincident(g32,g20)
    c: Perpendicular(g10,g7)
    c: Diameter(g33) = 12.6
    c: Diameter(g34) = 12.6
    c: Diameter(g35) = 12.6
    c: Horizontal(g36)
    c: PointOnObject(g33,g36)
    c: PointOnObject(g34,g36)
    c: DistanceX(g34,g33) = 23
    c: DistanceX(g35,g34) = 23
    c: DistanceX(g33,g36) = 15
    c: Symmetric(g-24,g-24,g36)
    c: Coincident(g36,g35)
FEATURE [Sketcher::SketchObject] Sketch075  label="lato dx pistola"
  ArcFitTolerance = 1e-06
  AttachmentSupport = -> [XZ_Plane]
  ExternalGeometry = -> [Sketch016,Sketch,Sketch058,Sketch074]
  FullyConstrained = true
  MakeInternals = false
  MapMode = 5
  Placement = pos=(0,0,0) rot=(1,0,0;1.5708rad)
  sketch-geometry (61):
    g0: LineSegment StartX=-82.8 StartY=3.2 StartZ=0 EndX=0 EndY=3.2 EndZ=0
    g1: LineSegment StartX=-82.8 StartY=3.2 StartZ=0 EndX=-82.8 EndY=6.2 EndZ=0
    g2: LineSegment [constr] StartX=-107.6 StartY=18 StartZ=0 EndX=-107.6 EndY=20 EndZ=0
    g3: LineSegment [constr] StartX=-132.428 StartY=18 StartZ=0 EndX=-132.428 EndY=20 EndZ=0
    g4: LineSegment StartX=-132.428 StartY=20 StartZ=0 EndX=-107.6 EndY=20 EndZ=0
    g5: ArcOfCircle CenterX=-107.6 CenterY=4 CenterZ=0 NormalX=0 NormalY=0 NormalZ=1 AngleXU=0 Radius=16 StartAngle=0.137937 EndAngle=1.5708
    g6: LineSegment StartX=-82.8 StartY=6.2 StartZ=0 EndX=-91.752 EndY=6.2 EndZ=0
    g7: LineSegment [constr] StartX=-145.743 StartY=8.32624 StartZ=0 EndX=-147.645 EndY=8.94427 EndZ=0
    g8: ArcOfCircle CenterX=-132.428 CenterY=4 CenterZ=0 NormalX=0 NormalY=0 NormalZ=1 AngleXU=0 Radius=16 StartAngle=1.5708 EndAngle=2.82743
    g9: LineSegment StartX=-215.932 StartY=-80.4316 StartZ=0 EndX=-176.685 EndY=-80.4316 EndZ=0
    g10: LineSegment StartX=-147.645 StartY=8.94427 StartZ=0 EndX=-176.685 EndY=-80.4316 EndZ=0
    g11: LineSegment [constr] StartX=-193.988 StartY=-2.33927 StartZ=0 EndX=-192.176 EndY=-3.18451 EndZ=0
    g12: LineSegment [constr] StartX=-217.232 StartY=-52.1862 StartZ=0 EndX=-215.42 EndY=-53.0314 EndZ=0
    g13: LineSegment StartX=-192.176 StartY=-3.18451 StartZ=0 EndX=-215.42 EndY=-53.0314 EndZ=0
    g14: ArcOfCircle CenterX=-184.801 CenterY=-67.3089 CenterZ=0 NormalX=0 NormalY=0 NormalZ=1 AngleXU=0 Radius=33.7833 StartAngle=2.70526 EndAngle=3.54053
    g15: ArcOfCircle CenterX=-207.583 CenterY=4 CenterZ=0 NormalX=0 NormalY=0 NormalZ=1 AngleXU=0 Radius=17 StartAngle=5.84685 EndAngle=7.56663
    g16: LineSegment StartX=-202.765 StartY=20.303 StartZ=0 EndX=-195.887 EndY=39.2 EndZ=0
    g17: LineSegment [constr] StartX=-193.885 StartY=33.0037 StartZ=0 EndX=-197.644 EndY=34.3718 EndZ=0
    g18: LineSegment StartX=-195.887 StartY=39.2 StartZ=0 EndX=0 EndY=39.2 EndZ=0
    g19: LineSegment StartX=0 StartY=3.2 StartZ=0 EndX=0 EndY=39.2 EndZ=0
    g20: LineSegment StartX=-189.939 StartY=31.5672 StartZ=0 EndX=-192.333 EndY=24.9893 EndZ=0
    g21: LineSegment StartX=-196.467 StartY=26.4942 StartZ=0 EndX=-194.073 EndY=33.0721 EndZ=0
    g22: Circle CenterX=-213.443 CenterY=-76.8316 CenterZ=0 NormalX=0 NormalY=0 NormalZ=1 AngleXU=0 Radius=1.8
    g23: Circle CenterX=-179.305 CenterY=-76.8316 CenterZ=0 NormalX=0 NormalY=0 NormalZ=1 AngleXU=0 Radius=1.8
    g24: Circle CenterX=-184.08 CenterY=34.8 CenterZ=0 NormalX=0 NormalY=0 NormalZ=1 AngleXU=0 Radius=1.8
    g25: Circle CenterX=-78.51 CenterY=34.8 CenterZ=0 NormalX=0 NormalY=0 NormalZ=1 AngleXU=0 Radius=1.8
    g26: Circle CenterX=-78.51 CenterY=7.6 CenterZ=0 NormalX=0 NormalY=0 NormalZ=1 AngleXU=0 Radius=1.8
    g27: Circle CenterX=-5.6 CenterY=34.8 CenterZ=0 NormalX=0 NormalY=0 NormalZ=1 AngleXU=0 Radius=1.8
    g28: Circle CenterX=-5.6 CenterY=7.6 CenterZ=0 NormalX=0 NormalY=0 NormalZ=1 AngleXU=0 Radius=1.8
    g29: LineSegment StartX=-190.127 StartY=31.6356 StartZ=0 EndX=-189.939 EndY=31.5672 EndZ=0
    g30: LineSegment StartX=-194.073 StartY=33.0721 StartZ=0 EndX=-193.885 EndY=33.0037 EndZ=0
    g31: LineSegment StartX=-193.885 StartY=33.0037 StartZ=0 EndX=-190.127 EndY=31.6356 EndZ=0
    g32: LineSegment StartX=-196.467 StartY=26.4942 StartZ=0 EndX=-192.333 EndY=24.9893 EndZ=0
    g33: LineSegment [constr] StartX=-4 StartY=21.2 StartZ=0 EndX=-87.91 EndY=21.2 EndZ=0
    g34: GeomPoint [constr] X=-4 Y=21.2 Z=0
    g35: LineSegment [constr] StartX=-15.2 StartY=33.7 StartZ=0 EndX=-15.2 EndY=8.7 EndZ=0
    g36: LineSegment [constr] StartX=-15.2 StartY=33.7 StartZ=0 EndX=-56.2 EndY=33.7 EndZ=0
    g37: LineSegment [constr] StartX=-15.2 StartY=8.7 StartZ=0 EndX=-56.2 EndY=8.7 EndZ=0
    g38: LineSegment [constr] StartX=-56.2 StartY=33.7 StartZ=0 EndX=-56.2 EndY=8.7 EndZ=0
    g39: Circle CenterX=-18.6 CenterY=30.3 CenterZ=0 NormalX=0 NormalY=0 NormalZ=1 AngleXU=0 Radius=3.4
    g40: Circle CenterX=-18.6 CenterY=12.1 CenterZ=0 NormalX=0 NormalY=0 NormalZ=1 AngleXU=0 Radius=3.4
    g41: Circle CenterX=-43.2 CenterY=30.3 CenterZ=0 NormalX=0 NormalY=0 NormalZ=1 AngleXU=0 Radius=3.4
    g42: Circle CenterX=-43.2 CenterY=12.1 CenterZ=0 NormalX=0 NormalY=0 NormalZ=1 AngleXU=0 Radius=3.4
    g43: LineSegment [constr] StartX=-4 StartY=21.2 StartZ=0 EndX=-15.2 EndY=21.2 EndZ=0
    g44: LineSegment [constr] StartX=-15.2 StartY=21.2 StartZ=0 EndX=-36.2 EndY=21.2 EndZ=0
    g45: LineSegment [constr] StartX=-41.5 StartY=16.2 StartZ=0 EndX=-30.9 EndY=16.2 EndZ=0
    g46: LineSegment [constr] StartX=-30.9 StartY=16.2 StartZ=0 EndX=-30.9 EndY=26.2 EndZ=0
    g47: LineSegment [constr] StartX=-30.9 StartY=26.2 StartZ=0 EndX=-41.5 EndY=26.2 EndZ=0
    g48: LineSegment [constr] StartX=-41.5 StartY=26.2 StartZ=0 EndX=-41.5 EndY=16.2 EndZ=0
    g49: GeomPoint [constr] X=-36.2 Y=21.2 Z=0
    g50: Circle CenterX=-36.2 CenterY=21.2 CenterZ=0 NormalX=0 NormalY=0 NormalZ=1 AngleXU=0 Radius=2.8
    g51: LineSegment [constr] StartX=-24.2 StartY=26.7 StartZ=0 EndX=-24.2 EndY=15.7 EndZ=0
    g52: Circle CenterX=-24.2 CenterY=26.7 CenterZ=0 NormalX=0 NormalY=0 NormalZ=1 AngleXU=0 Radius=3
    g53: Circle CenterX=-24.2 CenterY=15.7 CenterZ=0 NormalX=0 NormalY=0 NormalZ=1 AngleXU=0 Radius=3
    g54: GeomPoint X=-18.6 Y=30.3 Z=0
    g55: GeomPoint X=-18.6 Y=12.1 Z=0
    g56: GeomPoint X=-43.2 Y=12.1 Z=0
    g57: GeomPoint X=-43.2 Y=30.3 Z=0
    g58: Circle CenterX=-65 CenterY=21.2 CenterZ=0 NormalX=0 NormalY=0 NormalZ=1 AngleXU=0 Radius=1.5
    g59: Circle CenterX=-42 CenterY=21.2 CenterZ=0 NormalX=0 NormalY=0 NormalZ=1 AngleXU=0 Radius=1.5
    g60: Circle CenterX=-19 CenterY=21.2 CenterZ=0 NormalX=0 NormalY=0 NormalZ=1 AngleXU=0 Radius=1.5
  constraints (149):
    c: Coincident(g0,g-41)
    c: Horizontal(g0)
    c: PointOnObject(g0,g-39)
    c: Coincident(g1,g0)
    c: Vertical(g1)
    c: DistanceY(g1,g1) = 3
    c: Coincident(g2,g-17)
    c: Vertical(g2)
    c: Coincident(g3,g-16)
    c: Vertical(g3)
    c: DistanceY(g2,g2) = 2
    c: DistanceY(g3,g3) = 2
    c: Coincident(g4,g3)
    c: Coincident(g4,g2)
    c: Coincident(g5,g-17)
    c: Coincident(g5,g2)
    c: Coincident(g6,g1)
    c: Horizontal(g6)
    c: Coincident(g6,g5)
    c: Coincident(g7,g-15)
    c: Coincident(g8,g7)
    c: Coincident(g8,g3)
    c: Coincident(g8,g-15)
    c: Horizontal(g9)
    c: DistanceY(g-13,g9) = 2
    c: Coincident(g10,g7)
    c: Parallel(g10,g-14)
    c: Coincident(g9,g10)
    c: Distance(g11) = 2
    c: Coincident(g11,g-11)
    c: Perpendicular(g-11,g11)
    c: Distance(g12) = 2
    c: Coincident(g12,g-12)
    c: Perpendicular(g-11,g12)
    c: Coincident(g13,g11)
    c: Coincident(g13,g12)
    c: Coincident(g14,g-32)
    c: Coincident(g14,g12)
    c: Coincident(g14,g9)
    c: Coincident(g15,g-10)
    c: Coincident(g15,g11)
    c: Parallel(g16,g-22)
    c: Distance(g17) = 4
    c: PointOnObject(g17,g16)
    c: Coincident(g15,g16)
    c: Horizontal(g18)
    c: Coincident(g18,g16)
    c: Coincident(g19,g0)
    c: PointOnObject(g19,g-39)
    c: DistanceY(g19,g-36) = 2
    c: Coincident(g18,g19)
    c: Diameter(g22) = 3.6
    c: Coincident(g22,g-9)
    c: Diameter(g23) = 3.6
    c: Coincident(g23,g-8)
    c: Diameter(g24) = 3.6
    c: Diameter(g25) = 3.6
    c: Diameter(g26) = 3.6
    c: Diameter(g27) = 3.6
    c: Diameter(g28) = 3.6
    c: Coincident(g27,g-4)
    c: Coincident(g28,g-3)
    c: Coincident(g25,g-6)
    c: Coincident(g26,g-5)
    c: Coincident(g24,g-7)
    c: Parallel(g20,g-21)
    c: Equal(g20,g-21)
    c: Parallel(g21,g-19)
    c: Equal(g21,g-19)
    c: Distance(g29) = 0.2
    c: Distance(g30) = 0.2
    c: Parallel(g29,g-20)
    c: Parallel(g31,g-20)
    c: Equal(g31,g-20)
    c: Coincident(g30,g31)
    c: Coincident(g31,g29)
    c: Coincident(g29,g-21)
    c: Parallel(g30,g31)
    c: Coincident(g17,g30)
    c: Coincident(g20,g29)
    c: Coincident(g21,g30)
    c: Perpendicular(g16,g17)
    c: Coincident(g32,g21)
    c: Coincident(g32,g20)
    c: Perpendicular(g10,g7)
    c: Horizontal(g33)
    c: Symmetric(g-24,g-24,g33)
    c: PointOnObject(g33,g-28)
    c: Symmetric(g-24,g-24,g34)
    c: DistanceY(g35,g35) = 25
    c: Symmetric(g35,g35,g33)
    c: Distance(g36) = 41
    c: Coincident(g36,g35)
    c: Horizontal(g36)
    c: Coincident(g37,g35)
    c: Horizontal(g37)
    c: Coincident(g38,g36)
    c: Vertical(g38)
    c: Coincident(g37,g38)
    c: Diameter(g39) = 6.8
    c: Diameter(g40) = 6.8
    c: Tangent(g39,g36)
    c: Tangent(g40,g37)
    c: Tangent(g39,g35)
    c: Tangent(g40,g35)
    c: Diameter(g41) = 6.8
    c: Diameter(g42) = 6.8
    c: Tangent(g41,g36)
    c: Tangent(g42,g37)
    c: DistanceX(g41,g39) = 24.6
    c: DistanceX(g42,g40) = 24.6
    c: Distance(g43) = 11.2
    c: Coincident(g43,g33)
    c: PointOnObject(g43,g33)
    c: PointOnObject(g43,g35)
    c: Distance(g44) = 21
    c: Coincident(g44,g43)
    c: PointOnObject(g44,g33)
    c: Coincident(g45,g46)
    c: Coincident(g46,g47)
    c: Coincident(g47,g48)
    c: Coincident(g48,g45)
    c: Horizontal(g45)
    c: Horizontal(g47)
    c: Vertical(g46)
    c: Vertical(g48)
    c: Symmetric(g47,g45,g49)
    c: Distance(g46,g48) = 10.6
    c: Distance(g45,g47) = 10
    c: Coincident(g49,g44)
    c: Diameter(g50) = 5.6
    c: Coincident(g50,g44)
    c: Distance(g51) = 11
    c: Symmetric(g51,g51,g33)
    c: DistanceX(g51,g43) = 9
    c: Diameter(g52) = 6
    c: Coincident(g52,g51)
    c: Diameter(g53) = 6
    c: Coincident(g53,g51)
    c: Coincident(g40,g55)
    c: Coincident(g39,g54)
    c: Coincident(g41,g57)
    c: Coincident(g42,g56)
    c: Diameter(g58) = 3
    c: Diameter(g59) = 3
    c: Diameter(g60) = 3
    c: Coincident(g58,g-44)
    c: Coincident(g59,g-46)
    c: Coincident(g60,g-45)
FEATURE [Sketcher::SketchObject] Sketch078
  ArcFitTolerance = 1e-06
  AttachmentSupport = -> [XZ_Plane005]
  FullyConstrained = true
  MakeInternals = false
  MapMode = 5
  Placement = pos=(0,0,0) rot=(1,0,0;1.5708rad)
  sketch-geometry (5):
    g0: LineSegment [constr] StartX=0 StartY=5.5 StartZ=0 EndX=0 EndY=-5.5 EndZ=0
    g1: ArcOfCircle CenterX=0 CenterY=5.5 CenterZ=0 NormalX=0 NormalY=0 NormalZ=1 AngleXU=0 Radius=2.7 StartAngle=0 EndAngle=3.14159
    g2: ArcOfCircle CenterX=0 CenterY=-5.5 CenterZ=0 NormalX=0 NormalY=0 NormalZ=1 AngleXU=0 Radius=2.7 StartAngle=3.1416 EndAngle=6.28318
    g3: LineSegment StartX=-2.7 StartY=5.5 StartZ=0 EndX=-2.7 EndY=-5.50001 EndZ=0
    g4: LineSegment StartX=2.7 StartY=5.5 StartZ=0 EndX=2.7 EndY=-5.50001 EndZ=0
  constraints (13):
    c: Distance(g0) = 11
    c: Vertical(g0)
    c: Symmetric(g0,g0,g-1)
    c: Radius(g1) = 2.7
    c: Coincident(g1,g0)
    c: Radius(g2) = 2.7
    c: Coincident(g2,g0)
    c: Vertical(g3)
    c: Vertical(g4)
    c: Coincident(g2,g4)
    c: Coincident(g2,g3)
    c: Tangent(g3,g1) = -1.5708
    c: Tangent(g4,g1) = 1.5708
FEATURE [PartDesign::Pad] Pad002
  Direction = (0,-1,2e-16)
  Length = 0.8
  Length2 = 10
  Placement = pos=(0,0,0) rot=(1,0,0;1.5708rad)
  Profile = -> Sketch078
  ReferenceAxis = -> Sketch078 [N_Axis]
  Refine = true
  Suppressed = false
  Type = 0
FEATURE [Sketcher::SketchObject] Sketch079
  ArcFitTolerance = 1e-06
  AttachmentSupport = -> [XZ_Plane005]
  ExternalGeometry = -> [Sketch078]
  FullyConstrained = true
  MakeInternals = false
  MapMode = 5
  Placement = pos=(0,0,0) rot=(1,0,0;1.5708rad)
  sketch-geometry (2):
    g0: Circle CenterX=-1e-16 CenterY=5.5 CenterZ=0 NormalX=0 NormalY=0 NormalZ=1 AngleXU=0 Radius=2.7
    g1: Circle CenterX=0 CenterY=-5.5 CenterZ=0 NormalX=0 NormalY=0 NormalZ=1 AngleXU=0 Radius=2.7
  constraints (4):
    c: Coincident(g0,g-3)
    c: PointOnObject(g-3,g0)
    c: Coincident(g1,g-4)
    c: Equal(g1,g-4)
FEATURE [PartDesign::Pad] Pad003
  BaseFeature = -> Pad002
  Direction = (0,-1,2e-16)
  Length = 5
  Length2 = 10
  Placement = pos=(0,0,0) rot=(1,0,0;1.5708rad)
  Profile = -> Sketch079
  ReferenceAxis = -> Sketch079 [N_Axis]
  Refine = true
  Suppressed = false
  Type = 0
FEATURE [PartDesign::Fillet] Fillet001
  Base = -> Pad003 [Edge16,Edge14]
  BaseFeature = -> Pad003
  Placement = pos=(0,0,0) rot=(1,0,0;1.5708rad)
  Radius = 0.4
  Refine = true
  SupportTransform = false
  Suppressed = false
  UseAllEdges = false
FEATURE [PartDesign::Body] Body005  label="pulsanti lato destro"
  AllowCompound = false
  Group = -> [Sketch078,Pad002,Sketch079,Pad003,Fillet001]
  Origin = -> Origin005
  Tip = -> Fillet001
FEATURE [PartDesign::SubShapeBinder] Binder
  BindCopyOnChange = 0
  BindMode = 0
  ClaimChildren = false
  Context = -> Body006 [Binder.]
  Fuse = false
  MakeFace = true
  OffsetFill = false
  OffsetIntersection = false
  OffsetJoinType = 0
  OffsetOpenResult = false
  PartialLoad = false
  Refine = true
  Relative = true
  Support = -> [Body[Sketch074.]]
  _Version = 2
FEATURE [PartDesign::SubShapeBinder] Binder001
  BindCopyOnChange = 0
  BindMode = 0
  ClaimChildren = false
  Context = -> Body007 [Binder001.]
  Fuse = false
  MakeFace = true
  OffsetFill = false
  OffsetIntersection = false
  OffsetJoinType = 0
  OffsetOpenResult = false
  PartialLoad = false
  Refine = true
  Relative = true
  Support = -> [Body[Sketch075.]]
  _Version = 2
FEATURE [Mesh::Feature] logo_per_PCB_definitivo_positivo
  Placement = pos=(-191,17,-66) rot=(0,1,1;0rad)
FEATURE [Sketcher::SketchObject] Sketch114  label="Sketch114 - base lato DX"
  ArcFitTolerance = 1e-06
  AttachmentSupport = -> [Binder001]
  ExternalGeometry = -> [Binder001]
  FullyConstrained = true
  MakeInternals = false
  MapMode = 5
  Placement = pos=(0,1e-15,0) rot=(0,0.707107,0.707107;3.14159rad)
  sketch-geometry (30):
    g0: Circle CenterX=5.6 CenterY=34.8 CenterZ=0 NormalX=0 NormalY=0 NormalZ=1 AngleXU=0 Radius=1.8
    g1: Circle CenterX=5.6 CenterY=7.6 CenterZ=0 NormalX=0 NormalY=0 NormalZ=1 AngleXU=0 Radius=1.8
    g2: Circle CenterX=24.2 CenterY=26.7 CenterZ=0 NormalX=0 NormalY=0 NormalZ=1 AngleXU=0 Radius=3
    g3: Circle CenterX=24.2 CenterY=15.7 CenterZ=0 NormalX=0 NormalY=0 NormalZ=1 AngleXU=0 Radius=3
    g4: Circle CenterX=36.2 CenterY=21.2 CenterZ=0 NormalX=0 NormalY=0 NormalZ=1 AngleXU=0 Radius=2.8
    g5: Circle CenterX=78.51 CenterY=34.8 CenterZ=0 NormalX=0 NormalY=0 NormalZ=1 AngleXU=0 Radius=1.8
    g6: Circle CenterX=78.51 CenterY=7.6 CenterZ=0 NormalX=0 NormalY=0 NormalZ=1 AngleXU=0 Radius=1.8
    g7: Circle CenterX=184.08 CenterY=34.8 CenterZ=0 NormalX=0 NormalY=0 NormalZ=1 AngleXU=0 Radius=1.8
    g8: Circle CenterX=213.443 CenterY=-76.8316 CenterZ=0 NormalX=0 NormalY=0 NormalZ=1 AngleXU=0 Radius=1.8
    g9: Circle CenterX=179.305 CenterY=-76.8316 CenterZ=0 NormalX=0 NormalY=0 NormalZ=1 AngleXU=0 Radius=1.8
    g10: ArcOfCircle [constr] CenterX=132.428 CenterY=4 CenterZ=0 NormalX=0 NormalY=0 NormalZ=1 AngleXU=0 Radius=16 StartAngle=0.314159 EndAngle=1.5708
    g11: ArcOfCircle CenterX=107.6 CenterY=4 CenterZ=0 NormalX=0 NormalY=0 NormalZ=1 AngleXU=0 Radius=16 StartAngle=1.5708 EndAngle=3.00366
    g12: ArcOfCircle CenterX=207.583 CenterY=4 CenterZ=0 NormalX=0 NormalY=0 NormalZ=1 AngleXU=0 Radius=17 StartAngle=1.85815 EndAngle=3.57792
    g13: ArcOfCircle CenterX=184.801 CenterY=-67.3089 CenterZ=0 NormalX=0 NormalY=0 NormalZ=1 AngleXU=0 Radius=33.7833 StartAngle=5.88425 EndAngle=6.71952
    g14: LineSegment StartX=0 StartY=39.2 StartZ=0 EndX=0 EndY=3.2 EndZ=0
    g15: LineSegment StartX=0 StartY=3.2 StartZ=0 EndX=82.8 EndY=3.2 EndZ=0
    g16: LineSegment StartX=82.8 StartY=3.2 StartZ=0 EndX=82.8 EndY=6.2 EndZ=0
    g17: LineSegment StartX=82.8 StartY=6.2 StartZ=0 EndX=91.752 EndY=6.2 EndZ=0
    g18: LineSegment StartX=107.6 StartY=20 StartZ=0 EndX=132.428 EndY=20 EndZ=0
    g19: LineSegment StartX=147.645 StartY=8.94427 StartZ=0 EndX=176.685 EndY=-80.4316 EndZ=0
    g20: LineSegment StartX=176.685 StartY=-80.4316 StartZ=0 EndX=215.932 EndY=-80.4316 EndZ=0
    g21: LineSegment StartX=215.42 StartY=-53.0314 StartZ=0 EndX=192.176 EndY=-3.18451 EndZ=0
    g22: LineSegment StartX=202.765 StartY=20.303 StartZ=0 EndX=195.887 EndY=39.2 EndZ=0
    g23: LineSegment StartX=195.887 StartY=39.2 StartZ=0 EndX=0 EndY=39.2 EndZ=0
    g24: LineSegment StartX=196.467 StartY=26.4942 StartZ=0 EndX=194.073 EndY=33.0721 EndZ=0
    g25: LineSegment StartX=194.073 StartY=33.0721 StartZ=0 EndX=189.939 EndY=31.5672 EndZ=0
    g26: LineSegment StartX=189.939 StartY=31.5672 StartZ=0 EndX=192.333 EndY=24.9893 EndZ=0
    g27: LineSegment StartX=192.333 StartY=24.9893 StartZ=0 EndX=196.467 EndY=26.4942 EndZ=0
    g28: LineSegment StartX=132.428 StartY=20 StartZ=0 EndX=144.053 EndY=20 EndZ=0
    g29: LineSegment StartX=144.053 StartY=20 StartZ=0 EndX=147.645 EndY=8.94427 EndZ=0
  constraints (65):
    c: Equal(g0,g-25)
    c: Equal(g2,g-29)
    c: Equal(g3,g-30)
    c: Equal(g4,g-28)
    c: Equal(g1,g-26)
    c: Coincident(g0,g-25)
    c: Coincident(g1,g-26)
    c: Coincident(g2,g-29)
    c: Coincident(g3,g-30)
    c: Coincident(g4,g-28)
    c: Equal(g5,g-23)
    c: Equal(g6,g-24)
    c: Coincident(g5,g-23)
    c: Coincident(g6,g-24)
    c: Equal(g7,g-20)
    c: Coincident(g7,g-20)
    c: Equal(g9,g-22)
    c: Coincident(g9,g-22)
    c: Equal(g8,g-21)
    c: Coincident(g8,g-21)
    c: Equal(g13,g-12)
    c: Equal(g12,g-14)
    c: Equal(g10,g-9)
    c: Equal(g11,g-7)
    c: Coincident(g14,g-27)
    c: Coincident(g14,g-27)
    c: Coincident(g15,g14)
    c: Coincident(g15,g-5)
    c: Coincident(g16,g15)
    c: Coincident(g16,g-6)
    c: Coincident(g17,g16)
    c: Coincident(g17,g-7)
    c: Coincident(g11,g17)
    c: Coincident(g11,g-8)
    c: Coincident(g18,g11)
    c: Coincident(g18,g-9)
    c: Coincident(g10,g18)
    c: Coincident(g10,g-10)
    c: Coincident(g19,g10)
    c: Coincident(g19,g-11)
    c: Coincident(g20,g19)
    c: Coincident(g20,g-12)
    c: Coincident(g13,g20)
    c: Coincident(g13,g-13)
    c: Coincident(g21,g13)
    c: Coincident(g21,g-14)
    c: Coincident(g12,g21)
    c: Coincident(g12,g-15)
    c: Coincident(g22,g12)
    c: Coincident(g22,g-15)
    c: Coincident(g23,g22)
    c: Coincident(g23,g14)
    c: Coincident(g24,g-18)
    c: Coincident(g24,g-16)
    c: Coincident(g25,g24)
    c: Coincident(g25,g-19)
    c: Coincident(g26,g25)
    c: Coincident(g26,g-19)
    c: Coincident(g27,g26)
    c: Coincident(g27,g24)
    c: Coincident(g29,g10)
    c: Coincident(g28,g10)
    c: Coincident(g29,g28)
    c: Parallel(g28,g18)
    c: Parallel(g29,g19)
FEATURE [PartDesign::Pad] Pad011
  Direction = (0,1,-2e-16)
  Length = 2
  Length2 = 10
  Profile = -> Sketch114
  ReferenceAxis = -> Sketch114 [N_Axis]
  Refine = true
  Reversed = true
  Suppressed = false
  Type = 0
FEATURE [Sketcher::SketchObject] Sketch115
  ArcFitTolerance = 1e-06
  AttachmentSupport = -> [Pad011]
  ExternalGeometry = -> [Binder001]
  FullyConstrained = true
  MakeInternals = false
  MapMode = 5
  Placement = pos=(0,1.7e-15,0) rot=(0,0.707107,0.707107;3.14159rad)
  sketch-geometry (4):
    g0: ArcOfCircle CenterX=24.2 CenterY=26.7 CenterZ=0 NormalX=0 NormalY=0 NormalZ=1 AngleXU=0 Radius=3 StartAngle=4.48384e-08 EndAngle=3.14159
    g1: ArcOfCircle CenterX=24.2 CenterY=15.7 CenterZ=0 NormalX=0 NormalY=0 NormalZ=1 AngleXU=0 Radius=3 StartAngle=3.14159 EndAngle=6.28318
    g2: LineSegment StartX=21.2 StartY=26.7 StartZ=0 EndX=21.2 EndY=15.7 EndZ=0
    g3: LineSegment StartX=27.2 StartY=26.7 StartZ=0 EndX=27.2 EndY=15.7 EndZ=0
  constraints (12):
    c: Equal(g1,g-4)
    c: Equal(g0,g-3)
    c: Coincident(g0,g-3)
    c: Coincident(g1,g-4)
    c: Vertical(g2)
    c: Vertical(g3)
    c: Tangent(g3,g-3)
    c: Tangent(g2,g-3)
    c: Coincident(g0,g2)
    c: Coincident(g0,g3)
    c: Coincident(g1,g2)
    c: Coincident(g3,g1)
FEATURE [Sketcher::SketchObject] Sketch117  label="Sketch117 - fori per inserto M3 x 3 x 4.5"
  ArcFitTolerance = 1e-06
  AttachmentSupport = -> [Pad011]
  ExternalGeometry = -> [Binder001]
  FullyConstrained = true
  MakeInternals = false
  MapMode = 5
  Placement = pos=(0,1.7e-15,0) rot=(0,0.707107,0.707107;3.14159rad)
  sketch-geometry (4):
    g0: Circle CenterX=43.2 CenterY=30.3 CenterZ=0 NormalX=0 NormalY=0 NormalZ=1 AngleXU=0 Radius=2.25
    g1: Circle CenterX=43.2 CenterY=12.1 CenterZ=0 NormalX=0 NormalY=0 NormalZ=1 AngleXU=0 Radius=2.25
    g2: Circle CenterX=18.6 CenterY=30.3 CenterZ=0 NormalX=0 NormalY=0 NormalZ=1 AngleXU=0 Radius=2.25
    g3: Circle CenterX=18.6 CenterY=12.1 CenterZ=0 NormalX=0 NormalY=0 NormalZ=1 AngleXU=0 Radius=2.25
  constraints (8):
    c: Diameter(g0) = 4.5
    c: Diameter(g1) = 4.5
    c: Diameter(g2) = 4.5
    c: Diameter(g3) = 4.5
    c: Coincident(g2,g-3)
    c: Coincident(g3,g-6)
    c: Coincident(g0,g-4)
    c: Coincident(g1,g-5)
FEATURE [Sketcher::SketchObject] Sketch118
  ArcFitTolerance = 1e-06
  AttachmentSupport = -> [Pad011]
  ExternalGeometry = -> [Binder001]
  FullyConstrained = true
  MakeInternals = false
  MapMode = 5
  Placement = pos=(0,-2,0) rot=(1,0,0;1.5708rad)
  sketch-geometry (12):
    g0: Circle CenterX=-78.51 CenterY=34.8 CenterZ=0 NormalX=0 NormalY=0 NormalZ=1 AngleXU=0 Radius=1.8
    g1: Circle CenterX=-78.51 CenterY=7.6 CenterZ=0 NormalX=0 NormalY=0 NormalZ=1 AngleXU=0 Radius=1.8
    g2: Circle CenterX=-5.6 CenterY=34.8 CenterZ=0 NormalX=0 NormalY=0 NormalZ=1 AngleXU=0 Radius=1.8
    g3: Circle CenterX=-5.6 CenterY=7.6 CenterZ=0 NormalX=0 NormalY=0 NormalZ=1 AngleXU=0 Radius=1.8
    g4: LineSegment StartX=0 StartY=39.2 StartZ=0 EndX=0 EndY=3.2 EndZ=0
    g5: LineSegment StartX=0 StartY=3.2 StartZ=0 EndX=-82.8 EndY=3.2 EndZ=0
    g6: LineSegment StartX=-82.8 StartY=3.2 StartZ=0 EndX=-82.8 EndY=39.2 EndZ=0
    g7: LineSegment StartX=-82.8 StartY=39.2 StartZ=0 EndX=0 EndY=39.2 EndZ=0
    g8: ArcOfCircle CenterX=-65 CenterY=21.2 CenterZ=0 NormalX=0 NormalY=0 NormalZ=1 AngleXU=0 Radius=10 StartAngle=1.5708 EndAngle=4.71239
    g9: ArcOfCircle CenterX=-19 CenterY=21.2 CenterZ=0 NormalX=0 NormalY=0 NormalZ=1 AngleXU=0 Radius=10 StartAngle=4.71239 EndAngle=7.85398
    g10: LineSegment StartX=-65 StartY=31.2 StartZ=0 EndX=-19 EndY=31.2 EndZ=0
    g11: LineSegment StartX=-65 StartY=11.2 StartZ=0 EndX=-19 EndY=11.2 EndZ=0
  constraints (25):
    c: Equal(g2,g-5)
    c: Equal(g3,g-7)
    c: Equal(g1,g-6)
    c: Equal(g0,g-4)
    c: Coincident(g0,g-4)
    c: Coincident(g1,g-6)
    c: Coincident(g3,g-7)
    c: Coincident(g2,g-5)
    c: Coincident(g4,g-8)
    c: Coincident(g4,g-9)
    c: Coincident(g5,g4)
    c: Coincident(g5,g-10)
    c: Coincident(g6,g5)
    c: PointOnObject(g6,g-3)
    c: Vertical(g6)
    c: Coincident(g7,g6)
    c: Coincident(g7,g4)
    c: Tangent(g8,g10) = 1.5708
    c: Tangent(g8,g11) = -1.5708
    c: Tangent(g9,g10) = 1.5708
    c: Tangent(g9,g11) = -1.5708
    c: Equal(g8,g9)
    c: Radius(g8) = 10
    c: Coincident(g8,g-11)
    c: Coincident(g9,g-12)
FEATURE [Sketcher::SketchObject] Sketch120
  ArcFitTolerance = 1e-06
  AttachmentSupport = -> [Pad011]
  ExternalGeometry = -> [Binder001]
  FullyConstrained = true
  MakeInternals = false
  MapMode = 5
  Placement = pos=(0,-2,0) rot=(1,0,0;1.5708rad)
  sketch-geometry (4):
    g0: LineSegment StartX=-137.815 StartY=39.2 StartZ=0 EndX=-142.655 EndY=24.303 EndZ=0
    g1: LineSegment StartX=-137.815 StartY=39.2 StartZ=0 EndX=-110.815 EndY=39.2 EndZ=0
    g2: LineSegment StartX=-142.655 StartY=24.303 StartZ=0 EndX=-110.815 EndY=24.303 EndZ=0
    g3: ArcOfCircle CenterX=-92.2534 CenterY=31.7515 CenterZ=0 NormalX=0 NormalY=0 NormalZ=1 AngleXU=0 Radius=20 StartAngle=2.75997 EndAngle=3.52321
  constraints (12):
    c: PointOnObject(g0,g-3)
    c: Coincident(g1,g0)
    c: PointOnObject(g1,g-3)
    c: Coincident(g2,g0)
    c: Horizontal(g2)
    c: Tangent(g0,g-4)
    c: Vertical(g2,g1)
    c: DistanceX(g1,g1) = 27
    c: DistanceY(g-6,g0) = 4
    c: Radius(g3) = 20
    c: Coincident(g3,g1)
    c: Coincident(g3,g2)
FEATURE [Sketcher::SketchObject] Sketch121
  ArcFitTolerance = 1e-06
  AttachmentSupport = -> [Pad011]
  ExternalGeometry = -> [Binder001]
  FullyConstrained = true
  MakeInternals = false
  MapMode = 5
  Placement = pos=(0,-2,0) rot=(1,0,0;1.5708rad)
  sketch-geometry (15):
    g0: LineSegment StartX=-137.815 StartY=39.2 StartZ=0 EndX=-143.955 EndY=20.303 EndZ=0
    g1: LineSegment StartX=-143.955 StartY=20.303 StartZ=0 EndX=-190.141 EndY=20.303 EndZ=0
    g2: LineSegment StartX=-190.141 StartY=20.303 StartZ=0 EndX=-186.139 EndY=31.3 EndZ=0
    g3: LineSegment StartX=-178.754 StartY=39.2 StartZ=0 EndX=-180.791 EndY=33.6029 EndZ=0
    g4: ArcOfCircle CenterX=-184.08 CenterY=34.8 CenterZ=0 NormalX=0 NormalY=0 NormalZ=1 AngleXU=0 Radius=3.5 StartAngle=4.71239 EndAngle=5.93412
    g5: LineSegment StartX=-184.08 StartY=31.3 StartZ=0 EndX=-186.139 EndY=31.3 EndZ=0
    g6: LineSegment StartX=-137.815 StartY=39.2 StartZ=0 EndX=-156.815 EndY=39.2 EndZ=0
    g7: LineSegment StartX=-168.815 StartY=39.2 StartZ=0 EndX=-178.754 EndY=39.2 EndZ=0
    g8: LineSegment StartX=-157.815 StartY=39.2 StartZ=0 EndX=-167.815 EndY=39.2 EndZ=0
    g9: LineSegment StartX=-168.815 StartY=31.2 StartZ=0 EndX=-156.815 EndY=31.2 EndZ=0
    g10: LineSegment StartX=-167.436 StartY=36.2 StartZ=0 EndX=-157.436 EndY=36.2 EndZ=0
    g11: ArcOfCircle CenterX=-176.411 CenterY=35.2 CenterZ=0 NormalX=0 NormalY=0 NormalZ=1 AngleXU=0 Radius=20 StartAngle=6.08183 EndAngle=6.48454
    g12: ArcOfCircle CenterX=-188.411 CenterY=35.2 CenterZ=0 NormalX=0 NormalY=0 NormalZ=1 AngleXU=0 Radius=20 StartAngle=6.08183 EndAngle=6.48454
    g13: ArcOfCircle CenterX=-177.411 CenterY=35.2 CenterZ=0 NormalX=0 NormalY=0 NormalZ=1 AngleXU=0 Radius=20 StartAngle=0.0500209 EndAngle=0.201358
    g14: ArcOfCircle CenterX=-187.411 CenterY=35.2 CenterZ=0 NormalX=0 NormalY=0 NormalZ=1 AngleXU=0 Radius=20 StartAngle=0.0500209 EndAngle=0.201358
  constraints (46):
    c: PointOnObject(g0,g-3)
    c: Tangent(g0,g-5)
    c: Coincident(g1,g0)
    c: Horizontal(g1)
    c: Coincident(g2,g1)
    c: PointOnObject(g3,g-3)
    c: Parallel(g3,g-6)
    c: Parallel(g2,g-6)
    c: Radius(g4) = 3.5
    c: Coincident(g4,g-7)
    c: Tangent(g3,g4) = 1.5708
    c: Horizontal(g5)
    c: Tangent(g5,g4) = 1.5708
    c: DistanceX(g-8,g5) = 3.8
    c: Coincident(g2,g5)
    c: Coincident(g6,g0)
    c: PointOnObject(g6,g-3)
    c: DistanceX(g6,g6) = 19
    c: PointOnObject(g7,g-3)
    c: DistanceX(g7,g6) = 12
    c: Coincident(g7,g3)
    c: PointOnObject(g8,g-3)
    c: PointOnObject(g8,g-3)
    c: DistanceX(g8,g8) = 10
    c: DistanceX(g8,g6) = 1
    c: Horizontal(g9)
    c: Vertical(g7,g9)
    c: Vertical(g6,g9)
    c: DistanceY(g9,g7) = 8
    c: Horizontal(g10)
    c: Equal(g8,g10)
    c: DistanceY(g10,g8) = 3
    c: Radius(g11) = 20
    c: Coincident(g11,g6)
    c: Coincident(g11,g9)
    c: Radius(g12) = 20
    c: Coincident(g12,g7)
    c: Coincident(g12,g9)
    c: Equal(g13,g11)
    c: Coincident(g13,g8)
    c: Coincident(g13,g10)
    c: Horizontal(g13,g11)
    c: Equal(g14,g12)
    c: Coincident(g14,g8)
    c: Coincident(g14,g10)
    c: Horizontal(g1,g-6)
FEATURE [Sketcher::SketchObject] Sketch122
  ArcFitTolerance = 1e-06
  AttachmentSupport = -> [Pad011]
  ExternalGeometry = -> [Binder001]
  FullyConstrained = true
  MakeInternals = false
  MapMode = 5
  Placement = pos=(0,-2,0) rot=(1,0,0;1.5708rad)
  sketch-geometry (8):
    g0: LineSegment StartX=-202.765 StartY=20.303 StartZ=0 EndX=-143.955 EndY=20.303 EndZ=0
    g1: ArcOfCircle CenterX=-184.801 CenterY=-67.3089 CenterZ=0 NormalX=0 NormalY=0 NormalZ=1 AngleXU=0 Radius=33.7833 StartAngle=2.70526 EndAngle=3.54053
    g2: LineSegment StartX=-176.685 StartY=-80.4316 StartZ=0 EndX=-215.932 EndY=-80.4316 EndZ=0
    g3: LineSegment StartX=-215.42 StartY=-53.0315 StartZ=0 EndX=-192.176 EndY=-3.18454 EndZ=0
    g4: ArcOfCircle CenterX=-207.583 CenterY=4 CenterZ=0 NormalX=0 NormalY=0 NormalZ=1 AngleXU=0 Radius=17 StartAngle=5.84685 EndAngle=7.56663
    g5: Circle CenterX=-213.443 CenterY=-76.8316 CenterZ=0 NormalX=0 NormalY=0 NormalZ=1 AngleXU=0 Radius=3
    g6: Circle CenterX=-179.305 CenterY=-76.8316 CenterZ=0 NormalX=0 NormalY=0 NormalZ=1 AngleXU=0 Radius=3
    g7: LineSegment StartX=-143.955 StartY=20.303 StartZ=0 EndX=-176.685 EndY=-80.4316 EndZ=0
  constraints (18):
    c: Coincident(g0,g-6)
    c: Coincident(g1,g-7)
    c: Coincident(g1,g-8)
    c: Coincident(g2,g1)
    c: Tangent(g3,g-5)
    c: Coincident(g4,g-6)
    c: Coincident(g4,g0)
    c: Coincident(g3,g4)
    c: Coincident(g1,g3)
    c: Diameter(g5) = 6
    c: Diameter(g6) = 6
    c: Coincident(g5,g-9)
    c: Coincident(g6,g-10)
    c: Horizontal(g0)
    c: Horizontal(g2)
    c: Coincident(g7,g0)
    c: Coincident(g7,g2)
    c: Tangent(g7,g-4)
FEATURE [Sketcher::SketchObject] Sketch123
  ArcFitTolerance = 1e-06
  AttachmentSupport = -> [Pad011]
  ExternalGeometry = -> [Binder001]
  FullyConstrained = true
  MakeInternals = false
  MapMode = 5
  Placement = pos=(0,-2,0) rot=(1,0,0;1.5708rad)
  sketch-geometry (4):
    g0: LineSegment StartX=-108 StartY=36.8 StartZ=0 EndX=-90 EndY=36.8 EndZ=0
    g1: LineSegment StartX=-108 StartY=36.8 StartZ=0 EndX=-108 EndY=26.8 EndZ=0
    g2: LineSegment StartX=-108 StartY=26.8 StartZ=0 EndX=-90 EndY=26.8 EndZ=0
    g3: ArcOfCircle CenterX=-94 CenterY=31.8 CenterZ=0 NormalX=0 NormalY=0 NormalZ=1 AngleXU=0 Radius=6.40312 StartAngle=5.38713 EndAngle=7.17924
  constraints (13):
    c: Horizontal(g0)
    c: Coincident(g1,g0)
    c: Vertical(g1)
    c: Coincident(g2,g1)
    c: Horizontal(g2)
    c: DistanceX(g0,g0) = 18
    c: DistanceY(g1,g1) = 10
    c: Equal(g0,g2)
    c: DistanceX(g0,g-3) = 90
    c: DistanceY(g0,g-3) = 2.4
    c: Coincident(g3,g0)
    c: Coincident(g3,g2)
    c: DistanceX(g3,g0) = 4
FEATURE [PartDesign::Chamfer] Chamfer014
  Angle = 45
  Base = -> Pad011 [Edge80,Edge4,Edge7]
  BaseFeature = -> Pad011
  ChamferType = 0
  FlipDirection = false
  Refine = true
  Size = 1.9
  Size2 = 1
  SupportTransform = false
  Suppressed = false
  UseAllEdges = false
FEATURE [PartDesign::Pocket] Pocket006
  BaseFeature = -> Chamfer014
  Direction = (0,-1,2e-16)
  Length = 1.2
  Length2 = 5
  Profile = -> Sketch115
  ReferenceAxis = -> Sketch115 [N_Axis]
  Refine = true
  Suppressed = false
  Type = 0
FEATURE [Sketcher::SketchObject] Sketch116  label="Sketch116 - pieno per inserto M3 x 3 x 4,5"
  ArcFitTolerance = 1e-06
  AttachmentSupport = -> [Pocket006]
  ExternalGeometry = -> [Binder001]
  FullyConstrained = true
  MakeInternals = false
  MapMode = 5
  Placement = pos=(0,1.7e-15,0) rot=(0,0.707107,0.707107;3.14159rad)
  sketch-geometry (4):
    g0: Circle CenterX=43.2 CenterY=30.3 CenterZ=0 NormalX=0 NormalY=0 NormalZ=1 AngleXU=0 Radius=3.4
    g1: Circle CenterX=43.2 CenterY=12.1 CenterZ=0 NormalX=0 NormalY=0 NormalZ=1 AngleXU=0 Radius=3.4
    g2: Circle CenterX=18.6 CenterY=30.3 CenterZ=0 NormalX=0 NormalY=0 NormalZ=1 AngleXU=0 Radius=3.4
    g3: Circle CenterX=18.6 CenterY=12.1 CenterZ=0 NormalX=0 NormalY=0 NormalZ=1 AngleXU=0 Radius=3.4
  constraints (8):
    c: Diameter(g0) = 6.8
    c: Diameter(g1) = 6.8
    c: Diameter(g2) = 6.8
    c: Diameter(g3) = 6.8
    c: Coincident(g2,g-3)
    c: Coincident(g0,g-4)
    c: Coincident(g3,g-6)
    c: Coincident(g1,g-5)
FEATURE [PartDesign::Pad] Pad012
  BaseFeature = -> Pocket006
  Direction = (0,1,-2e-16)
  Length = 2.4
  Length2 = 10
  Profile = -> Sketch116
  ReferenceAxis = -> Sketch116 [N_Axis]
  Refine = true
  Suppressed = false
  Type = 0
FEATURE [PartDesign::Pocket] Pocket007
  BaseFeature = -> Pad012
  Direction = (0,-1,2e-16)
  Length = 0.6
  Length2 = 2.4
  Profile = -> Sketch117
  ReferenceAxis = -> Sketch117 [N_Axis]
  Refine = true
  Suppressed = false
  Type = 4
FEATURE [PartDesign::Pad] Pad013
  BaseFeature = -> Pocket007
  Direction = (0,-1,2e-16)
  Length = 1.6
  Length2 = 10
  Profile = -> Sketch118
  ReferenceAxis = -> Sketch118 [N_Axis]
  Refine = true
  Suppressed = false
  Type = 0
FEATURE [Sketcher::SketchObject] Sketch119
  ArcFitTolerance = 1e-06
  AttachmentSupport = -> [Pad013]
  ExternalGeometry = -> [Binder001]
  FullyConstrained = true
  MakeInternals = false
  MapMode = 5
  Placement = pos=(0,-3.6,0) rot=(1,0,0;1.5708rad)
  sketch-geometry (21):
    g0: LineSegment [constr] StartX=-82.8 StartY=3.2 StartZ=0 EndX=-82.8 EndY=39.2 EndZ=0
    g1: ArcOfCircle CenterX=-78.51 CenterY=34.8 CenterZ=0 NormalX=0 NormalY=0 NormalZ=1 AngleXU=0 Radius=3.5 StartAngle=4.71239 EndAngle=6.28319
    g2: ArcOfCircle CenterX=-78.51 CenterY=7.6 CenterZ=0 NormalX=0 NormalY=0 NormalZ=1 AngleXU=0 Radius=3.5 StartAngle=0 EndAngle=1.5708
    g3: ArcOfCircle CenterX=-5.6 CenterY=34.8 CenterZ=0 NormalX=0 NormalY=0 NormalZ=1 AngleXU=0 Radius=3.5 StartAngle=3.14159 EndAngle=4.71239
    g4: ArcOfCircle CenterX=-5.6 CenterY=7.6 CenterZ=0 NormalX=0 NormalY=0 NormalZ=1 AngleXU=0 Radius=3.5 StartAngle=1.5708 EndAngle=3.14159
    g5: LineSegment StartX=0 StartY=39.2 StartZ=0 EndX=0 EndY=31.3 EndZ=0
    g6: LineSegment StartX=0 StartY=39.2 StartZ=0 EndX=-9.1 EndY=39.2 EndZ=0
    g7: LineSegment StartX=0 StartY=3.2 StartZ=0 EndX=0 EndY=11.1 EndZ=0
    g8: LineSegment StartX=0 StartY=3.2 StartZ=0 EndX=-9.1 EndY=3.2 EndZ=0
    g9: LineSegment StartX=-82.8 StartY=3.2 StartZ=0 EndX=-75.01 EndY=3.2 EndZ=0
    g10: LineSegment StartX=-82.8 StartY=3.2 StartZ=0 EndX=-82.8 EndY=11.1 EndZ=0
    g11: LineSegment StartX=-82.8 StartY=39.2 StartZ=0 EndX=-82.8 EndY=31.3 EndZ=0
    g12: LineSegment StartX=-82.8 StartY=39.2 StartZ=0 EndX=-75.01 EndY=39.2 EndZ=0
    g13: LineSegment StartX=-82.8 StartY=31.3 StartZ=0 EndX=-78.51 EndY=31.3 EndZ=0
    g14: LineSegment StartX=-75.01 StartY=39.2 StartZ=0 EndX=-75.01 EndY=34.8 EndZ=0
    g15: LineSegment StartX=-82.8 StartY=11.1 StartZ=0 EndX=-78.51 EndY=11.1 EndZ=0
    g16: LineSegment StartX=-75.01 StartY=3.2 StartZ=0 EndX=-75.01 EndY=7.6 EndZ=0
    g17: LineSegment StartX=-9.1 StartY=39.2 StartZ=0 EndX=-9.1 EndY=34.8 EndZ=0
    g18: LineSegment StartX=0 StartY=31.3 StartZ=0 EndX=-5.6 EndY=31.3 EndZ=0
    g19: LineSegment StartX=0 StartY=11.1 StartZ=0 EndX=-5.6 EndY=11.1 EndZ=0
    g20: LineSegment StartX=-9.1 StartY=3.2 StartZ=0 EndX=-9.1 EndY=7.6 EndZ=0
  constraints (51):
    c: Coincident(g0,g-10)
    c: PointOnObject(g0,g-8)
    c: Vertical(g0)
    c: Coincident(g1,g-3)
    c: Coincident(g2,g-4)
    c: Coincident(g3,g-5)
    c: Coincident(g4,g-6)
    c: Radius(g4) = 3.5
    c: Radius(g3) = 3.5
    c: Radius(g1) = 3.5
    c: Radius(g2) = 3.5
    c: Coincident(g5,g-9)
    c: PointOnObject(g5,g-9)
    c: Coincident(g6,g5)
    c: PointOnObject(g6,g-8)
    c: Coincident(g7,g-9)
    c: PointOnObject(g7,g-9)
    c: Coincident(g8,g7)
    c: PointOnObject(g8,g-7)
    c: Coincident(g9,g0)
    c: PointOnObject(g9,g-7)
    c: Coincident(g10,g0)
    c: PointOnObject(g10,g0)
    c: Coincident(g11,g0)
    c: PointOnObject(g11,g0)
    c: Coincident(g12,g0)
    c: PointOnObject(g12,g-8)
    c: Coincident(g13,g11)
    c: Horizontal(g13)
    c: Coincident(g14,g12)
    c: Vertical(g14)
    c: Coincident(g15,g10)
    c: Horizontal(g15)
    c: Coincident(g16,g9)
    c: Vertical(g16)
    c: Coincident(g17,g6)
    c: Vertical(g17)
    c: Coincident(g18,g5)
    c: Horizontal(g18)
    c: Coincident(g19,g7)
    c: Horizontal(g19)
    c: Coincident(g20,g8)
    c: Vertical(g20)
    c: Tangent(g20,g4) = 1.5708
    c: Tangent(g4,g19) = -1.5708
    c: Tangent(g18,g3) = 1.5708
    c: Tangent(g3,g17) = -1.5708
    c: Tangent(g13,g1) = -1.5708
    c: Tangent(g1,g14) = 1.5708
    c: Tangent(g16,g2) = -1.5708
    c: Tangent(g2,g15) = 1.5708
FEATURE [PartDesign::Pocket] Pocket008
  BaseFeature = -> Pad013
  Direction = (0,1,-2e-16)
  Length = 1.6
  Length2 = 5
  Profile = -> Sketch119
  ReferenceAxis = -> Sketch119 [N_Axis]
  Refine = true
  Suppressed = false
  Type = 0
FEATURE [PartDesign::Pad] Pad017
  BaseFeature = -> Pocket008
  Direction = (0,-1,2e-16)
  Length = 1.6
  Length2 = 10
  Profile = -> Sketch123
  ReferenceAxis = -> Sketch123 [N_Axis]
  Refine = true
  Suppressed = false
  Type = 0
FEATURE [Sketcher::SketchObject] Sketch125
  ArcFitTolerance = 1e-06
  AttachmentSupport = -> [Pad017]
  ExternalGeometry = -> [Pad017]
  FullyConstrained = true
  MakeInternals = false
  MapMode = 5
  Placement = pos=(0,-3.6,8e-16) rot=(1,0,0;1.5708rad)
  sketch-geometry (20):
    g0: LineSegment StartX=-108 StartY=35.8 StartZ=0 EndX=-108 EndY=35 EndZ=0
    g1: LineSegment StartX=-108 StartY=35 StartZ=0 EndX=-97 EndY=35 EndZ=0
    g2: LineSegment StartX=-97 StartY=35 StartZ=0 EndX=-97 EndY=35.8 EndZ=0
    g3: LineSegment StartX=-97 StartY=35.8 StartZ=0 EndX=-108 EndY=35.8 EndZ=0
    g4: LineSegment StartX=-108 StartY=28.6 StartZ=0 EndX=-108 EndY=27.8 EndZ=0
    g5: LineSegment StartX=-108 StartY=27.8 StartZ=0 EndX=-97 EndY=27.8 EndZ=0
    g6: LineSegment StartX=-97 StartY=27.8 StartZ=0 EndX=-97 EndY=28.6 EndZ=0
    g7: LineSegment StartX=-97 StartY=28.6 StartZ=0 EndX=-108 EndY=28.6 EndZ=0
    g8: LineSegment StartX=-108 StartY=30.4 StartZ=0 EndX=-108 EndY=29.6 EndZ=0
    g9: LineSegment StartX=-108 StartY=29.6 StartZ=0 EndX=-97 EndY=29.6 EndZ=0
    g10: LineSegment StartX=-97 StartY=29.6 StartZ=0 EndX=-97 EndY=30.4 EndZ=0
    g11: LineSegment StartX=-97 StartY=30.4 StartZ=0 EndX=-108 EndY=30.4 EndZ=0
    g12: LineSegment StartX=-108 StartY=32.2 StartZ=0 EndX=-108 EndY=31.4 EndZ=0
    g13: LineSegment StartX=-108 StartY=31.4 StartZ=0 EndX=-97 EndY=31.4 EndZ=0
    g14: LineSegment StartX=-97 StartY=31.4 StartZ=0 EndX=-97 EndY=32.2 EndZ=0
    g15: LineSegment StartX=-97 StartY=32.2 StartZ=0 EndX=-108 EndY=32.2 EndZ=0
    g16: LineSegment StartX=-108 StartY=34 StartZ=0 EndX=-108 EndY=33.2 EndZ=0
    g17: LineSegment StartX=-108 StartY=33.2 StartZ=0 EndX=-97 EndY=33.2 EndZ=0
    g18: LineSegment StartX=-97 StartY=33.2 StartZ=0 EndX=-97 EndY=34 EndZ=0
    g19: LineSegment StartX=-97 StartY=34 StartZ=0 EndX=-108 EndY=34 EndZ=0
  constraints (55):
    c: Coincident(g1,g0)
    c: Horizontal(g1)
    c: Coincident(g2,g1)
    c: Vertical(g2)
    c: Coincident(g3,g2)
    c: Horizontal(g3)
    c: Coincident(g3,g0)
    c: DistanceX(g1,g1) = 11
    c: DistanceY(g2,g2) = 0.8
    c: Coincident(g5,g4)
    c: Horizontal(g5)
    c: Coincident(g6,g5)
    c: Vertical(g6)
    c: Coincident(g7,g6)
    c: Horizontal(g7)
    c: Coincident(g7,g4)
    c: Coincident(g9,g8)
    c: Horizontal(g9)
    c: Coincident(g10,g9)
    c: Vertical(g10)
    c: Coincident(g11,g10)
    c: Horizontal(g11)
    c: Coincident(g11,g8)
    c: Coincident(g13,g12)
    c: Horizontal(g13)
    c: Coincident(g14,g13)
    c: Vertical(g14)
    c: Coincident(g15,g14)
    c: Horizontal(g15)
    c: Coincident(g15,g12)
    c: Coincident(g17,g16)
    c: Horizontal(g17)
    c: Coincident(g18,g17)
    c: Vertical(g18)
    c: Coincident(g19,g18)
    c: Horizontal(g19)
    c: Coincident(g19,g16)
    c: Equal(g3,g19)
    c: Equal(g3,g15)
    c: Equal(g3,g11)
    c: Equal(g3,g7)
    c: Equal(g2,g18)
    c: Equal(g2,g14)
    c: Equal(g2,g10)
    c: Equal(g2,g6)
    c: DistanceY(g-4,g4) = 1
    c: DistanceY(g4,g8) = 1
    c: DistanceY(g8,g12) = 1
    c: DistanceY(g12,g16) = 1
    c: DistanceY(g16,g0) = 1
    c: Tangent(g0,g-5)
    c: Tangent(g16,g-5)
    c: Tangent(g12,g-5)
    c: Tangent(g8,g-5)
    c: Tangent(g4,g-5)
FEATURE [PartDesign::Chamfer] Chamfer009
  Angle = 45
  Base = -> Pad017 [Edge151,Edge154]
  BaseFeature = -> Pad017
  ChamferType = 1
  FlipDirection = false
  Refine = true
  Size = 1.5
  Size2 = 2.8
  SupportTransform = false
  Suppressed = false
  UseAllEdges = false
FEATURE [PartDesign::Pocket] Pocket009
  BaseFeature = -> Chamfer009
  Direction = (0,1,-2e-16)
  Length = 1
  Length2 = 5
  Profile = -> Sketch125
  ReferenceAxis = -> Sketch125 [N_Axis]
  Refine = true
  Suppressed = false
  Type = 0
FEATURE [PartDesign::Pad] Pad014
  BaseFeature = -> Pocket009
  Direction = (0,-1,2e-16)
  Length = 0.8
  Length2 = 10
  Profile = -> Sketch120
  ReferenceAxis = -> Sketch120 [N_Axis]
  Refine = true
  Suppressed = false
  Type = 0
FEATURE [Sketcher::SketchObject] Sketch124
  ArcFitTolerance = 1e-06
  AttachmentSupport = -> [Pad014]
  ExternalGeometry = -> [Binder001]
  FullyConstrained = true
  MakeInternals = false
  MapMode = 5
  Placement = pos=(0,-2.8,6e-16) rot=(1,0,0;1.5708rad)
  sketch-geometry (4):
    g0: LineSegment StartX=-129 StartY=39.2 StartZ=0 EndX=-131.599 EndY=31.2 EndZ=0
    g1: LineSegment StartX=-118 StartY=39.2 StartZ=0 EndX=-120.599 EndY=31.2 EndZ=0
    g2: LineSegment StartX=-129 StartY=39.2 StartZ=0 EndX=-118 EndY=39.2 EndZ=0
    g3: LineSegment StartX=-120.599 StartY=31.2 StartZ=0 EndX=-131.599 EndY=31.2 EndZ=0
  constraints (12):
    c: PointOnObject(g0,g-3)
    c: PointOnObject(g1,g-3)
    c: Parallel(g-4,g0)
    c: Parallel(g-4,g1)
    c: Coincident(g2,g0)
    c: Coincident(g2,g1)
    c: DistanceX(g2,g2) = 11
    c: DistanceY(g1,g1) = 8
    c: Coincident(g3,g1)
    c: Horizontal(g3)
    c: Coincident(g3,g0)
    c: DistanceX(g1,g-3) = 118
FEATURE [PartDesign::Pad] Pad018
  BaseFeature = -> Pad014
  Direction = (0,-1,2e-16)
  Length = 1.2
  Length2 = 10
  Profile = -> Sketch124
  ReferenceAxis = -> Sketch124 [N_Axis]
  Refine = true
  Suppressed = false
  Type = 0
FEATURE [Sketcher::SketchObject] Sketch126
  ArcFitTolerance = 1e-06
  AttachmentSupport = -> [Pad018]
  ExternalGeometry = -> [Pad018]
  FullyConstrained = true
  MakeInternals = false
  MapMode = 5
  Placement = pos=(0,-4,0) rot=(1,0,0;1.5708rad)
  sketch-geometry (8):
    g0: LineSegment StartX=-129.877 StartY=36.5 StartZ=0 EndX=-130.137 EndY=35.7 EndZ=0
    g1: LineSegment StartX=-130.69 StartY=34 StartZ=0 EndX=-130.95 EndY=33.2 EndZ=0
    g2: LineSegment StartX=-129.877 StartY=36.5 StartZ=0 EndX=-118.877 EndY=36.5 EndZ=0
    g3: LineSegment StartX=-130.137 StartY=35.7 StartZ=0 EndX=-119.137 EndY=35.7 EndZ=0
    g4: LineSegment StartX=-130.69 StartY=34 StartZ=0 EndX=-119.69 EndY=34 EndZ=0
    g5: LineSegment StartX=-130.95 StartY=33.2 StartZ=0 EndX=-119.95 EndY=33.2 EndZ=0
    g6: LineSegment StartX=-118.877 StartY=36.5 StartZ=0 EndX=-119.137 EndY=35.7 EndZ=0
    g7: LineSegment StartX=-119.69 StartY=34 StartZ=0 EndX=-119.95 EndY=33.2 EndZ=0
  constraints (20):
    c: Coincident(g2,g0)
    c: Horizontal(g2)
    c: Coincident(g3,g0)
    c: Horizontal(g3)
    c: Coincident(g4,g1)
    c: Horizontal(g4)
    c: Coincident(g5,g1)
    c: Horizontal(g5)
    c: Coincident(g6,g2)
    c: Coincident(g6,g3)
    c: Coincident(g7,g4)
    c: Coincident(g7,g5)
    c: Tangent(g0,g-4)
    c: Tangent(g6,g-5)
    c: Tangent(g1,g-4)
    c: Tangent(g7,g-5)
    c: DistanceY(g3,g2) = 0.8
    c: DistanceY(g5,g4) = 0.8
    c: DistanceY(g-6,g1) = 2
    c: DistanceY(g-6,g0) = 4.5
FEATURE [PartDesign::Chamfer] Chamfer008
  Angle = 45
  Base = -> Pad018 [Edge257]
  BaseFeature = -> Pad018
  ChamferType = 1
  FlipDirection = false
  Refine = true
  Size = 1
  Size2 = 6
  SupportTransform = false
  Suppressed = false
  UseAllEdges = false
FEATURE [PartDesign::Pocket] Pocket010
  BaseFeature = -> Chamfer008
  Direction = (0,1,-2e-16)
  Length = 1
  Length2 = 5
  Profile = -> Sketch126
  ReferenceAxis = -> Sketch126 [N_Axis]
  Refine = true
  Suppressed = false
  Type = 0
FEATURE [PartDesign::Pad] Pad015
  BaseFeature = -> Pocket010
  Direction = (0,-1,2e-16)
  Length = 2
  Length2 = 10
  Profile = -> Sketch121
  ReferenceAxis = -> Sketch121 [N_Axis]
  Refine = true
  Suppressed = false
  Type = 0
FEATURE [PartDesign::Pad] Pad016
  BaseFeature = -> Pad015
  Direction = (0,-1,2e-16)
  Length = 1.6
  Length2 = 10
  Profile = -> Sketch122
  ReferenceAxis = -> Sketch122 [N_Axis]
  Refine = true
  Suppressed = false
  Type = 0
FEATURE [Sketcher::SketchObject] Sketch129
  ArcFitTolerance = 1e-06
  AttachmentSupport = -> [Pad016]
  ExternalGeometry = -> [Binder001]
  FullyConstrained = true
  MakeInternals = false
  MapMode = 5
  Placement = pos=(0,-3.6,0) rot=(1,0,0;1.5708rad)
  sketch-geometry (12):
    g0: LineSegment [constr] StartX=-192.176 StartY=-3.18451 StartZ=0 EndX=-181.223 EndY=20.303 EndZ=0
    g1: LineSegment [constr] StartX=-202.765 StartY=20.303 StartZ=0 EndX=-181.223 EndY=20.303 EndZ=0
    g2: LineSegment StartX=-202.765 StartY=20.303 StartZ=0 EndX=-181.223 EndY=20.303 EndZ=0
    g3: LineSegment StartX=-192.176 StartY=-3.18451 StartZ=0 EndX=-196.804 EndY=-13.1107 EndZ=0
    g4: ArcOfCircle CenterX=-207.583 CenterY=4 CenterZ=0 NormalX=0 NormalY=0 NormalZ=1 AngleXU=0 Radius=17 StartAngle=5.84685 EndAngle=7.56663
    g5: ArcOfEllipse CenterX=-181.223 CenterY=8.55923 CenterZ=0 NormalX=0 NormalY=0 NormalZ=1 MajorRadius=23.4779 MinorRadius=11.7437 AngleXU=2e-16 StartAngle=4.71239 EndAngle=7.85398
    g6: LineSegment [constr] StartX=-157.745 StartY=8.55923 StartZ=0 EndX=-204.701 EndY=8.55923 EndZ=0
    g7: LineSegment [constr] StartX=-181.223 StartY=20.303 StartZ=0 EndX=-181.223 EndY=-3.18451 EndZ=0
    g8: GeomPoint [constr] X=-160.894 Y=8.55923 Z=0
    g9: GeomPoint [constr] X=-201.553 Y=8.55923 Z=0
    g10: ArcOfCircle CenterX=-181.223 CenterY=-20.3763 CenterZ=0 NormalX=0 NormalY=0 NormalZ=1 AngleXU=0 Radius=17.1918 StartAngle=1.57079 EndAngle=2.70526
    g11: GeomPoint [constr] X=-181.223 Y=-3.18451 Z=0
  constraints (23):
    c: Coincident(g0,g-5)
    c: Coincident(g1,g-6)
    c: Horizontal(g1)
    c: Coincident(g1,g0)
    c: Parallel(g0,g-4)
    c: Coincident(g2,g1)
    c: Coincident(g2,g0)
    c: Coincident(g3,g0)
    c: Equal(g4,g-5)
    c: Coincident(g4,g1)
    c: Coincident(g4,g0)
    c: InternalAlignment(g6-g9 -> g5) x4
    c: Vertical(g5,g0)
    c: Horizontal(g6)
    c: Coincident(g5,g0)
    c: DistanceX(g6,g-3) = 10.1
    c: Tangent(g10,g3) = -1.5708
    c: PointOnObject(g11,g10)
    c: Tangent(g5,g10,g11) = 1.5708
    c: Coincident(g10,g5)
    c: Coincident(g11,g7)
    c: Parallel(g3,g-4)
    c: Horizontal(g5,g0)
FEATURE [Sketcher::SketchObject] Sketch130
  ArcFitTolerance = 1e-06
  AttachmentOffset = pos=(0,0,-1.6) rot=(0,0,1;0rad)
  AttachmentSupport = -> [Pad016]
  ExternalGeometry = -> [Binder001]
  FullyConstrained = true
  MakeInternals = false
  MapMode = 5
  Placement = pos=(0,-2,-4e-16) rot=(1,0,0;1.5708rad)
  sketch-geometry (12):
    g0: LineSegment [constr] StartX=-192.176 StartY=-3.18451 StartZ=0 EndX=-181.223 EndY=20.303 EndZ=0
    g1: LineSegment [constr] StartX=-202.765 StartY=20.303 StartZ=0 EndX=-181.223 EndY=20.303 EndZ=0
    g2: LineSegment StartX=-202.765 StartY=20.303 StartZ=0 EndX=-181.223 EndY=20.303 EndZ=0
    g3: LineSegment StartX=-192.176 StartY=-3.18451 StartZ=0 EndX=-193.827 EndY=-6.72678 EndZ=0
    g4: ArcOfCircle CenterX=-207.583 CenterY=4 CenterZ=0 NormalX=0 NormalY=0 NormalZ=1 AngleXU=0 Radius=17 StartAngle=5.84685 EndAngle=7.56663
    g5: ArcOfEllipse CenterX=-181.223 CenterY=10.803 CenterZ=0 NormalX=0 NormalY=0 NormalZ=1 MajorRadius=14.4779 MinorRadius=9.5 AngleXU=0 StartAngle=4.71239 EndAngle=7.85398
    g6: LineSegment [constr] StartX=-166.745 StartY=10.803 StartZ=0 EndX=-195.701 EndY=10.803 EndZ=0
    g7: LineSegment [constr] StartX=-181.223 StartY=20.303 StartZ=0 EndX=-181.223 EndY=1.30297 EndZ=0
    g8: GeomPoint [constr] X=-170.298 Y=10.803 Z=0
    g9: GeomPoint [constr] X=-192.148 Y=10.803 Z=0
    g10: ArcOfCircle CenterX=-181.223 CenterY=-12.6042 CenterZ=0 NormalX=0 NormalY=0 NormalZ=1 AngleXU=0 Radius=13.9072 StartAngle=1.5708 EndAngle=2.70526
    g11: GeomPoint [constr] X=-181.223 Y=1.30297 Z=0
  constraints (23):
    c: Coincident(g0,g-5)
    c: Coincident(g1,g-6)
    c: Horizontal(g1)
    c: Coincident(g1,g0)
    c: Parallel(g0,g-4)
    c: Coincident(g2,g1)
    c: Coincident(g2,g0)
    c: Coincident(g3,g0)
    c: Equal(g4,g-5)
    c: Coincident(g4,g1)
    c: Coincident(g4,g0)
    c: InternalAlignment(g6-g9 -> g5) x4
    c: Vertical(g5,g0)
    c: Horizontal(g6)
    c: Coincident(g5,g0)
    c: DistanceX(g6,g-3) = 19.1
    c: Tangent(g10,g3) = -1.5708
    c: PointOnObject(g11,g10)
    c: Tangent(g5,g10,g11) = 1.5708
    c: Coincident(g10,g5)
    c: Coincident(g11,g7)
    c: Parallel(g3,g-4)
    c: DistanceY(g5,g0) = 19
FEATURE [Part::Part2DObjectPython] Clone2D001  label="Sketch130 (2D)"  # Draft 2D object (typed FeaturePython)
  Fuse = false
  Objects = -> [Sketch130]
  Placement = pos=(0,-2,-4e-16) rot=(1,0,0;1.5708rad)
  Scale = (1,1,1)
FEATURE [Sketcher::SketchObject] Sketch131
  ArcFitTolerance = 1e-06
  AttachmentOffset = pos=(0,0,-3.5) rot=(0,0,1;0rad)
  AttachmentSupport = -> [Pad016]
  ExternalGeometry = -> [Binder001]
  FullyConstrained = true
  MakeInternals = false
  MapMode = 5
  Placement = pos=(0,-0.1,-8e-16) rot=(1,0,0;1.5708rad)
  sketch-geometry (1):
    g0: GeomPoint X=-197.47 Y=8.55923 Z=0
  constraints (1):
    c: Symmetric(g-6,g-4,g0)
FEATURE [Sketcher::SketchObject] Sketch132
  ArcFitTolerance = 1e-06
  AttachmentSupport = -> [Pad016]
  ExternalGeometry = -> [Binder001]
  FullyConstrained = true
  MakeInternals = false
  MapMode = 5
  Placement = pos=(0,-3.6,0) rot=(1,0,0;1.5708rad)
  sketch-geometry (3):
    g0: LineSegment [constr] StartX=-215.42 StartY=-53.0314 StartZ=0 EndX=-167.782 EndY=-53.0314 EndZ=0
    g1: Circle CenterX=-191.282 CenterY=-53.0314 CenterZ=0 NormalX=0 NormalY=0 NormalZ=1 AngleXU=0 Radius=11.5
    g2: Circle CenterX=-191.282 CenterY=-53.0314 CenterZ=0 NormalX=0 NormalY=0 NormalZ=1 AngleXU=0 Radius=10.7
  constraints (8):
    c: Coincident(g0,g-3)
    c: PointOnObject(g0,g-4)
    c: Horizontal(g0)
    c: Diameter(g1) = 23
    c: PointOnObject(g1,g0)
    c: DistanceX(g1,g0) = 23.5
    c: Diameter(g2) = 21.4
    c: Coincident(g2,g1)
FEATURE [Part::Part2DObjectPython] ShapeString  # Draft 2D object (typed FeaturePython)
  FontFile = <path>
  Fuse = false
  Justification = 6
  JustificationReference = 0
  KeepLeftMargin = false
  MakeFace = true
  ObliqueAngle = 0
  Placement = pos=(-199,-3.6,-57.5) rot=(1,0,0;1.5708rad)
  ScaleToSize = true
  Size = 10
  String = AS
  Tracking = 0
FEATURE [Sketcher::SketchObject] Sketch133
  ArcFitTolerance = 1e-06
  AttachmentSupport = -> [Binder]
  ExternalGeometry = -> [Binder]
  FullyConstrained = true
  MakeInternals = false
  MapMode = 5
  Placement = pos=(0,9e-16,0) rot=(0,0.707107,0.707107;3.14159rad)
  sketch-geometry (30):
    g0: LineSegment StartX=0 StartY=39.2 StartZ=0 EndX=0 EndY=3.2 EndZ=0
    g1: LineSegment StartX=0 StartY=3.2 StartZ=0 EndX=82.8 EndY=3.2 EndZ=0
    g2: LineSegment StartX=82.8 StartY=3.2 StartZ=0 EndX=82.8 EndY=6.2 EndZ=0
    g3: LineSegment StartX=82.8 StartY=6.2 StartZ=0 EndX=91.752 EndY=6.2 EndZ=0
    g4: LineSegment StartX=0 StartY=39.2 StartZ=0 EndX=195.887 EndY=39.2 EndZ=0
    g5: LineSegment StartX=195.887 StartY=39.2 StartZ=0 EndX=202.765 EndY=20.303 EndZ=0
    g6: LineSegment StartX=192.333 StartY=24.9893 StartZ=0 EndX=196.467 EndY=26.4942 EndZ=0
    g7: LineSegment StartX=196.467 StartY=26.4942 StartZ=0 EndX=194.073 EndY=33.0721 EndZ=0
    g8: LineSegment StartX=194.073 StartY=33.0721 StartZ=0 EndX=189.939 EndY=31.5672 EndZ=0
    g9: LineSegment StartX=189.939 StartY=31.5672 StartZ=0 EndX=192.333 EndY=24.9893 EndZ=0
    g10: ArcOfCircle CenterX=107.6 CenterY=4 CenterZ=0 NormalX=0 NormalY=0 NormalZ=1 AngleXU=0 Radius=16 StartAngle=1.5708 EndAngle=3.00366
    g11: LineSegment StartX=107.6 StartY=20 StartZ=0 EndX=132.428 EndY=20 EndZ=0
    g12: ArcOfCircle [constr] CenterX=132.428 CenterY=4 CenterZ=0 NormalX=0 NormalY=0 NormalZ=1 AngleXU=0 Radius=16 StartAngle=0.314159 EndAngle=1.5708
    g13: LineSegment StartX=147.645 StartY=8.94427 StartZ=0 EndX=176.685 EndY=-80.4316 EndZ=0
    g14: LineSegment StartX=176.685 StartY=-80.4316 StartZ=0 EndX=215.932 EndY=-80.4316 EndZ=0
    g15: ArcOfCircle CenterX=207.583 CenterY=4 CenterZ=0 NormalX=0 NormalY=0 NormalZ=1 AngleXU=0 Radius=17 StartAngle=1.85815 EndAngle=3.57792
    g16: ArcOfCircle CenterX=184.801 CenterY=-67.3089 CenterZ=0 NormalX=0 NormalY=0 NormalZ=1 AngleXU=0 Radius=33.7833 StartAngle=5.88425 EndAngle=6.71952
    g17: LineSegment StartX=192.176 StartY=-3.18451 StartZ=0 EndX=215.42 EndY=-53.0314 EndZ=0
    g18: Circle CenterX=5.6 CenterY=34.8 CenterZ=0 NormalX=0 NormalY=0 NormalZ=1 AngleXU=0 Radius=1.8
    g19: Circle CenterX=5.6 CenterY=7.6 CenterZ=0 NormalX=0 NormalY=0 NormalZ=1 AngleXU=0 Radius=1.8
    g20: Circle CenterX=78.51 CenterY=34.8 CenterZ=0 NormalX=0 NormalY=0 NormalZ=1 AngleXU=0 Radius=1.8
    g21: Circle CenterX=78.51 CenterY=7.6 CenterZ=0 NormalX=0 NormalY=0 NormalZ=1 AngleXU=0 Radius=1.8
    g22: Circle CenterX=184.08 CenterY=34.8 CenterZ=0 NormalX=0 NormalY=0 NormalZ=1 AngleXU=0 Radius=1.8
    g23: Circle CenterX=179.305 CenterY=-76.8316 CenterZ=0 NormalX=0 NormalY=0 NormalZ=1 AngleXU=0 Radius=1.8
    g24: Circle CenterX=213.443 CenterY=-76.8316 CenterZ=0 NormalX=0 NormalY=0 NormalZ=1 AngleXU=0 Radius=1.8
    g25: Circle CenterX=19 CenterY=21.2 CenterZ=0 NormalX=0 NormalY=0 NormalZ=1 AngleXU=0 Radius=6.3
    g26: Circle CenterX=42 CenterY=21.2 CenterZ=0 NormalX=0 NormalY=0 NormalZ=1 AngleXU=0 Radius=6.3
    g27: Circle CenterX=65 CenterY=21.2 CenterZ=0 NormalX=0 NormalY=0 NormalZ=1 AngleXU=0 Radius=6.3
    g28: LineSegment StartX=132.428 StartY=20 StartZ=0 EndX=144.053 EndY=20 EndZ=0
    g29: LineSegment StartX=147.645 StartY=8.94427 StartZ=0 EndX=144.053 EndY=20 EndZ=0
  constraints (65):
    c: Coincident(g0,g-4)
    c: Coincident(g0,g-5)
    c: Coincident(g1,g0)
    c: Coincident(g1,g-6)
    c: Coincident(g2,g1)
    c: Coincident(g2,g-7)
    c: Coincident(g3,g2)
    c: Coincident(g3,g-8)
    c: Coincident(g4,g0)
    c: Coincident(g4,g-16)
    c: Coincident(g5,g4)
    c: Coincident(g5,g-16)
    c: Coincident(g6,g-20)
    c: Coincident(g6,g-21)
    c: Coincident(g7,g6)
    c: Coincident(g7,g-23)
    c: Coincident(g8,g7)
    c: Coincident(g8,g-22)
    c: Coincident(g9,g8)
    c: Coincident(g9,g6)
    c: Equal(g10,g-8)
    c: Coincident(g10,g3)
    c: Coincident(g10,g-9)
    c: Coincident(g11,g10)
    c: Coincident(g11,g-10)
    c: Equal(g12,g-10)
    c: Coincident(g12,g11)
    c: Coincident(g12,g-11)
    c: Coincident(g13,g12)
    c: Coincident(g13,g-12)
    c: Coincident(g14,g13)
    c: Coincident(g14,g-13)
    c: Equal(g15,g-15)
    c: Coincident(g15,g5)
    c: Coincident(g15,g-15)
    c: Equal(g16,g-13)
    c: Coincident(g16,g14)
    c: Coincident(g16,g-14)
    c: Coincident(g17,g15)
    c: Coincident(g17,g16)
    c: Equal(g18,g-28)
    c: Equal(g19,g-29)
    c: Equal(g20,g-26)
    c: Equal(g21,g-27)
    c: Equal(g22,g-17)
    c: Equal(g24,g-25)
    c: Equal(g23,g-24)
    c: Coincident(g23,g-24)
    c: Coincident(g24,g-25)
    c: Coincident(g22,g-17)
    c: Coincident(g20,g-26)
    c: Coincident(g21,g-27)
    c: Coincident(g18,g-28)
    c: Coincident(g19,g-29)
    c: Equal(g25,g-30)
    c: Equal(g26,g-31)
    c: Equal(g27,g-32)
    c: Coincident(g25,g-30)
    c: Coincident(g26,g-31)
    c: Coincident(g27,g-32)
    c: Parallel(g28,g11)
    c: Parallel(g29,g13)
    c: Coincident(g28,g11)
    c: Coincident(g29,g12)
    c: Coincident(g29,g28)
FEATURE [PartDesign::Pad] Pad019
  Direction = (0,1,-2e-16)
  Length = 2
  Length2 = 10
  Profile = -> Sketch133
  ReferenceAxis = -> Sketch133 [N_Axis]
  Refine = true
  Suppressed = false
  Type = 0
FEATURE [Sketcher::SketchObject] Sketch091  label="Sketch091 - forma anteriore"
  ArcFitTolerance = 1e-06
  AttachmentSupport = -> [Pad019]
  ExternalGeometry = -> [Binder]
  FullyConstrained = true
  MakeInternals = false
  MapMode = 5
  Placement = pos=(0,2,0) rot=(0,0.707107,0.707107;3.14159rad)
  sketch-geometry (12):
    g0: Circle CenterX=5.6 CenterY=34.8 CenterZ=0 NormalX=0 NormalY=0 NormalZ=1 AngleXU=0 Radius=1.8
    g1: Circle CenterX=5.6 CenterY=7.6 CenterZ=0 NormalX=0 NormalY=0 NormalZ=1 AngleXU=0 Radius=1.8
    g2: Circle CenterX=78.51 CenterY=34.8 CenterZ=0 NormalX=0 NormalY=0 NormalZ=1 AngleXU=0 Radius=1.8
    g3: Circle CenterX=78.51 CenterY=7.6 CenterZ=0 NormalX=0 NormalY=0 NormalZ=1 AngleXU=0 Radius=1.8
    g4: LineSegment StartX=0 StartY=39.2 StartZ=0 EndX=0 EndY=3.2 EndZ=0
    g5: LineSegment StartX=0 StartY=3.2 StartZ=0 EndX=82.8 EndY=3.2 EndZ=0
    g6: LineSegment StartX=82.8 StartY=3.2 StartZ=0 EndX=82.8 EndY=39.2 EndZ=0
    g7: LineSegment StartX=82.8 StartY=39.2 StartZ=0 EndX=0 EndY=39.2 EndZ=0
    g8: ArcOfCircle CenterX=19 CenterY=21.2 CenterZ=0 NormalX=0 NormalY=0 NormalZ=1 AngleXU=0 Radius=10 StartAngle=1.5708 EndAngle=4.71239
    g9: ArcOfCircle CenterX=65 CenterY=21.2 CenterZ=0 NormalX=0 NormalY=0 NormalZ=1 AngleXU=0 Radius=10 StartAngle=4.71239 EndAngle=7.85398
    g10: LineSegment StartX=19 StartY=31.2 StartZ=0 EndX=65 EndY=31.2 EndZ=0
    g11: LineSegment StartX=19 StartY=11.2 StartZ=0 EndX=65 EndY=11.2 EndZ=0
  constraints (25):
    c: Equal(g2,g-7)
    c: Equal(g3,g-8)
    c: Equal(g1,g-13)
    c: Equal(g0,g-12)
    c: Coincident(g0,g-12)
    c: Coincident(g1,g-13)
    c: Coincident(g3,g-8)
    c: Coincident(g2,g-7)
    c: Coincident(g4,g-4)
    c: Coincident(g4,g-5)
    c: Coincident(g5,g4)
    c: Coincident(g5,g-6)
    c: Coincident(g6,g5)
    c: PointOnObject(g6,g-3)
    c: Vertical(g6)
    c: Coincident(g7,g6)
    c: Coincident(g7,g4)
    c: Tangent(g8,g10) = 1.5708
    c: Tangent(g8,g11) = -1.5708
    c: Tangent(g9,g10) = 1.5708
    c: Tangent(g9,g11) = -1.5708
    c: Equal(g8,g9)
    c: Radius(g8) = 10
    c: Coincident(g8,g-11)
    c: Coincident(g9,g-9)
FEATURE [Sketcher::SketchObject] Sketch093  label="Sketch093 - scavi interni pulsanti"
  ArcFitTolerance = 1e-06
  AttachmentSupport = -> [Pad019]
  ExternalGeometry = -> [Binder]
  FullyConstrained = true
  MakeInternals = false
  MapMode = 5
  Placement = pos=(0,1.8e-15,0) rot=(1,0,0;1.5708rad)
  sketch-geometry (3):
    g0: Circle CenterX=-65 CenterY=21.2 CenterZ=0 NormalX=0 NormalY=0 NormalZ=1 AngleXU=0 Radius=7.3
    g1: Circle CenterX=-42 CenterY=21.2 CenterZ=0 NormalX=0 NormalY=0 NormalZ=1 AngleXU=0 Radius=7.3
    g2: Circle CenterX=-19 CenterY=21.2 CenterZ=0 NormalX=0 NormalY=0 NormalZ=1 AngleXU=0 Radius=7.3
  constraints (6):
    c: Coincident(g0,g-3)
    c: Coincident(g1,g-4)
    c: Coincident(g2,g-5)
    c: Diameter(g0) = 14.6
    c: Diameter(g1) = 14.6
    c: Diameter(g2) = 14.6
FEATURE [Sketcher::SketchObject] Sketch094  label="Sketch094 - forma centrale"
  ArcFitTolerance = 1e-06
  AttachmentSupport = -> [Pad019]
  ExternalGeometry = -> [Binder]
  FullyConstrained = true
  MakeInternals = false
  MapMode = 5
  Placement = pos=(0,2,0) rot=(0,0.707107,0.707107;3.14159rad)
  sketch-geometry (4):
    g0: LineSegment StartX=137.815 StartY=39.2 StartZ=0 EndX=142.655 EndY=24.303 EndZ=0
    g1: LineSegment StartX=110.815 StartY=24.303 StartZ=0 EndX=142.655 EndY=24.303 EndZ=0
    g2: LineSegment StartX=137.815 StartY=39.2 StartZ=0 EndX=110.815 EndY=39.2 EndZ=0
    g3: ArcOfCircle CenterX=92.2534 CenterY=31.7515 CenterZ=0 NormalX=0 NormalY=0 NormalZ=1 AngleXU=0 Radius=20 StartAngle=5.90156 EndAngle=6.66481
  constraints (12):
    c: PointOnObject(g0,g-3)
    c: Tangent(g0,g-5)
    c: Horizontal(g1)
    c: Coincident(g1,g0)
    c: Coincident(g2,g0)
    c: PointOnObject(g2,g-3)
    c: DistanceX(g2,g2) = 27
    c: Vertical(g1,g2)
    c: Coincident(g3,g2)
    c: Radius(g3) = 20
    c: Coincident(g3,g1)
    c: DistanceY(g-6,g0) = 4
FEATURE [Sketcher::SketchObject] Sketch095  label="Sketch095 - forma posteriore"
  ArcFitTolerance = 1e-06
  AttachmentSupport = -> [Pad019]
  ExternalGeometry = -> [Binder]
  FullyConstrained = true
  MakeInternals = false
  MapMode = 5
  Placement = pos=(0,2,0) rot=(0,0.707107,0.707107;3.14159rad)
  sketch-geometry (15):
    g0: LineSegment StartX=137.815 StartY=39.2 StartZ=0 EndX=143.955 EndY=20.303 EndZ=0
    g1: LineSegment StartX=143.955 StartY=20.303 StartZ=0 EndX=190.141 EndY=20.303 EndZ=0
    g2: ArcOfCircle CenterX=184.08 CenterY=34.8 CenterZ=0 NormalX=0 NormalY=0 NormalZ=1 AngleXU=0 Radius=3.5 StartAngle=3.49066 EndAngle=4.71239
    g3: LineSegment StartX=180.791 StartY=33.6029 StartZ=0 EndX=178.754 EndY=39.2 EndZ=0
    g4: LineSegment StartX=184.08 StartY=31.3 StartZ=0 EndX=186.139 EndY=31.3 EndZ=0
    g5: LineSegment StartX=190.141 StartY=20.303 StartZ=0 EndX=186.139 EndY=31.3 EndZ=0
    g6: LineSegment StartX=137.815 StartY=39.2 StartZ=0 EndX=156.815 EndY=39.2 EndZ=0
    g7: LineSegment StartX=178.754 StartY=39.2 StartZ=0 EndX=168.815 EndY=39.2 EndZ=0
    g8: LineSegment StartX=156.815 StartY=31.2 StartZ=0 EndX=168.815 EndY=31.2 EndZ=0
    g9: ArcOfCircle CenterX=176.411 CenterY=35.2 CenterZ=0 NormalX=0 NormalY=0 NormalZ=1 AngleXU=0 Radius=20 StartAngle=2.94023 EndAngle=3.34295
    g10: ArcOfCircle CenterX=188.411 CenterY=35.2 CenterZ=0 NormalX=0 NormalY=0 NormalZ=1 AngleXU=0 Radius=20 StartAngle=2.94023 EndAngle=3.34295
    g11: LineSegment StartX=157.815 StartY=39.2 StartZ=0 EndX=167.815 EndY=39.2 EndZ=0
    g12: LineSegment StartX=157.436 StartY=36.2 StartZ=0 EndX=167.436 EndY=36.2 EndZ=0
    g13: ArcOfCircle CenterX=177.411 CenterY=35.2 CenterZ=0 NormalX=0 NormalY=0 NormalZ=1 AngleXU=0 Radius=20 StartAngle=2.94023 EndAngle=3.09157
    g14: ArcOfCircle CenterX=187.411 CenterY=35.2 CenterZ=0 NormalX=0 NormalY=0 NormalZ=1 AngleXU=0 Radius=20 StartAngle=2.94023 EndAngle=3.09157
  constraints (46):
    c: PointOnObject(g0,g-3)
    c: Tangent(g0,g-6)
    c: Coincident(g1,g0)
    c: Horizontal(g1)
    c: Radius(g2) = 3.5
    c: Coincident(g2,g-5)
    c: PointOnObject(g3,g-3)
    c: Parallel(g3,g-4)
    c: Tangent(g3,g2) = 1.5708
    c: Horizontal(g4)
    c: Tangent(g4,g2) = -1.5708
    c: Coincident(g5,g1)
    c: Parallel(g5,g-4)
    c: Coincident(g5,g4)
    c: DistanceX(g4,g-8) = 3.8
    c: Coincident(g6,g0)
    c: PointOnObject(g6,g-3)
    c: Coincident(g7,g3)
    c: PointOnObject(g7,g-3)
    c: Horizontal(g8)
    c: DistanceX(g6,g7) = 12
    c: Vertical(g8,g6)
    c: Vertical(g7,g8)
    c: DistanceY(g8,g6) = 8
    c: Coincident(g9,g8)
    c: Coincident(g9,g6)
    c: Coincident(g10,g7)
    c: Coincident(g10,g8)
    c: Radius(g9) = 20
    c: Radius(g10) = 20
    c: PointOnObject(g11,g-3)
    c: PointOnObject(g11,g-3)
    c: DistanceX(g11,g11) = 10
    c: DistanceX(g6,g11) = 1
    c: Horizontal(g12)
    c: Equal(g12,g11)
    c: DistanceY(g12,g11) = 3
    c: Coincident(g13,g11)
    c: Coincident(g13,g12)
    c: Radius(g13) = 20
    c: Coincident(g14,g11)
    c: Coincident(g14,g12)
    c: Radius(g14) = 20
    c: DistanceX(g0,g6) = 19
    c: Horizontal(g9,g13)
    c: Horizontal(g0,g-4)
FEATURE [Sketcher::SketchObject] Sketch096  label="Sketch096 - forma impugnatura"
  ArcFitTolerance = 1e-06
  AttachmentSupport = -> [Pad019]
  ExternalGeometry = -> [Binder]
  FullyConstrained = true
  MakeInternals = false
  MapMode = 5
  Placement = pos=(0,2,0) rot=(0,0.707107,0.707107;3.14159rad)
  sketch-geometry (8):
    g0: LineSegment StartX=176.685 StartY=-80.4316 StartZ=0 EndX=143.955 EndY=20.303 EndZ=0
    g1: LineSegment StartX=176.685 StartY=-80.4316 StartZ=0 EndX=215.932 EndY=-80.4316 EndZ=0
    g2: Circle CenterX=179.305 CenterY=-76.8316 CenterZ=0 NormalX=0 NormalY=0 NormalZ=1 AngleXU=0 Radius=3
    g3: Circle CenterX=213.443 CenterY=-76.8316 CenterZ=0 NormalX=0 NormalY=0 NormalZ=1 AngleXU=0 Radius=3
    g4: LineSegment StartX=143.955 StartY=20.303 StartZ=0 EndX=202.765 EndY=20.303 EndZ=0
    g5: LineSegment StartX=215.42 StartY=-53.0314 StartZ=0 EndX=192.176 EndY=-3.18451 EndZ=0
    g6: ArcOfCircle CenterX=184.801 CenterY=-67.3089 CenterZ=0 NormalX=0 NormalY=0 NormalZ=1 AngleXU=0 Radius=33.7833 StartAngle=5.88425 EndAngle=6.71952
    g7: ArcOfCircle CenterX=207.583 CenterY=4 CenterZ=0 NormalX=0 NormalY=0 NormalZ=1 AngleXU=0 Radius=17 StartAngle=1.85815 EndAngle=3.57792
  constraints (19):
    c: Coincident(g0,g-4)
    c: PointOnObject(g0,g-3)
    c: Horizontal(g0,g-7)
    c: Coincident(g1,g0)
    c: Coincident(g1,g-5)
    c: Diameter(g2) = 6
    c: Diameter(g3) = 6
    c: Coincident(g2,g-9)
    c: Coincident(g3,g-10)
    c: Coincident(g4,g0)
    c: Coincident(g5,g-6)
    c: Coincident(g6,g1)
    c: Coincident(g6,g5)
    c: Equal(g-5,g6)
    c: Coincident(g5,g-7)
    c: Coincident(g4,g-7)
    c: Tangent(g7,g-7)
    c: Coincident(g7,g4)
    c: Coincident(g7,g5)
FEATURE [Sketcher::SketchObject] Sketch097
  ArcFitTolerance = 1e-06
  AttachmentSupport = -> [Pad019]
  ExternalGeometry = -> [Binder]
  FullyConstrained = true
  MakeInternals = false
  MapMode = 5
  Placement = pos=(0,2,0) rot=(0,0.707107,0.707107;3.14159rad)
  sketch-geometry (4):
    g0: LineSegment StartX=90 StartY=36.8 StartZ=0 EndX=108 EndY=36.8 EndZ=0
    g1: LineSegment StartX=108 StartY=36.8 StartZ=0 EndX=108 EndY=26.8 EndZ=0
    g2: LineSegment StartX=108 StartY=26.8 StartZ=0 EndX=90 EndY=26.8 EndZ=0
    g3: ArcOfCircle CenterX=94 CenterY=31.8 CenterZ=0 NormalX=0 NormalY=0 NormalZ=1 AngleXU=0 Radius=6.40312 StartAngle=2.24554 EndAngle=4.03765
  constraints (13):
    c: Horizontal(g0)
    c: Coincident(g1,g0)
    c: Vertical(g1)
    c: DistanceX(g0,g0) = 18
    c: DistanceY(g1,g1) = 10
    c: Coincident(g2,g1)
    c: Horizontal(g2)
    c: Equal(g2,g0)
    c: DistanceY(g0,g-3) = 2.4
    c: Coincident(g3,g0)
    c: Coincident(g3,g2)
    c: DistanceX(g2,g3) = 4
    c: DistanceX(g-3,g0) = 90
FEATURE [PartDesign::Chamfer] Chamfer015
  Angle = 45
  Base = -> Pad019 [Edge19,Edge22,Edge79]
  BaseFeature = -> Pad019
  ChamferType = 0
  FlipDirection = false
  Refine = true
  Size = 1.9
  Size2 = 1
  SupportTransform = false
  Suppressed = false
  UseAllEdges = false
FEATURE [PartDesign::Pocket] Pocket002
  BaseFeature = -> Chamfer015
  Direction = (0,1,-2e-16)
  Length = 1.2
  Length2 = 5
  Profile = -> Sketch093
  ReferenceAxis = -> Sketch093 [N_Axis]
  Refine = true
  Suppressed = false
  Type = 0
FEATURE [PartDesign::Pad] Pad005
  BaseFeature = -> Pocket002
  Direction = (0,1,-2e-16)
  Length = 1.6
  Length2 = 10
  Profile = -> Sketch091
  ReferenceAxis = -> Sketch091 [N_Axis]
  Refine = true
  Suppressed = false
  Type = 0
FEATURE [Sketcher::SketchObject] Sketch092  label="Sketch092 - scavi per viti anteriori"
  ArcFitTolerance = 1e-06
  AttachmentSupport = -> [Pad005]
  ExternalGeometry = -> [Binder]
  FullyConstrained = true
  MakeInternals = false
  MapMode = 5
  Placement = pos=(0,3.6,0) rot=(0,0.707107,0.707107;3.14159rad)
  sketch-geometry (20):
    g0: ArcOfCircle CenterX=5.6 CenterY=7.6 CenterZ=0 NormalX=0 NormalY=0 NormalZ=1 AngleXU=0 Radius=3.5 StartAngle=0 EndAngle=1.5708
    g1: ArcOfCircle CenterX=5.6 CenterY=34.8 CenterZ=0 NormalX=0 NormalY=0 NormalZ=1 AngleXU=0 Radius=3.5 StartAngle=4.71239 EndAngle=6.28319
    g2: ArcOfCircle CenterX=78.51 CenterY=34.8 CenterZ=0 NormalX=0 NormalY=0 NormalZ=1 AngleXU=0 Radius=3.5 StartAngle=3.14159 EndAngle=4.71239
    g3: ArcOfCircle CenterX=78.51 CenterY=7.6 CenterZ=0 NormalX=0 NormalY=0 NormalZ=1 AngleXU=0 Radius=3.5 StartAngle=1.5708 EndAngle=3.14159
    g4: LineSegment StartX=0 StartY=3.2 StartZ=0 EndX=0 EndY=11.1 EndZ=0
    g5: LineSegment StartX=0 StartY=11.1 StartZ=0 EndX=5.6 EndY=11.1 EndZ=0
    g6: LineSegment StartX=0 StartY=3.2 StartZ=0 EndX=9.1 EndY=3.2 EndZ=0
    g7: LineSegment StartX=9.1 StartY=3.2 StartZ=0 EndX=9.1 EndY=7.6 EndZ=0
    g8: LineSegment StartX=0 StartY=39.2 StartZ=0 EndX=0 EndY=31.3 EndZ=0
    g9: LineSegment StartX=0 StartY=31.3 StartZ=0 EndX=5.6 EndY=31.3 EndZ=0
    g10: LineSegment StartX=0 StartY=39.2 StartZ=0 EndX=9.1 EndY=39.2 EndZ=0
    g11: LineSegment StartX=9.1 StartY=39.2 StartZ=0 EndX=9.1 EndY=34.8 EndZ=0
    g12: LineSegment StartX=82.8 StartY=39.2 StartZ=0 EndX=75.01 EndY=39.2 EndZ=0
    g13: LineSegment StartX=82.8 StartY=39.2 StartZ=0 EndX=82.8 EndY=31.3 EndZ=0
    g14: LineSegment StartX=82.8 StartY=31.3 StartZ=0 EndX=78.51 EndY=31.3 EndZ=0
    g15: LineSegment StartX=82.8 StartY=3.2 StartZ=0 EndX=75.01 EndY=3.2 EndZ=0
    g16: LineSegment StartX=75.01 StartY=3.2 StartZ=0 EndX=75.01 EndY=7.6 EndZ=0
    g17: LineSegment StartX=82.8 StartY=3.2 StartZ=0 EndX=82.8 EndY=11.1 EndZ=0
    g18: LineSegment StartX=82.8 StartY=11.1 StartZ=0 EndX=78.51 EndY=11.1 EndZ=0
    g19: LineSegment StartX=75.01 StartY=39.2 StartZ=0 EndX=75.01 EndY=34.8 EndZ=0
  constraints (48):
    c: Radius(g0) = 3.5
    c: Coincident(g0,g-10)
    c: Radius(g1) = 3.5
    c: Coincident(g1,g-9)
    c: Radius(g2) = 3.5
    c: Coincident(g2,g-8)
    c: Radius(g3) = 3.5
    c: Coincident(g3,g-7)
    c: Coincident(g4,g-5)
    c: PointOnObject(g4,g-4)
    c: Coincident(g5,g4)
    c: Horizontal(g5)
    c: Coincident(g6,g4)
    c: PointOnObject(g6,g-5)
    c: Coincident(g7,g6)
    c: Vertical(g7)
    c: Coincident(g8,g-4)
    c: PointOnObject(g8,g-4)
    c: Coincident(g9,g8)
    c: Horizontal(g9)
    c: Coincident(g10,g8)
    c: PointOnObject(g10,g-3)
    c: Coincident(g11,g10)
    c: Vertical(g11)
    c: PointOnObject(g12,g-3)
    c: PointOnObject(g12,g-3)
    c: Coincident(g13,g12)
    c: Vertical(g13)
    c: Coincident(g14,g13)
    c: Horizontal(g14)
    c: Coincident(g15,g-6)
    c: PointOnObject(g15,g-5)
    c: Coincident(g16,g15)
    c: Vertical(g16)
    c: Coincident(g17,g15)
    c: Coincident(g18,g17)
    c: Horizontal(g18)
    c: Tangent(g3,g18) = -1.5708
    c: Tangent(g16,g3) = 1.5708
    c: Coincident(g19,g12)
    c: Vertical(g19)
    c: Tangent(g2,g19) = -1.5708
    c: Tangent(g2,g14) = 1.5708
    c: Tangent(g0,g7) = -1.5708
    c: Tangent(g0,g5) = 1.5708
    c: Tangent(g9,g1) = -1.5708
    c: Tangent(g1,g11) = 1.5708
    c: Tangent(g17,g13)
FEATURE [PartDesign::Pocket] Pocket001
  BaseFeature = -> Pad005
  Direction = (0,-1,2e-16)
  Length = 1.6
  Length2 = 5
  Profile = -> Sketch092
  ReferenceAxis = -> Sketch092 [N_Axis]
  Refine = true
  Suppressed = false
  Type = 0
FEATURE [PartDesign::Pad] Pad006
  BaseFeature = -> Pocket001
  Direction = (0,1,-2e-16)
  Length = 0.8
  Length2 = 10
  Profile = -> Sketch094
  ReferenceAxis = -> Sketch094 [N_Axis]
  Refine = true
  Suppressed = false
  Type = 0
FEATURE [PartDesign::Pad] Pad007
  BaseFeature = -> Pad006
  Direction = (0,1,-2e-16)
  Length = 2
  Length2 = 10
  Profile = -> Sketch095
  ReferenceAxis = -> Sketch095 [N_Axis]
  Refine = true
  Suppressed = false
  Type = 0
FEATURE [PartDesign::Pad] Pad008  label="Pad008 - forma impugnatura"
  BaseFeature = -> Pad007
  Direction = (0,1,-2e-16)
  Length = 1.6
  Length2 = 10
  Profile = -> Sketch096
  ReferenceAxis = -> Sketch096 [N_Axis]
  Refine = true
  Suppressed = false
  Type = 0
FEATURE [PartDesign::Pad] Pad009
  BaseFeature = -> Pad008
  Direction = (0,1,-2e-16)
  Length = 1.6
  Length2 = 10
  Profile = -> Sketch097
  ReferenceAxis = -> Sketch097 [N_Axis]
  Refine = true
  Suppressed = false
  Type = 0
FEATURE [Sketcher::SketchObject] Sketch098
  ArcFitTolerance = 1e-06
  AttachmentSupport = -> [Pad006]
  ExternalGeometry = -> [Binder]
  FullyConstrained = true
  MakeInternals = false
  MapMode = 5
  Placement = pos=(0,2.8,-7e-16) rot=(0,0.707107,0.707107;3.14159rad)
  sketch-geometry (4):
    g0: LineSegment StartX=118 StartY=39.2 StartZ=0 EndX=129 EndY=39.2 EndZ=0
    g1: LineSegment StartX=120.599 StartY=31.2 StartZ=0 EndX=131.599 EndY=31.2 EndZ=0
    g2: LineSegment StartX=129 StartY=39.2 StartZ=0 EndX=131.599 EndY=31.2 EndZ=0
    g3: LineSegment StartX=118 StartY=39.2 StartZ=0 EndX=120.599 EndY=31.2 EndZ=0
  constraints (12):
    c: PointOnObject(g0,g-3)
    c: PointOnObject(g0,g-3)
    c: DistanceX(g0,g0) = 11
    c: Horizontal(g1)
    c: Equal(g1,g0)
    c: Coincident(g2,g0)
    c: Coincident(g3,g0)
    c: Parallel(g-4,g2)
    c: Coincident(g1,g2)
    c: Coincident(g1,g3)
    c: DistanceY(g1,g0) = 8
    c: DistanceX(g-3,g0) = 118
FEATURE [Sketcher::SketchObject] Sketch099
  ArcFitTolerance = 1e-06
  AttachmentSupport = -> [Pad008]
  ExternalGeometry = -> [Binder]
  FullyConstrained = true
  MakeInternals = false
  MapMode = 5
  Placement = pos=(0,3.6,0) rot=(0,0.707107,0.707107;3.14159rad)
  sketch-geometry (13):
    g0: LineSegment StartX=192.176 StartY=-3.18451 StartZ=0 EndX=196.804 EndY=-13.1108 EndZ=0
    g1: LineSegment [constr] StartX=202.765 StartY=20.303 StartZ=0 EndX=181.223 EndY=20.303 EndZ=0
    g2: LineSegment [constr] StartX=181.223 StartY=20.303 StartZ=0 EndX=181.223 EndY=-3.18451 EndZ=0
    g3: ArcOfCircle CenterX=181.223 CenterY=-20.3764 CenterZ=0 NormalX=0 NormalY=0 NormalZ=1 AngleXU=0 Radius=17.1918 StartAngle=0.436332 EndAngle=1.57079
    g4: ArcOfEllipse CenterX=181.223 CenterY=8.55923 CenterZ=0 NormalX=0 NormalY=0 NormalZ=1 MajorRadius=23.4779 MinorRadius=11.7437 AngleXU=0 StartAngle=1.5708 EndAngle=4.71239
    g5: LineSegment [constr] StartX=204.701 StartY=8.55923 StartZ=0 EndX=157.745 EndY=8.55923 EndZ=0
    g6: LineSegment [constr] StartX=181.223 StartY=20.303 StartZ=0 EndX=181.223 EndY=-3.18451 EndZ=0
    g7: GeomPoint [constr] X=201.553 Y=8.55923 Z=0
    g8: GeomPoint [constr] X=160.894 Y=8.55923 Z=0
    g9: GeomPoint [constr] X=181.223 Y=-3.18451 Z=0
    g10: LineSegment StartX=181.223 StartY=20.303 StartZ=0 EndX=202.765 EndY=20.303 EndZ=0
    g11: ArcOfCircle CenterX=207.583 CenterY=4 CenterZ=0 NormalX=0 NormalY=0 NormalZ=1 AngleXU=0 Radius=17 StartAngle=1.85815 EndAngle=3.57792
    g12: LineSegment [constr] StartX=172.411 StartY=39.2 StartZ=0 EndX=192.176 EndY=-3.18451 EndZ=0
  constraints (27):
    c: Coincident(g1,g-7)
    c: Horizontal(g1)
    c: Coincident(g2,g1)
    c: Vertical(g2)
    c: Horizontal(g2,g0)
    c: Coincident(g3,g0)
    c: Coincident(g3,g2)
    c: InternalAlignment(g5-g8 -> g4) x4
    c: Horizontal(g5)
    c: PointOnObject(g4,g2)
    c: Coincident(g4,g1)
    c: DistanceX(g-3,g5) = 10.1
    c: Coincident(g4,g2)
    c: Tangent(g3,g-5)
    c: PointOnObject(g9,g4)
    c: PointOnObject(g9,g3)
    c: Tangent(g4,g3,g9) = 1.5708
    c: Coincident(g10,g1)
    c: Coincident(g10,g1)
    c: Equal(g11,g-4)
    c: Coincident(g11,g1)
    c: Coincident(g11,g0)
    c: PointOnObject(g12,g-6)
    c: PointOnObject(g1,g12)
    c: Tangent(g12,g-5) = -1.5708
    c: Tangent(g0,g-5) = -1.5708
    c: Horizontal(g9,g12)
FEATURE [Sketcher::SketchObject] Sketch106  label="Sketch106 - smusso impuniatura interno"
  ArcFitTolerance = 1e-06
  AttachmentSupport = -> [Pad008]
  ExternalGeometry = -> [Pad008]
  FullyConstrained = true
  MakeInternals = false
  MapMode = 5
  Placement = pos=(0,-1.585e-13,-80.4316) rot=(1,0,0;3.14159rad)
  sketch-geometry (9):
    g0: LineSegment StartX=-176.685 StartY=-3.6 StartZ=0 EndX=-176.685 EndY=8e-15 EndZ=0
    g1: LineSegment [constr] StartX=-176.685 StartY=-7.37e-14 StartZ=0 EndX=-176.685 EndY=8e-15 EndZ=0
    g2: LineSegment [constr] StartX=-186.685 StartY=-3.6 StartZ=0 EndX=-186.685 EndY=8e-15 EndZ=0
    g3: ArcOfEllipse CenterX=-186.685 CenterY=8e-15 CenterZ=0 NormalX=0 NormalY=0 NormalZ=1 MajorRadius=10 MinorRadius=3.6 AngleXU=-3.14159 StartAngle=1.5708 EndAngle=3.14159
    g4: LineSegment [constr] StartX=-196.685 StartY=-5.9e-15 StartZ=0 EndX=-176.685 EndY=-5.9e-15 EndZ=0
    g5: LineSegment [constr] StartX=-186.685 StartY=-3.6 StartZ=0 EndX=-186.685 EndY=3.6 EndZ=0
    g6: GeomPoint [constr] X=-196.015 Y=-9.7e-15 Z=0
    g7: GeomPoint [constr] X=-177.356 Y=-4.9e-15 Z=0
    g8: LineSegment StartX=-176.685 StartY=-3.6 StartZ=0 EndX=-186.685 EndY=-3.6 EndZ=0
  constraints (15):
    c: PointOnObject(g2,g-3)
    c: Coincident(g1,g-5)
    c: DistanceY(g1,g1) = 0
    c: Coincident(g0,g1)
    c: DistanceX(g2,g-5) = 10
    c: Vertical(g2)
    c: Horizontal(g2,g0)
    c: InternalAlignment(g4-g7 -> g3) x4
    c: Coincident(g3,g2)
    c: Horizontal(g4)
    c: Coincident(g3,g0)
    c: Tangent(g0,g-5) = 1.5708
    c: Coincident(g3,g2)
    c: Coincident(g8,g0)
    c: Coincident(g8,g2)
FEATURE [Sketcher::SketchObject] Sketch107  label="Sketch107 - smusso impugnatura esterno"
  ArcFitTolerance = 1e-06
  AttachmentSupport = -> [Pad008]
  ExternalGeometry = -> [Pad008]
  FullyConstrained = true
  MakeInternals = false
  MapMode = 5
  Placement = pos=(0,-1.585e-13,-80.4316) rot=(1,0,0;3.14159rad)
  sketch-geometry (9):
    g0: LineSegment [constr] StartX=-215.932 StartY=-1.416e-13 StartZ=0 EndX=-215.932 EndY=-3.86e-14 EndZ=0
    g1: LineSegment StartX=-215.932 StartY=-3.6 StartZ=0 EndX=-215.932 EndY=-3.86e-14 EndZ=0
    g2: LineSegment StartX=-215.932 StartY=-3.6 StartZ=0 EndX=-205.932 EndY=-3.6 EndZ=0
    g3: LineSegment [constr] StartX=-205.932 StartY=-3.6 StartZ=0 EndX=-205.932 EndY=-3.86e-14 EndZ=0
    g4: ArcOfEllipse CenterX=-205.932 CenterY=-3.86e-14 CenterZ=0 NormalX=0 NormalY=0 NormalZ=1 MajorRadius=10 MinorRadius=3.6 AngleXU=-3.14159 StartAngle=-2.66e-14 EndAngle=1.5708
    g5: LineSegment [constr] StartX=-215.932 StartY=-1.416e-13 StartZ=0 EndX=-195.932 EndY=-1.416e-13 EndZ=0
    g6: LineSegment [constr] StartX=-205.932 StartY=-3.6 StartZ=0 EndX=-205.932 EndY=3.6 EndZ=0
    g7: GeomPoint [constr] X=-215.262 Y=-1.309e-13 Z=0
    g8: GeomPoint [constr] X=-196.602 Y=-1.551e-13 Z=0
  constraints (16):
    c: Coincident(g0,g-6)
    c: PointOnObject(g0,g-6)
    c: DistanceY(g0,g0) = 0
    c: Coincident(g1,g-6)
    c: Coincident(g1,g0)
    c: Tangent(g2,g-3)
    c: DistanceX(g2,g2) = 10
    c: Coincident(g3,g2)
    c: Vertical(g3)
    c: Horizontal(g3,g0)
    c: InternalAlignment(g5-g8 -> g4) x4
    c: Coincident(g4,g3)
    c: Horizontal(g5)
    c: Coincident(g4,g0)
    c: Coincident(g4,g2)
    c: PointOnObject(g2,g1)
FEATURE [Sketcher::SketchObject] Sketch108
  ArcFitTolerance = 1e-06
  AttachmentOffset = pos=(0,0,-1.6) rot=(0,0,1;0rad)
  AttachmentSupport = -> [Pad008]
  ExternalGeometry = -> [Binder]
  FullyConstrained = true
  MakeInternals = false
  MapMode = 5
  Placement = pos=(0,2,4e-16) rot=(0,0.707107,0.707107;3.14159rad)
  sketch-geometry (14):
    g0: LineSegment StartX=192.176 StartY=-3.18451 StartZ=0 EndX=193.827 EndY=-6.72678 EndZ=0
    g1: LineSegment [constr] StartX=202.765 StartY=20.303 StartZ=0 EndX=181.223 EndY=20.303 EndZ=0
    g2: LineSegment [constr] StartX=181.223 StartY=20.303 StartZ=0 EndX=181.223 EndY=1.30297 EndZ=0
    g3: ArcOfCircle CenterX=181.223 CenterY=-12.6042 CenterZ=0 NormalX=0 NormalY=0 NormalZ=1 AngleXU=0 Radius=13.9072 StartAngle=0.436332 EndAngle=1.5708
    g4: ArcOfEllipse CenterX=181.223 CenterY=10.803 CenterZ=0 NormalX=0 NormalY=0 NormalZ=1 MajorRadius=14.4779 MinorRadius=9.5 AngleXU=0 StartAngle=1.5708 EndAngle=4.71239
    g5: LineSegment [constr] StartX=195.701 StartY=10.803 StartZ=0 EndX=166.745 EndY=10.803 EndZ=0
    g6: LineSegment [constr] StartX=181.223 StartY=20.303 StartZ=0 EndX=181.223 EndY=1.30297 EndZ=0
    g7: GeomPoint [constr] X=192.148 Y=10.803 Z=0
    g8: GeomPoint [constr] X=170.298 Y=10.803 Z=0
    g9: LineSegment StartX=181.223 StartY=20.303 StartZ=0 EndX=202.765 EndY=20.303 EndZ=0
    g10: ArcOfCircle CenterX=207.583 CenterY=4 CenterZ=0 NormalX=0 NormalY=0 NormalZ=1 AngleXU=0 Radius=17 StartAngle=1.85815 EndAngle=3.57792
    g11: LineSegment [constr] StartX=172.411 StartY=39.2 StartZ=0 EndX=192.176 EndY=-3.18451 EndZ=0
    g12: GeomPoint [constr] X=181.223 Y=1.30297 Z=0
    g13: GeomPoint [constr] X=181.223 Y=1.30297 Z=0
  constraints (28):
    c: Coincident(g1,g-7)
    c: Horizontal(g1)
    c: Coincident(g2,g1)
    c: Vertical(g2)
    c: Coincident(g3,g2)
    c: InternalAlignment(g5-g8 -> g4) x4
    c: Horizontal(g5)
    c: PointOnObject(g4,g2)
    c: Coincident(g4,g1)
    c: DistanceX(g-3,g5) = 19.1
    c: Coincident(g4,g2)
    c: Coincident(g9,g1)
    c: Coincident(g9,g1)
    c: Coincident(g10,g1)
    c: Coincident(g10,g0)
    c: PointOnObject(g11,g-6)
    c: PointOnObject(g1,g11)
    c: DistanceY(g2,g1) = 19
    c: Coincident(g10,g-4)
    c: PointOnObject(g12,g4)
    c: PointOnObject(g12,g3)
    c: Tangent(g11,g-5) = -1.5708
    c: Tangent(g0,g-5) = -1.5708
    c: Tangent(g3,g0) = 1.5708
    c: PointOnObject(g13,g4)
    c: PointOnObject(g13,g3)
    c: Tangent(g4,g3,g13) = 1.5708
    c: Horizontal(g11,g0)
FEATURE [Part::Part2DObjectPython] Clone2D  label="Sketch108 (2D)"  # Draft 2D object (typed FeaturePython)
  Fuse = false
  Objects = -> [Sketch108]
  Placement = pos=(0,2,4e-16) rot=(0,0.707107,0.707107;3.14159rad)
  Scale = (1,1,1)
FEATURE [Sketcher::SketchObject] Sketch109
  ArcFitTolerance = 1e-06
  AttachmentOffset = pos=(0,0,-3.5) rot=(0,0,1;0rad)
  AttachmentSupport = -> [Pad008]
  ExternalGeometry = -> [Binder]
  FullyConstrained = true
  MakeInternals = false
  MapMode = 5
  Placement = pos=(0,0.1,8e-16) rot=(0,0.707107,0.707107;3.14159rad)
  sketch-geometry (1):
    g0: GeomPoint X=197.47 Y=8.55923 Z=0
  constraints (1):
    c: Symmetric(g-7,g-5,g0)
FEATURE [PartDesign::Chamfer] Chamfer005
  Angle = 45
  Base = -> Pad009 [Edge215,Edge212]
  BaseFeature = -> Pad009
  ChamferType = 1
  FlipDirection = false
  Refine = true
  Size = 1.5
  Size2 = 2.8
  SupportTransform = false
  Suppressed = false
  UseAllEdges = false
FEATURE [Sketcher::SketchObject] Sketch111
  ArcFitTolerance = 1e-06
  AttachmentSupport = -> [Pad009]
  ExternalGeometry = -> [Pad009]
  FullyConstrained = true
  MakeInternals = false
  MapMode = 5
  Placement = pos=(0,3.6,-8e-16) rot=(0,0.707107,0.707107;3.14159rad)
  sketch-geometry (21):
    g0: LineSegment [constr] StartX=97 StartY=36.8 StartZ=0 EndX=97 EndY=26.8 EndZ=0
    g1: LineSegment StartX=97 StartY=28.6 StartZ=0 EndX=97 EndY=27.8 EndZ=0
    g2: LineSegment StartX=97 StartY=27.8 StartZ=0 EndX=108 EndY=27.8 EndZ=0
    g3: LineSegment StartX=108 StartY=27.8 StartZ=0 EndX=108 EndY=28.6 EndZ=0
    g4: LineSegment StartX=108 StartY=28.6 StartZ=0 EndX=97 EndY=28.6 EndZ=0
    g5: LineSegment StartX=97 StartY=35.8 StartZ=0 EndX=97 EndY=35 EndZ=0
    g6: LineSegment StartX=97 StartY=35 StartZ=0 EndX=108 EndY=35 EndZ=0
    g7: LineSegment StartX=108 StartY=35 StartZ=0 EndX=108 EndY=35.8 EndZ=0
    g8: LineSegment StartX=108 StartY=35.8 StartZ=0 EndX=97 EndY=35.8 EndZ=0
    g9: LineSegment StartX=97 StartY=30.4 StartZ=0 EndX=97 EndY=29.6 EndZ=0
    g10: LineSegment StartX=97 StartY=29.6 StartZ=0 EndX=108 EndY=29.6 EndZ=0
    g11: LineSegment StartX=108 StartY=29.6 StartZ=0 EndX=108 EndY=30.4 EndZ=0
    g12: LineSegment StartX=108 StartY=30.4 StartZ=0 EndX=97 EndY=30.4 EndZ=0
    g13: LineSegment StartX=97 StartY=34 StartZ=0 EndX=97 EndY=33.2 EndZ=0
    g14: LineSegment StartX=97 StartY=33.2 StartZ=0 EndX=108 EndY=33.2 EndZ=0
    g15: LineSegment StartX=108 StartY=33.2 StartZ=0 EndX=108 EndY=34 EndZ=0
    g16: LineSegment StartX=108 StartY=34 StartZ=0 EndX=97 EndY=34 EndZ=0
    g17: LineSegment StartX=97 StartY=32.2 StartZ=0 EndX=97 EndY=31.4 EndZ=0
    g18: LineSegment StartX=97 StartY=31.4 StartZ=0 EndX=108 EndY=31.4 EndZ=0
    g19: LineSegment StartX=108 StartY=31.4 StartZ=0 EndX=108 EndY=32.2 EndZ=0
    g20: LineSegment StartX=108 StartY=32.2 StartZ=0 EndX=97 EndY=32.2 EndZ=0
  constraints (54):
    c: Vertical(g0)
    c: PointOnObject(g0,g-3)
    c: PointOnObject(g0,g-4)
    c: DistanceX(g0,g-5) = 11
    c: Coincident(g1,g2)
    c: Coincident(g2,g3)
    c: Coincident(g3,g4)
    c: Coincident(g4,g1)
    c: Horizontal(g2)
    c: Horizontal(g4)
    c: Tangent(g1,g0)
    c: Tangent(g3,g-5)
    c: DistanceY(g2,g3) = 0.8
    c: Coincident(g5,g6)
    c: Coincident(g6,g7)
    c: Coincident(g7,g8)
    c: Coincident(g8,g5)
    c: Horizontal(g6)
    c: Horizontal(g8)
    c: DistanceY(g6,g7) = 0.8
    c: Coincident(g9,g10)
    c: Coincident(g10,g11)
    c: Coincident(g11,g12)
    c: Coincident(g12,g9)
    c: Horizontal(g10)
    c: Horizontal(g12)
    c: DistanceY(g10,g11) = 0.8
    c: Tangent(g5,g0)
    c: Tangent(g7,g-5)
    c: Tangent(g9,g0)
    c: Tangent(g11,g-5)
    c: Coincident(g13,g14)
    c: Coincident(g14,g15)
    c: Coincident(g15,g16)
    c: Coincident(g16,g13)
    c: Horizontal(g14)
    c: Horizontal(g16)
    c: DistanceY(g14,g15) = 0.8
    c: Tangent(g13,g0)
    c: Tangent(g15,g-5)
    c: Coincident(g17,g18)
    c: Coincident(g18,g19)
    c: Coincident(g19,g20)
    c: Coincident(g20,g17)
    c: Horizontal(g18)
    c: Horizontal(g20)
    c: DistanceY(g18,g19) = 0.8
    c: Tangent(g17,g0)
    c: Tangent(g19,g-5)
    c: DistanceY(g1,g9) = 1
    c: DistanceY(g9,g17) = 1
    c: DistanceY(g17,g13) = 1
    c: DistanceY(g13,g5) = 1
    c: DistanceY(g0,g1) = 1
FEATURE [PartDesign::Pocket] Pocket004
  BaseFeature = -> Chamfer005
  Direction = (0,-1,2e-16)
  Length = 1
  Length2 = 5
  Profile = -> Sketch111
  ReferenceAxis = -> Sketch111 [N_Axis]
  Refine = true
  Suppressed = false
  Type = 0
FEATURE [PartDesign::Pad] Pad010
  BaseFeature = -> Pocket004
  Direction = (0,1,-2e-16)
  Length = 1.2
  Length2 = 10
  Profile = -> Sketch098
  ReferenceAxis = -> Sketch098 [N_Axis]
  Refine = true
  Suppressed = false
  Type = 0
FEATURE [PartDesign::Chamfer] Chamfer006
  Angle = 45
  Base = -> Pad010 [Edge291]
  BaseFeature = -> Pad010
  ChamferType = 1
  FlipDirection = false
  Refine = true
  Size = 1
  Size2 = 6
  SupportTransform = false
  Suppressed = false
  UseAllEdges = false
FEATURE [Sketcher::SketchObject] Sketch110
  ArcFitTolerance = 1e-06
  AttachmentSupport = -> [Pad010]
  ExternalGeometry = -> [Sketch098]
  FullyConstrained = true
  MakeInternals = false
  MapMode = 5
  Placement = pos=(0,4,-9e-16) rot=(0,0.707107,0.707107;3.14159rad)
  sketch-geometry (8):
    g0: LineSegment StartX=119.69 StartY=34 StartZ=0 EndX=130.69 EndY=34 EndZ=0
    g1: LineSegment StartX=119.95 StartY=33.2 StartZ=0 EndX=130.95 EndY=33.2 EndZ=0
    g2: LineSegment StartX=119.137 StartY=35.7 StartZ=0 EndX=130.137 EndY=35.7 EndZ=0
    g3: LineSegment StartX=118.877 StartY=36.5 StartZ=0 EndX=129.877 EndY=36.5 EndZ=0
    g4: LineSegment StartX=118.877 StartY=36.5 StartZ=0 EndX=119.137 EndY=35.7 EndZ=0
    g5: LineSegment StartX=129.877 StartY=36.5 StartZ=0 EndX=130.137 EndY=35.7 EndZ=0
    g6: LineSegment StartX=119.69 StartY=34 StartZ=0 EndX=119.95 EndY=33.2 EndZ=0
    g7: LineSegment StartX=130.69 StartY=34 StartZ=0 EndX=130.95 EndY=33.2 EndZ=0
  constraints (24):
    c: Horizontal(g0)
    c: Horizontal(g1)
    c: Horizontal(g2)
    c: Horizontal(g3)
    c: Equal(g1,g-5)
    c: Equal(g0,g-5)
    c: Equal(g2,g-5)
    c: Equal(g3,g-5)
    c: PointOnObject(g0,g-3)
    c: PointOnObject(g1,g-3)
    c: PointOnObject(g2,g-3)
    c: PointOnObject(g3,g-3)
    c: Coincident(g4,g3)
    c: Coincident(g4,g2)
    c: Coincident(g5,g3)
    c: Coincident(g5,g2)
    c: Coincident(g6,g0)
    c: Coincident(g6,g1)
    c: Coincident(g7,g0)
    c: Coincident(g7,g1)
    c: DistanceY(g1,g0) = 0.8
    c: DistanceY(g2,g3) = 0.8
    c: DistanceY(g-5,g1) = 2
    c: DistanceY(g-5,g2) = 4.5
FEATURE [PartDesign::Pocket] Pocket003
  BaseFeature = -> Chamfer006
  Direction = (0,-1,2e-16)
  Length = 1
  Length2 = 5
  Profile = -> Sketch110
  ReferenceAxis = -> Sketch110 [N_Axis]
  Refine = true
  Suppressed = false
  Type = 0
FEATURE [PartDesign::SubtractivePipe] SubtractivePipe
  AuxilleryCurvelinear = true
  AuxillerySpineTangent = false
  BaseFeature = -> Pocket003
  Binormal = (0,0,0)
  Mode = 0
  Profile = -> Sketch106
  Refine = true
  Spine = -> Pad008 [Edge215]
  SpineTangent = false
  Suppressed = false
  Transformation = 0
  Transition = 0
FEATURE [PartDesign::SubtractivePipe] SubtractivePipe001
  AuxilleryCurvelinear = true
  AuxillerySpineTangent = false
  BaseFeature = -> SubtractivePipe
  Binormal = (0,0,0)
  Mode = 0
  Profile = -> Sketch107
  Refine = true
  Spine = -> Pad008 [Edge213,Edge216,Edge210]
  SpineTangent = false
  Suppressed = false
  Transformation = 0
  Transition = 0
FEATURE [PartDesign::SubtractiveLoft] SubtractiveLoft
  BaseFeature = -> SubtractivePipe001
  Closed = false
  Profile = -> Sketch099
  Refine = true
  Ruled = false
  Sections = -> [Sketch108]
  Suppressed = false
FEATURE [PartDesign::SubtractiveLoft] SubtractiveLoft001
  BaseFeature = -> SubtractiveLoft
  Closed = false
  Profile = -> Clone2D
  Refine = true
  Ruled = false
  Sections = -> [Sketch109]
  Suppressed = false
FEATURE [Sketcher::SketchObject] Sketch112
  ArcFitTolerance = 1e-06
  AttachmentSupport = -> [Pad008]
  ExternalGeometry = -> [Binder]
  FullyConstrained = true
  MakeInternals = false
  MapMode = 5
  Placement = pos=(0,3.6,0) rot=(0,0.707107,0.707107;3.14159rad)
  sketch-geometry (4):
    g0: LineSegment [constr] StartX=167.782 StartY=-53.0314 StartZ=0 EndX=215.42 EndY=-53.0314 EndZ=0
    g1: GeomPoint [constr] X=191.282 Y=-53.0314 Z=0
    g2: Circle CenterX=191.282 CenterY=-53.0314 CenterZ=0 NormalX=0 NormalY=0 NormalZ=1 AngleXU=0 Radius=11.5
    g3: Circle CenterX=191.282 CenterY=-53.0314 CenterZ=0 NormalX=0 NormalY=0 NormalZ=1 AngleXU=0 Radius=10.7
  constraints (9):
    c: Horizontal(g0)
    c: PointOnObject(g0,g-3)
    c: Diameter(g2) = 23
    c: Coincident(g2,g1)
    c: Diameter(g3) = 21.4
    c: Coincident(g3,g1)
    c: DistanceX(g0,g1) = 23.5
    c: PointOnObject(g1,g0)
    c: Coincident(g0,g-4)
FEATURE [PartDesign::Chamfer] Chamfer016
  Angle = 45
  Base = -> SubtractiveLoft001 [Edge118,Edge117,Edge119,Edge120,Edge109]
  BaseFeature = -> SubtractiveLoft001
  ChamferType = 0
  FlipDirection = false
  Refine = true
  Size = 1.5
  Size2 = 1
  SupportTransform = false
  Suppressed = false
  UseAllEdges = false
FEATURE [PartDesign::Chamfer] Chamfer017
  Angle = 45
  Base = -> Chamfer016 [Edge15]
  BaseFeature = -> Chamfer016
  ChamferType = 0
  FlipDirection = false
  Refine = true
  Size = 1.6
  Size2 = 1
  SupportTransform = false
  Suppressed = false
  UseAllEdges = false
FEATURE [PartDesign::Chamfer] Chamfer018
  Angle = 45
  Base = -> Chamfer017 [Edge10]
  BaseFeature = -> Chamfer017
  ChamferType = 0
  FlipDirection = false
  Refine = true
  Size = 3.5
  Size2 = 1
  SupportTransform = false
  Suppressed = false
  UseAllEdges = false
FEATURE [PartDesign::Chamfer] Chamfer019
  Angle = 45
  Base = -> Chamfer018 [Edge94]
  BaseFeature = -> Chamfer018
  ChamferType = 0
  FlipDirection = false
  Refine = true
  Size = 1.9
  Size2 = 1
  SupportTransform = false
  Suppressed = false
  UseAllEdges = false
FEATURE [PartDesign::Fillet] Fillet009
  Base = -> Chamfer019 [Edge83]
  BaseFeature = -> Chamfer019
  Radius = 1.1
  Refine = true
  SupportTransform = false
  Suppressed = false
  UseAllEdges = false
FEATURE [PartDesign::Fillet] Fillet010
  Base = -> Fillet009 [Edge76]
  BaseFeature = -> Fillet009
  Radius = 1.9
  Refine = true
  SupportTransform = false
  Suppressed = false
  UseAllEdges = false
FEATURE [PartDesign::Pocket] Pocket005
  BaseFeature = -> Fillet010
  Direction = (0,-1,2e-16)
  Length = 0.8
  Length2 = 5
  Profile = -> Sketch112
  ReferenceAxis = -> Sketch112 [N_Axis]
  Refine = true
  Suppressed = false
  Type = 0
FEATURE [Part::Part2DObjectPython] ShapeString001  # Draft 2D object (typed FeaturePython)
  FontFile = <path>
  Fuse = false
  Justification = 6
  JustificationReference = 0
  KeepLeftMargin = false
  MakeFace = true
  ObliqueAngle = 0
  Placement = pos=(-183.5,3.6,-57.5) rot=(0,0.707107,0.707107;3.14159rad)
  ScaleToSize = true
  Size = 10
  String = AS
  Tracking = 0
FEATURE [PartDesign::Pocket] Pocket013
  BaseFeature = -> Pocket005
  Direction = (-1e-16,-1,2e-16)
  Length = 1
  Length2 = 5
  Profile = -> ShapeString001
  ReferenceAxis = -> ShapeString001 [N_Axis]
  Refine = true
  Suppressed = false
  Type = 0
FEATURE [PartDesign::Pad] Pad020
  Direction = (0,-1,2e-16)
  Length = 25.2
  Length2 = 10
  Midplane = true
  Placement = pos=(0,0,0) rot=(1,0,0;1.5708rad)
  Profile = -> Sketch021
  ReferenceAxis = -> Sketch021 [N_Axis]
  Refine = true
  Suppressed = false
  Type = 0
FEATURE [PartDesign::Body] Body001  label="perno fermo rumble e driver solenoide"
  AllowCompound = false
  Group = -> [Sketch021,Pad020]
  Origin = -> Origin001
  Tip = -> Pad020
FEATURE [PartDesign::Pad] Pad021
  Direction = (0,-1,2e-16)
  Length = 16.8
  Length2 = 10
  Midplane = true
  Placement = pos=(0,0,0) rot=(1,0,0;1.5708rad)
  Profile = -> Sketch061
  ReferenceAxis = -> Sketch061 [N_Axis]
  Refine = true
  Suppressed = false
  Type = 0
FEATURE [PartDesign::Pocket] Pocket014
  BaseFeature = -> Pad021
  Direction = (0,1,-2e-16)
  Length = 12.8
  Length2 = 5
  Midplane = true
  Placement = pos=(0,0,0) rot=(1,0,0;1.5708rad)
  Profile = -> Sketch062
  ReferenceAxis = -> Sketch062 [N_Axis]
  Refine = true
  Suppressed = false
  Type = 0
FEATURE [PartDesign::Pad] Pad022
  BaseFeature = -> Pocket014
  Direction = (0,-1,2e-16)
  Length = 7.6
  Length2 = 10
  Midplane = true
  Placement = pos=(0,0,0) rot=(1,0,0;1.5708rad)
  Profile = -> Sketch063
  ReferenceAxis = -> Sketch063 [N_Axis]
  Refine = true
  Suppressed = false
  Type = 0
FEATURE [PartDesign::Body] Body003  label="blocco switch"
  AllowCompound = false
  Group = -> [Sketch061,Sketch062,Sketch063,Pad021,Pocket014,Pad022]
  Origin = -> Origin003
  Tip = -> Pad022
FEATURE [PartDesign::Pad] Pad024
  Direction = (0,-1,2e-16)
  Length = 17
  Length2 = 10
  Midplane = true
  Placement = pos=(0,0,0) rot=(1,0,0;1.5708rad)
  Profile = -> Sketch045
  ReferenceAxis = -> Sketch045 [N_Axis]
  Refine = true
  Suppressed = false
  Type = 0
FEATURE [PartDesign::Pocket] Pocket015
  BaseFeature = -> Pad024
  Direction = (-1,0,0)
  Length = 8
  Length2 = 5
  Placement = pos=(0,0,0) rot=(1,0,0;1.5708rad)
  Profile = -> Sketch047
  ReferenceAxis = -> Sketch047 [N_Axis]
  Refine = true
  Reversed = true
  Suppressed = false
  Type = 0
FEATURE [PartDesign::Pocket] Pocket016
  BaseFeature = -> Pocket015
  Direction = (-1,0,0)
  Length = 1
  Length2 = 5
  Placement = pos=(0,0,0) rot=(1,0,0;1.5708rad)
  Profile = -> Sketch046
  ReferenceAxis = -> Sketch046 [N_Axis]
  Refine = true
  Reversed = true
  Suppressed = false
  Type = 0
FEATURE [PartDesign::Pocket] Pocket017
  BaseFeature = -> Pocket016
  Direction = (0,1,-2e-16)
  Length = 17
  Length2 = 5
  Midplane = true
  Placement = pos=(0,0,0) rot=(1,0,0;1.5708rad)
  Profile = -> Sketch048
  ReferenceAxis = -> Sketch048 [N_Axis]
  Refine = true
  Suppressed = false
  Type = 0
FEATURE [PartDesign::Pad] Pad025
  BaseFeature = -> Pocket017
  Direction = (0,-1,2e-16)
  Length = 17
  Length2 = 10
  Midplane = true
  Placement = pos=(0,0,0) rot=(1,0,0;1.5708rad)
  Profile = -> Sketch049
  ReferenceAxis = -> Sketch049 [N_Axis]
  Refine = true
  Suppressed = false
  Type = 0
FEATURE [PartDesign::Pad] Pad026
  BaseFeature = -> Pad025
  Direction = (0,-1,2e-16)
  Length = 17
  Length2 = 10
  Midplane = true
  Placement = pos=(0,0,0) rot=(1,0,0;1.5708rad)
  Profile = -> Sketch066
  ReferenceAxis = -> Sketch066 [N_Axis]
  Refine = true
  Suppressed = false
  Type = 0
FEATURE [PartDesign::Pad] Pad027
  BaseFeature = -> Pad026
  Direction = (0,-1,2e-16)
  Length = 5
  Length2 = 10
  Midplane = true
  Placement = pos=(0,0,0) rot=(1,0,0;1.5708rad)
  Profile = -> Sketch064
  ReferenceAxis = -> Sketch064 [N_Axis]
  Refine = true
  Suppressed = false
  Type = 0
FEATURE [PartDesign::Pad] Pad028
  BaseFeature = -> Pad027
  Direction = (1,0,0)
  Length = 1
  Length2 = 10
  Placement = pos=(0,0,0) rot=(1,0,0;1.5708rad)
  Profile = -> Sketch068
  ReferenceAxis = -> Sketch068 [N_Axis]
  Refine = true
  Reversed = true
  Suppressed = false
  Type = 0
FEATURE [PartDesign::Chamfer] Chamfer020
  Angle = 45
  Base = -> Pad028 [Edge73,Edge75,Edge78,Edge77]
  BaseFeature = -> Pad028
  ChamferType = 0
  FlipDirection = false
  Placement = pos=(0,0,0) rot=(1,0,0;1.5708rad)
  Refine = true
  Size = 0.5
  Size2 = 1
  SupportTransform = false
  Suppressed = false
  UseAllEdges = false
FEATURE [PartDesign::Body] Body002  label="supporto per neopixel"
  AllowCompound = false
  Group = -> [Sketch045,Sketch047,Sketch046,Sketch048,Sketch049,Sketch066,Sketch064,Sketch068,Pad024,Pocket015,Pocket016,Pocket017,Pad025,Pad026,Pad027,Pad028,Chamfer020]
  Origin = -> Origin002
  Tip = -> Chamfer020
FEATURE [Sketcher::SketchObject] Sketch134  label="perno fermo rumble002"
  ArcFitTolerance = 1e-06
  AttachmentSupport = -> [XZ_Plane008]
  FullyConstrained = true
  MakeInternals = false
  MapMode = 5
  Placement = pos=(0,0,0) rot=(1,0,0;1.5708rad)
  sketch-geometry (16):
    g0: LineSegment StartX=0 StartY=0.45 StartZ=0 EndX=0 EndY=1.55 EndZ=0
    g1: LineSegment StartX=0.45 StartY=2 StartZ=0 EndX=1.55 EndY=2 EndZ=0
    g2: LineSegment StartX=2 StartY=1.55 StartZ=0 EndX=2 EndY=0.45 EndZ=0
    g3: LineSegment StartX=1.55 StartY=0 StartZ=0 EndX=0.45 EndY=0 EndZ=0
    g4: ArcOfCircle [constr] CenterX=0.45 CenterY=1.55 CenterZ=0 NormalX=0 NormalY=0 NormalZ=1 AngleXU=0 Radius=0.45 StartAngle=1.5708 EndAngle=3.14159
    g5: GeomPoint [constr] X=0 Y=2 Z=0
    g6: LineSegment StartX=0.45 StartY=2 StartZ=0 EndX=0 EndY=1.55 EndZ=0
    g7: ArcOfCircle [constr] CenterX=1.55 CenterY=1.55 CenterZ=0 NormalX=0 NormalY=0 NormalZ=1 AngleXU=0 Radius=0.45 StartAngle=0 EndAngle=1.5708
    g8: GeomPoint [constr] X=2 Y=2 Z=0
    g9: LineSegment StartX=2 StartY=1.55 StartZ=0 EndX=1.55 EndY=2 EndZ=0
    g10: ArcOfCircle [constr] CenterX=1.55 CenterY=0.45 CenterZ=0 NormalX=0 NormalY=0 NormalZ=1 AngleXU=0 Radius=0.45 StartAngle=4.71239 EndAngle=6.28319
    g11: GeomPoint [constr] X=2 Y=0 Z=0
    g12: LineSegment StartX=1.55 StartY=0 StartZ=0 EndX=2 EndY=0.45 EndZ=0
    g13: ArcOfCircle [constr] CenterX=0.45 CenterY=0.45 CenterZ=0 NormalX=0 NormalY=0 NormalZ=1 AngleXU=0 Radius=0.45 StartAngle=3.14159 EndAngle=4.71239
    g14: GeomPoint [constr] X=0 Y=0 Z=0
    g15: LineSegment StartX=0 StartY=0.45 StartZ=0 EndX=0.45 EndY=0 EndZ=0
  constraints (35):
    c: Coincident(g14,g-1)
    c: PointOnObject(g5,g-2)
    c: Horizontal(g1)
    c: Vertical(g2)
    c: Horizontal(g3)
    c: DistanceX(g5,g8) = 2
    c: DistanceY(g11,g8) = 2
    c: PointOnObject(g5,g0)
    c: PointOnObject(g5,g1)
    c: Tangent(g0,g4) = 1.5708
    c: Tangent(g1,g4) = 1.5708
    c: Coincident(g6,g0)
    c: Coincident(g6,g1)
    c: PointOnObject(g8,g2)
    c: PointOnObject(g8,g1)
    c: Tangent(g2,g7) = 1.5708
    c: Tangent(g1,g7) = 1.5708
    c: Coincident(g9,g2)
    c: Coincident(g9,g1)
    c: PointOnObject(g11,g2)
    c: PointOnObject(g11,g3)
    c: Tangent(g2,g10) = 1.5708
    c: Tangent(g3,g10) = 1.5708
    c: Coincident(g12,g2)
    c: Coincident(g12,g3)
    c: PointOnObject(g14,g0)
    c: PointOnObject(g14,g3)
    c: Tangent(g0,g13) = 1.5708
    c: Tangent(g3,g13) = 1.5708
    c: Coincident(g15,g0)
    c: Coincident(g15,g3)
    c: Equal(g6,g9)
    c: Equal(g9,g12)
    c: Equal(g12,g15)
    c: DistanceX(g14,g3) = 0.45
FEATURE [PartDesign::Pad] Pad029
  Direction = (0,-1,2e-16)
  Length = 17
  Length2 = 10
  Midplane = true
  Placement = pos=(0,0,0) rot=(1,0,0;1.5708rad)
  Profile = -> Sketch134
  ReferenceAxis = -> Sketch134 [N_Axis]
  Refine = true
  Suppressed = false
  Type = 0
FEATURE [PartDesign::Body] Body008  label="perno fermo neopixel"
  AllowCompound = false
  Group = -> [Sketch134,Pad029]
  Origin = -> Origin008
  Tip = -> Pad029
FEATURE [Sketcher::SketchObject] Sketch135  label="perno fermo rumble003"
  ArcFitTolerance = 1e-06
  AttachmentSupport = -> [XZ_Plane009]
  FullyConstrained = true
  MakeInternals = false
  MapMode = 5
  Placement = pos=(0,0,0) rot=(1,0,0;1.5708rad)
  sketch-geometry (16):
    g0: LineSegment StartX=4.69e-14 StartY=0.8 StartZ=0 EndX=-3.04e-14 EndY=3.1 EndZ=0
    g1: LineSegment StartX=0.8 StartY=3.9 StartZ=0 EndX=3.1 EndY=3.9 EndZ=0
    g2: LineSegment StartX=3.9 StartY=3.1 StartZ=0 EndX=3.9 EndY=0.8 EndZ=0
    g3: LineSegment StartX=3.1 StartY=0 StartZ=0 EndX=0.8 EndY=0 EndZ=0
    g4: ArcOfCircle [constr] CenterX=0.8 CenterY=3.1 CenterZ=0 NormalX=0 NormalY=0 NormalZ=1 AngleXU=0 Radius=0.8 StartAngle=1.5708 EndAngle=3.14159
    g5: GeomPoint [constr] X=0 Y=3.9 Z=0
    g6: LineSegment StartX=0.8 StartY=3.9 StartZ=0 EndX=-3.04e-14 EndY=3.1 EndZ=0
    g7: ArcOfCircle [constr] CenterX=3.1 CenterY=3.1 CenterZ=0 NormalX=0 NormalY=0 NormalZ=1 AngleXU=0 Radius=0.8 StartAngle=-2.4e-14 EndAngle=1.5708
    g8: GeomPoint [constr] X=3.9 Y=3.9 Z=0
    g9: LineSegment StartX=3.9 StartY=3.1 StartZ=0 EndX=3.1 EndY=3.9 EndZ=0
    g10: ArcOfCircle [constr] CenterX=3.1 CenterY=0.8 CenterZ=0 NormalX=0 NormalY=0 NormalZ=1 AngleXU=0 Radius=0.8 StartAngle=4.71239 EndAngle=6.28319
    g11: GeomPoint [constr] X=3.9 Y=0 Z=0
    g12: LineSegment StartX=3.1 StartY=0 StartZ=0 EndX=3.9 EndY=0.8 EndZ=0
    g13: ArcOfCircle [constr] CenterX=0.8 CenterY=0.8 CenterZ=0 NormalX=0 NormalY=0 NormalZ=1 AngleXU=0 Radius=0.8 StartAngle=3.14159 EndAngle=4.71239
    g14: GeomPoint [constr] X=0 Y=0 Z=0
    g15: LineSegment StartX=4.69e-14 StartY=0.8 StartZ=0 EndX=0.8 EndY=0 EndZ=0
  constraints (35):
    c: Coincident(g14,g-1)
    c: PointOnObject(g5,g-2)
    c: Horizontal(g1)
    c: Vertical(g2)
    c: Horizontal(g3)
    c: DistanceX(g5,g8) = 3.9
    c: DistanceY(g11,g8) = 3.9
    c: PointOnObject(g5,g0)
    c: PointOnObject(g5,g1)
    c: Tangent(g0,g4) = 1.5708
    c: Tangent(g1,g4) = 1.5708
    c: Coincident(g6,g0)
    c: Coincident(g6,g1)
    c: PointOnObject(g8,g2)
    c: PointOnObject(g8,g1)
    c: Tangent(g2,g7) = 1.5708
    c: Tangent(g1,g7) = 1.5708
    c: Coincident(g9,g2)
    c: Coincident(g9,g1)
    c: PointOnObject(g11,g2)
    c: PointOnObject(g11,g3)
    c: Tangent(g2,g10) = 1.5708
    c: Tangent(g3,g10) = 1.5708
    c: Coincident(g12,g2)
    c: Coincident(g12,g3)
    c: PointOnObject(g14,g0)
    c: PointOnObject(g14,g3)
    c: Tangent(g0,g13) = 1.5708
    c: Tangent(g3,g13) = 1.5708
    c: Coincident(g15,g0)
    c: Coincident(g15,g3)
    c: Equal(g6,g9)
    c: Equal(g9,g12)
    c: Equal(g12,g15)
    c: DistanceX(g14,g3) = 0.8
FEATURE [PartDesign::Pad] Pad030
  Direction = (0,-1,2e-16)
  Length = 25.2
  Length2 = 10
  Midplane = true
  Placement = pos=(0,0,0) rot=(1,0,0;1.5708rad)
  Profile = -> Sketch135
  ReferenceAxis = -> Sketch135 [N_Axis]
  Refine = true
  Suppressed = false
  Type = 0
FEATURE [PartDesign::Body] Body009  label="perno fermo switch - caricabatterie - grilletto"
  AllowCompound = false
  Group = -> [Sketch135,Pad030]
  Origin = -> Origin009
  Tip = -> Pad030
FEATURE [Sketcher::SketchObject] Sketch136  label="scavo_rele"
  ArcFitTolerance = 1e-06
  AttachmentSupport = -> [XZ_Plane]
  ExternalGeometry = -> [Sketch]
  FullyConstrained = true
  MakeInternals = false
  MapMode = 5
  Placement = pos=(0,0,0) rot=(1,0,0;1.5708rad)
  sketch-geometry (7):
    g0: LineSegment [constr] StartX=-173.013 StartY=-62.644 StartZ=0 EndX=-176.535 EndY=-73.4861 EndZ=0
    g1: LineSegment [constr] StartX=-173.013 StartY=-62.644 StartZ=0 EndX=-170.35 EndY=-63.5093 EndZ=0
    g2: LineSegment [constr] StartX=-173.013 StartY=-62.644 StartZ=0 EndX=-176.627 EndY=-61.4698 EndZ=0
    g3: LineSegment StartX=-176.627 StartY=-61.4698 StartZ=0 EndX=-170.35 EndY=-63.5093 EndZ=0
    g4: LineSegment StartX=-176.627 StartY=-61.4698 StartZ=0 EndX=-180.149 EndY=-72.3118 EndZ=0
    g5: LineSegment StartX=-170.35 StartY=-63.5093 StartZ=0 EndX=-173.872 EndY=-74.3513 EndZ=0
    g6: LineSegment StartX=-180.149 StartY=-72.3118 StartZ=0 EndX=-173.872 EndY=-74.3513 EndZ=0
  constraints (19):
    c: Tangent(g0,g-3)
    c: Distance(g0,g-3) = 89
    c: Distance(g0,g0) = 11.4
    c: Coincident(g1,g0)
    c: Coincident(g2,g0)
    c: Distance(g2) = 3.8
    c: Distance(g1) = 2.8
    c: Perpendicular(g0,g1)
    c: Perpendicular(g0,g2)
    c: Coincident(g3,g2)
    c: Coincident(g3,g1)
    c: Equal(g4,g0)
    c: Equal(g5,g0)
    c: Parallel(g4,g0)
    c: Parallel(g5,g0)
    c: Coincident(g4,g2)
    c: Coincident(g5,g1)
    c: Coincident(g6,g4)
    c: Coincident(g6,g5)
FEATURE [Part::Extrusion] Extrude076  label="Extrude076 - scavo_rele"
  Base = -> Sketch136
  Dir = (0,-1,2e-16)
  DirMode = 2
  FaceMakerClass = Part::FaceMakerBullseye
  FaceMakerMode = 3
  LengthFwd = 17.8
  LengthRev = 0
  Solid = true
  Symmetric = true
FEATURE [Sketcher::SketchObject] Sketch137  label="scavo_nuovo_driver"
  ArcFitTolerance = 1e-06
  AttachmentSupport = -> [XZ_Plane]
  ExternalGeometry = -> [Sketch]
  FullyConstrained = true
  MakeInternals = false
  MapMode = 5
  Placement = pos=(0,0,0) rot=(1,0,0;1.5708rad)
  sketch-geometry (7):
    g0: LineSegment [constr] StartX=-167.759 StartY=-46.4761 StartZ=0 EndX=-172.58 EndY=-61.3126 EndZ=0
    g1: LineSegment [constr] StartX=-167.759 StartY=-46.4761 StartZ=0 EndX=-165.477 EndY=-47.2177 EndZ=0
    g2: LineSegment [constr] StartX=-167.759 StartY=-46.4761 StartZ=0 EndX=-171.373 EndY=-45.3018 EndZ=0
    g3: LineSegment StartX=-171.373 StartY=-45.3018 StartZ=0 EndX=-165.477 EndY=-47.2177 EndZ=0
    g4: LineSegment StartX=-171.373 StartY=-45.3018 StartZ=0 EndX=-176.194 EndY=-60.1383 EndZ=0
    g5: LineSegment StartX=-165.477 StartY=-47.2177 StartZ=0 EndX=-170.297 EndY=-62.0542 EndZ=0
    g6: LineSegment StartX=-176.194 StartY=-60.1383 StartZ=0 EndX=-170.297 EndY=-62.0542 EndZ=0
  constraints (19):
    c: Distance(g0,g-3) = 72
    c: Distance(g0) = 15.6
    c: Tangent(g0,g-3)
    c: Coincident(g1,g0)
    c: Coincident(g2,g0)
    c: Distance(g1) = 2.4
    c: Distance(g2) = 3.8
    c: Perpendicular(g0,g1)
    c: Perpendicular(g0,g2)
    c: Coincident(g3,g2)
    c: Coincident(g3,g1)
    c: Equal(g4,g0)
    c: Equal(g5,g0)
    c: Parallel(g4,g0)
    c: Parallel(g5,g0)
    c: Coincident(g4,g2)
    c: Coincident(g5,g1)
    c: Coincident(g6,g4)
    c: Coincident(g6,g5)
FEATURE [Part::Extrusion] Extrude077  label="Extrude077 - scavo_nuovo_driver"
  Base = -> Sketch137
  Dir = (0,-1,2e-16)
  DirMode = 2
  FaceMakerClass = Part::FaceMakerBullseye
  FaceMakerMode = 3
  LengthFwd = 20.8
  LengthRev = 0
  Solid = true
  Symmetric = true
FEATURE [Sketcher::SketchObject] Sketch138  label="scavo_nuovo_driver_alto"
  ArcFitTolerance = 1e-06
  AttachmentSupport = -> [XZ_Plane]
  ExternalGeometry = -> [Sketch]
  FullyConstrained = true
  MakeInternals = false
  MapMode = 5
  Placement = pos=(0,0,0) rot=(1,0,0;1.5708rad)
  sketch-geometry (7):
    g0: LineSegment [constr] StartX=-188.796 StartY=17.7274 StartZ=0 EndX=-187.75 EndY=4.97025 EndZ=0
    g1: LineSegment StartX=-187.75 StartY=4.97025 StartZ=0 EndX=-189.743 EndY=4.8067 EndZ=0
    g2: LineSegment StartX=-187.75 StartY=4.97025 StartZ=0 EndX=-182.766 EndY=5.37913 EndZ=0
    g3: LineSegment StartX=-190.79 StartY=17.5638 StartZ=0 EndX=-189.743 EndY=4.8067 EndZ=0
    g4: LineSegment StartX=-183.813 StartY=18.1363 StartZ=0 EndX=-182.766 EndY=5.37913 EndZ=0
    g5: LineSegment StartX=-190.79 StartY=17.5638 StartZ=0 EndX=-188.796 EndY=17.7274 EndZ=0
    g6: LineSegment StartX=-188.796 StartY=17.7274 StartZ=0 EndX=-183.813 EndY=18.1363 EndZ=0
  constraints (20):
    c: Distance(g0) = 12.8
    c: DistanceY(g-3,g0) = 9
    c: PointOnObject(g0,g-4)
    c: PointOnObject(g0,g-4)
    c: Coincident(g1,g0)
    c: Coincident(g2,g0)
    c: Distance(g1) = 2
    c: Distance(g2) = 5
    c: Perpendicular(g0,g1)
    c: Perpendicular(g0,g2)
    c: Equal(g3,g0)
    c: Parallel(g3,g0)
    c: Coincident(g3,g1)
    c: Equal(g4,g0)
    c: Parallel(g4,g0)
    c: Coincident(g4,g2)
    c: Coincident(g5,g3)
    c: Coincident(g5,g0)
    c: Coincident(g6,g0)
    c: Coincident(g6,g4)
FEATURE [Part::Extrusion] Extrude078  label="Extrude078 - scavo_nuovo_driver_alto"
  Base = -> Sketch138
  Dir = (0,-1,2e-16)
  DirMode = 2
  FaceMakerClass = Part::FaceMakerBullseye
  FaceMakerMode = 3
  LengthFwd = 16.6
  LengthRev = 0
  Solid = true
  Symmetric = true
FEATURE [Sketcher::SketchObject] Sketch139  label="fermi_nuovo_driver_alto"
  ArcFitTolerance = 1e-06
  AttachmentSupport = -> [XZ_Plane]
  ExternalGeometry = -> [Sketch138,Sketch]
  FullyConstrained = true
  MakeInternals = false
  MapMode = 5
  Placement = pos=(0,0,0) rot=(1,0,0;1.5708rad)
  sketch-geometry (17):
    g0: LineSegment [constr] StartX=-188.314 StartY=16.4295 StartZ=0 EndX=-187.885 EndY=13.7638 EndZ=0
    g1: LineSegment [constr] StartX=-187.885 StartY=13.7638 StartZ=0 EndX=-187.456 EndY=11.0981 EndZ=0
    g2: LineSegment StartX=-187.885 StartY=13.7638 StartZ=0 EndX=-187.71 EndY=12.6778 EndZ=0
    g3: LineSegment StartX=-187.885 StartY=13.7638 StartZ=0 EndX=-188.06 EndY=14.8499 EndZ=0
    g4: LineSegment StartX=-187.71 StartY=12.6778 StartZ=0 EndX=-185.538 EndY=13.0274 EndZ=0
    g5: LineSegment StartX=-188.06 StartY=14.8499 StartZ=0 EndX=-185.888 EndY=15.1994 EndZ=0
    g6: LineSegment StartX=-185.888 StartY=15.1994 StartZ=0 EndX=-185.538 EndY=13.0274 EndZ=0
    g7: LineSegment StartX=-187.456 StartY=11.0981 StartZ=0 EndX=-189.035 EndY=10.8439 EndZ=0
    g8: LineSegment StartX=-188.314 StartY=16.4295 StartZ=0 EndX=-189.893 EndY=16.1753 EndZ=0
    g9: LineSegment StartX=-189.893 StartY=16.1753 StartZ=0 EndX=-189.035 EndY=10.8439 EndZ=0
    g10: LineSegment StartX=-187.456 StartY=11.0981 StartZ=0 EndX=-185.284 EndY=11.4477 EndZ=0
    g11: LineSegment StartX=-188.314 StartY=16.4295 StartZ=0 EndX=-186.142 EndY=16.7791 EndZ=0
    g12: LineSegment StartX=-184.308 StartY=15.4537 StartZ=0 EndX=-183.958 EndY=13.2816 EndZ=0
    g13: ArcOfCircle CenterX=-185.888 CenterY=15.1994 CenterZ=0 NormalX=0 NormalY=0 NormalZ=1 AngleXU=0 Radius=1.6 StartAngle=0.15957 EndAngle=1.73037
    g14: GeomPoint [constr] X=-184.562 Y=17.0333 Z=0
    g15: ArcOfCircle CenterX=-185.538 CenterY=13.0274 CenterZ=0 NormalX=0 NormalY=0 NormalZ=1 AngleXU=0 Radius=1.6 StartAngle=4.87196 EndAngle=6.44276
    g16: GeomPoint [constr] X=-183.704 Y=11.7019 Z=0
  constraints (43):
    c: Tangent(g1,g0) = -1.5708
    c: Distance(g0) = 2.7
    c: Equal(g1,g0)
    c: Tangent(g1,g-5)
    c: Coincident(g2,g0)
    c: Coincident(g3,g0)
    c: Distance(g2) = 1.1
    c: Equal(g3,g2)
    c: PointOnObject(g3,g2)
    c: Coincident(g4,g2)
    c: Coincident(g5,g3)
    c: Distance(g4) = 2.2
    c: Equal(g4,g5)
    c: Perpendicular(g1,g4)
    c: Perpendicular(g0,g5)
    c: Coincident(g6,g5)
    c: Coincident(g6,g4)
    c: Coincident(g7,g1)
    c: Coincident(g8,g0)
    c: Distance(g7) = 1.6
    c: Equal(g7,g8)
    c: Perpendicular(g1,g7)
    c: Perpendicular(g8,g0)
    c: Coincident(g9,g8)
    c: Coincident(g9,g7)
    c: Coincident(g10,g1)
    c: Coincident(g11,g0)
    c: Distance(g10,g16) = 3.8
    c: Perpendicular(g1,g10)
    c: Perpendicular(g1,g11)
    c: DistanceY(g0,g-4) = 3.8
    c: PointOnObject(g14,g12)
    c: PointOnObject(g14,g11)
    c: Tangent(g12,g13) = 1.5708
    c: Tangent(g11,g13) = 1.5708
    c: PointOnObject(g16,g12)
    c: PointOnObject(g16,g10)
    c: Tangent(g12,g15) = 1.5708
    c: Tangent(g10,g15) = -1.5708
    c: Equal(g13,g15)
    c: Coincident(g13,g5)
    c: Parallel(g2,g0)
    c: PointOnObject(g0,g-5)
FEATURE [Part::Extrusion] Extrude079  label="Extrude079 - fermi_nuovo_driver_alto"
  Base = -> Sketch139
  Dir = (0,-1,2e-16)
  DirMode = 2
  FaceMakerClass = Part::FaceMakerBullseye
  FaceMakerMode = 3
  LengthFwd = 25.2
  LengthRev = 0
  Solid = true
  Symmetric = true
FEATURE [Sketcher::SketchObject] Sketch140  label="scavo_diodo_nuovo_driver_alto"
  ArcFitTolerance = 1e-06
  AttachmentSupport = -> [XZ_Plane]
  ExternalGeometry = -> [Sketch138]
  FullyConstrained = true
  MakeInternals = false
  MapMode = 5
  Placement = pos=(0,0,0) rot=(1,0,0;1.5708rad)
  sketch-geometry (4):
    g0: LineSegment StartX=-190.79 StartY=17.5638 StartZ=0 EndX=-189.743 EndY=4.8067 EndZ=0
    g1: LineSegment StartX=-193.78 StartY=17.3185 StartZ=0 EndX=-192.733 EndY=4.56137 EndZ=0
    g2: LineSegment StartX=-190.79 StartY=17.5638 StartZ=0 EndX=-193.78 EndY=17.3185 EndZ=0
    g3: LineSegment StartX=-192.733 StartY=4.56137 StartZ=0 EndX=-189.743 EndY=4.8067 EndZ=0
  constraints (11):
    c: Equal(g0,g-3)
    c: Parallel(g0,g-3)
    c: Equal(g1,g-3)
    c: Parallel(g1,g-3)
    c: Coincident(g2,g0)
    c: Distance(g2) = 3
    c: Perpendicular(g0,g2)
    c: Coincident(g1,g2)
    c: Coincident(g3,g1)
    c: Coincident(g3,g0)
    c: Coincident(g0,g-3)
FEATURE [Part::Extrusion] Extrude080  label="Extrude080 - scavo_diodo_nuovo_driver_alto"
  Base = -> Sketch140
  Dir = (0,-1,2e-16)
  DirMode = 2
  FaceMakerClass = Part::FaceMakerBullseye
  FaceMakerMode = 3
  LengthFwd = 4
  LengthRev = 0
  Placement = pos=(0,7.8,0) rot=(0,0,1;0rad)
  Solid = true
  Symmetric = false
FEATURE [Part::MultiFuse] Fusion001
  Refine = true
  Shapes = -> [Cut043,Extrude079]
FEATURE [Part::Cut] Cut044
  Base = -> Fusion001
  Refine = true
  Tool = -> Extrude078
FEATURE [Part::Cut] Cut045
  Base = -> Cut044
  Refine = true
  Tool = -> Extrude080
FEATURE [Sketcher::SketchObject] Sketch141  label="fermi_nuovo_driver"
  ArcFitTolerance = 1e-06
  AttachmentSupport = -> [XZ_Plane]
  ExternalGeometry = -> [Sketch,Sketch137]
  FullyConstrained = true
  MakeInternals = false
  MapMode = 5
  Placement = pos=(0,0,0) rot=(1,0,0;1.5708rad)
  sketch-geometry (16):
    g0: LineSegment [constr] StartX=-165.477 StartY=-47.2177 StartZ=0 EndX=-167.759 EndY=-46.4761 EndZ=0
    g1: LineSegment [constr] StartX=-167.759 StartY=-46.4761 StartZ=0 EndX=-168.006 EndY=-47.2369 EndZ=0
    g2: LineSegment [constr] StartX=-168.006 StartY=-47.2369 StartZ=0 EndX=-169.675 EndY=-52.3726 EndZ=0
    g3: LineSegment StartX=-169.675 StartY=-52.3726 StartZ=0 EndX=-171.767 EndY=-51.6928 EndZ=0
    g4: LineSegment StartX=-172.795 StartY=-49.6767 StartZ=0 EndX=-172.115 EndY=-47.5843 EndZ=0
    g5: LineSegment StartX=-170.099 StartY=-46.5571 StartZ=0 EndX=-166.485 EndY=-47.7313 EndZ=0
    g6: LineSegment StartX=-166.485 StartY=-47.7313 StartZ=0 EndX=-168.153 EndY=-52.867 EndZ=0
    g7: LineSegment StartX=-169.675 StartY=-52.3726 StartZ=0 EndX=-168.153 EndY=-52.867 EndZ=0
    g8: LineSegment StartX=-170.593 StartY=-48.0788 StartZ=0 EndX=-171.273 EndY=-50.1711 EndZ=0
    g9: LineSegment StartX=-171.273 StartY=-50.1711 StartZ=0 EndX=-169.181 EndY=-50.8509 EndZ=0
    g10: LineSegment StartX=-169.181 StartY=-50.8509 StartZ=0 EndX=-168.501 EndY=-48.7586 EndZ=0
    g11: LineSegment StartX=-168.501 StartY=-48.7586 StartZ=0 EndX=-170.593 EndY=-48.0788 EndZ=0
    g12: ArcOfCircle CenterX=-170.593 CenterY=-48.0788 CenterZ=0 NormalX=0 NormalY=0 NormalZ=1 AngleXU=0 Radius=1.6 StartAngle=1.25664 EndAngle=2.82743
    g13: GeomPoint [constr] X=-171.62 Y=-46.0626 Z=0
    g14: ArcOfCircle CenterX=-171.273 CenterY=-50.1711 CenterZ=0 NormalX=0 NormalY=0 NormalZ=1 AngleXU=0 Radius=1.6 StartAngle=2.82743 EndAngle=4.39823
    g15: GeomPoint [constr] X=-173.289 Y=-51.1984 Z=0
  constraints (41):
    c: Coincident(g0,g-4)
    c: PointOnObject(g0,g-3)
    c: Parallel(g0,g-4)
    c: Coincident(g1,g0)
    c: Parallel(g1,g-3)
    c: Distance(g1) = 0.8
    c: Coincident(g2,g1)
    c: Distance(g2) = 5.4
    c: Coincident(g3,g2)
    c: Parallel(g2,g-3)
    c: Distance(g15,g13) = 5.4
    c: Perpendicular(g3,g2)
    c: Parallel(g4,g2)
    c: Distance(g5,g13) = 5.4
    c: Distance(g3,g15) = 3.8
    c: Perpendicular(g4,g5)
    c: Coincident(g6,g5)
    c: Distance(g6) = 5.4
    c: Parallel(g6,g4)
    c: Coincident(g7,g2)
    c: Coincident(g7,g6)
    c: Coincident(g8,g9)
    c: Coincident(g9,g10)
    c: Coincident(g10,g11)
    c: Coincident(g11,g8)
    c: Distance(g8,g10) = 2.2
    c: Distance(g9,g11) = 2.2
    c: Perpendicular(g11,g8)
    c: Equal(g8,g10)
    c: Equal(g11,g9)
    c: Tangent(g10,g2)
    c: Distance(g10,g1) = 1.6
    c: PointOnObject(g13,g4)
    c: PointOnObject(g13,g5)
    c: Tangent(g4,g12) = 1.5708
    c: Tangent(g5,g12) = 1.5708
    c: PointOnObject(g15,g4)
    c: Tangent(g4,g14) = 1.5708
    c: Tangent(g3,g14) = 1.5708
    c: Equal(g14,g12)
    c: Coincident(g12,g8)
FEATURE [Part::Extrusion] Extrude081  label="Extrude081 - fermi_nuovo_driver"
  Base = -> Sketch141
  Dir = (0,-1,2e-16)
  DirMode = 2
  FaceMakerClass = Part::FaceMakerBullseye
  FaceMakerMode = 3
  LengthFwd = 25.2
  LengthRev = 0
  Solid = true
  Symmetric = true
FEATURE [Part::MultiFuse] Fusion002
  Refine = true
  Shapes = -> [Cut045,Extrude081]
FEATURE [Part::Cut] Cut046
  Base = -> Fusion002
  Refine = true
  Tool = -> Extrude077
FEATURE [Sketcher::SketchObject] Sketch142  label="fermi_rele"
  ArcFitTolerance = 1e-06
  AttachmentSupport = -> [XZ_Plane]
  ExternalGeometry = -> [Sketch,Sketch136]
  FullyConstrained = true
  MakeInternals = false
  MapMode = 5
  Placement = pos=(0,0,0) rot=(1,0,0;1.5708rad)
  sketch-geometry (15):
    g0: LineSegment StartX=-177.245 StartY=-63.3719 StartZ=0 EndX=-177.924 EndY=-65.4642 EndZ=0
    g1: LineSegment StartX=-175.228 StartY=-62.3446 StartZ=0 EndX=-171.614 EndY=-63.5189 EndZ=0
    g2: LineSegment StartX=-171.614 StartY=-63.5189 StartZ=0 EndX=-173.283 EndY=-68.6546 EndZ=0
    g3: LineSegment StartX=-176.897 StartY=-67.4803 StartZ=0 EndX=-173.283 EndY=-68.6546 EndZ=0
    g4: LineSegment StartX=-175.723 StartY=-63.8663 StartZ=0 EndX=-173.631 EndY=-64.5461 EndZ=0
    g5: LineSegment StartX=-175.723 StartY=-63.8663 StartZ=0 EndX=-176.403 EndY=-65.9586 EndZ=0
    g6: LineSegment StartX=-173.631 StartY=-64.5461 StartZ=0 EndX=-174.31 EndY=-66.6385 EndZ=0
    g7: LineSegment StartX=-176.403 StartY=-65.9586 StartZ=0 EndX=-174.31 EndY=-66.6385 EndZ=0
    g8: LineSegment [constr] StartX=-173.631 StartY=-64.5461 StartZ=0 EndX=-173.136 EndY=-63.0245 EndZ=0
    g9: LineSegment [constr] StartX=-173.631 StartY=-64.5461 StartZ=0 EndX=-172.109 EndY=-65.0406 EndZ=0
    g10: LineSegment [constr] StartX=-170.35 StartY=-63.5093 StartZ=0 EndX=-173.013 EndY=-62.644 EndZ=0
    g11: ArcOfCircle CenterX=-175.723 CenterY=-63.8663 CenterZ=0 NormalX=0 NormalY=0 NormalZ=1 AngleXU=0 Radius=1.6 StartAngle=1.25664 EndAngle=2.82743
    g12: GeomPoint [constr] X=-176.75 Y=-61.8502 Z=0
    g13: ArcOfCircle CenterX=-176.403 CenterY=-65.9586 CenterZ=0 NormalX=0 NormalY=0 NormalZ=1 AngleXU=0 Radius=1.6 StartAngle=2.82743 EndAngle=4.39823
    g14: GeomPoint [constr] X=-178.419 Y=-66.9859 Z=0
  constraints (39):
    c: Distance(g14,g12) = 5.4
    c: Distance(g1,g12) = 5.4
    c: Perpendicular(g1,g0)
    c: Coincident(g2,g1)
    c: Parallel(g2,g0)
    c: Coincident(g3,g2)
    c: Parallel(g2,g-3)
    c: Coincident(g5,g4)
    c: Distance(g5) = 2.2
    c: Distance(g4) = 2.2
    c: Perpendicular(g4,g5)
    c: Coincident(g6,g4)
    c: Equal(g6,g5)
    c: Parallel(g6,g5)
    c: Coincident(g7,g5)
    c: Coincident(g7,g6)
    c: Coincident(g8,g4)
    c: Coincident(g9,g4)
    c: Distance(g8) = 1.6
    c: Distance(g9) = 1.6
    c: Parallel(g8,g6)
    c: Parallel(g9,g4)
    c: PointOnObject(g8,g1)
    c: PointOnObject(g9,g2)
    c: Coincident(g10,g-4)
    c: Parallel(g10,g-4)
    c: PointOnObject(g10,g-3)
    c: Tangent(g6,g-3) = 1.5708
    c: Distance(g4,g10) = 2
    c: PointOnObject(g12,g1)
    c: Tangent(g1,g11) = 1.5708
    c: Tangent(g0,g11) = -1.5708
    c: PointOnObject(g14,g3)
    c: PointOnObject(g14,g0)
    c: Tangent(g3,g13) = -1.5708
    c: Tangent(g0,g13) = -1.5708
    c: Equal(g11,g13)
    c: Coincident(g11,g4)
    c: Parallel(g3,g1)
FEATURE [Part::Extrusion] Extrude082  label="Extrude082 - fermi_rele"
  Base = -> Sketch142
  Dir = (0,-1,2e-16)
  DirMode = 2
  FaceMakerClass = Part::FaceMakerBullseye
  FaceMakerMode = 3
  LengthFwd = 25.2
  LengthRev = 0
  Solid = true
  Symmetric = true
FEATURE [Part::MultiFuse] Fusion003
  Refine = true
  Shapes = -> [Cut046,Extrude082]
FEATURE [Part::Cut] Cut047
  Base = -> Fusion003
  Refine = true
  Tool = -> Extrude076
FEATURE [Sketcher::SketchObject] Sketch143  label="foro_passaggio_cavi_led_batteria"
  ArcFitTolerance = 1e-06
  AttachmentSupport = -> [XZ_Plane]
  ExternalGeometry = -> [Sketch,Sketch042,Sketch036]
  FullyConstrained = true
  MakeInternals = false
  MapMode = 5
  Placement = pos=(0,0,0) rot=(1,0,0;1.5708rad)
  sketch-geometry (4):
    g0: LineSegment StartX=-207.775 StartY=-41.3701 StartZ=0 EndX=-213.607 EndY=-53.8767 EndZ=0
    g1: LineSegment StartX=-213.607 StartY=-53.8767 StartZ=0 EndX=-211.843 EndY=-59.5559 EndZ=0
    g2: LineSegment StartX=-207.775 StartY=-41.3701 StartZ=0 EndX=-207.775 EndY=-50.8316 EndZ=0
    g3: LineSegment StartX=-207.775 StartY=-50.8316 StartZ=0 EndX=-211.843 EndY=-59.5559 EndZ=0
  constraints (9):
    c: Coincident(g0,g-3)
    c: PointOnObject(g1,g-6)
    c: Coincident(g1,g0)
    c: Coincident(g2,g0)
    c: Coincident(g2,g-7)
    c: Coincident(g3,g2)
    c: Parallel(g3,g0)
    c: Coincident(g3,g1)
    c: Coincident(g0,g-5)
FEATURE [Part::Extrusion] Extrude083  label="Extrude083 - foro_passaggio_cavi_led_batteria"
  Base = -> Sketch143
  Dir = (0,-1,2e-16)
  DirMode = 2
  FaceMakerClass = Part::FaceMakerBullseye
  FaceMakerMode = 3
  LengthFwd = 6
  LengthRev = 0
  Solid = true
  Symmetric = true
FEATURE [Part::Cut] Cut048
  Base = -> Cut047
  Refine = true
  Tool = -> Extrude083
FEATURE [Sketcher::SketchObject] Sketch144  label="foro_areazione_alimentatore"
  ArcFitTolerance = 1e-06
  AttachmentSupport = -> [XZ_Plane]
  ExternalGeometry = -> [Sketch036]
  FullyConstrained = true
  MakeInternals = false
  MapMode = 5
  Placement = pos=(0,0,0) rot=(1,0,0;1.5708rad)
  sketch-geometry (4):
    g0: LineSegment StartX=-211.843 StartY=-60.3701 StartZ=0 EndX=-207.775 EndY=-60.3701 EndZ=0
    g1: LineSegment StartX=-207.775 StartY=-60.3701 StartZ=0 EndX=-207.775 EndY=-70.3701 EndZ=0
    g2: LineSegment StartX=-211.843 StartY=-60.3701 StartZ=0 EndX=-211.843 EndY=-70.3701 EndZ=0
    g3: LineSegment StartX=-207.775 StartY=-70.3701 StartZ=0 EndX=-211.843 EndY=-70.3701 EndZ=0
  constraints (11):
    c: Horizontal(g0)
    c: Distance(g1) = 10
    c: Coincident(g1,g0)
    c: Tangent(g1,g-3)
    c: PointOnObject(g0,g-4)
    c: Coincident(g2,g0)
    c: PointOnObject(g2,g-4)
    c: Coincident(g3,g1)
    c: Horizontal(g3)
    c: Coincident(g3,g2)
    c: DistanceY(g0,g-3) = 19
FEATURE [Part::Extrusion] Extrude084  label="Extrude084 - foro_areazione_alimentatore"
  Base = -> Sketch144
  Dir = (0,-1,2e-16)
  DirMode = 2
  FaceMakerClass = Part::FaceMakerBullseye
  FaceMakerMode = 3
  LengthFwd = 10
  LengthRev = 0
  Solid = true
  Symmetric = true
FEATURE [Part::Cut] Cut049
  Base = -> Cut048
  Refine = true
  Tool = -> Extrude084
FEATURE [Sketcher::SketchObject] Sketch145  label="foro_per_condesatore"
  ArcFitTolerance = 1e-06
  AttachmentSupport = -> [XZ_Plane]
  ExternalGeometry = -> [Sketch,Sketch139]
  FullyConstrained = true
  MakeInternals = false
  MapMode = 5
  Placement = pos=(0,0,0) rot=(1,0,0;1.5708rad)
  sketch-geometry (1):
    g0: Circle CenterX=-182.345 CenterY=7.02342 CenterZ=0 NormalX=0 NormalY=0 NormalZ=1 AngleXU=0 Radius=5.2
  constraints (3):
    c: Diameter(g0) = 10.4
    c: Tangent(g0,g-3)
    c: Tangent(g0,g-4)
FEATURE [Part::Extrusion] Extrude085  label="Extrude085 - foro_per_condesatore"
  Base = -> Sketch145
  Dir = (0,-1,2e-16)
  DirMode = 2
  FaceMakerClass = Part::FaceMakerBullseye
  FaceMakerMode = 3
  LengthFwd = 25.2
  LengthRev = 0
  Solid = true
  Symmetric = true
FEATURE [Part::Cut] Cut050
  Base = -> Cut049
  Refine = true
  Tool = -> Extrude085
FEATURE [Sketcher::SketchObject] Sketch146  label="scavo_pulsante_6x6_per_led_batteria"
  ArcFitTolerance = 1e-06
  AttachmentSupport = -> [XZ_Plane]
  ExternalGeometry = -> [Sketch016]
  FullyConstrained = true
  MakeInternals = false
  MapMode = 5
  Placement = pos=(0,0,0) rot=(1,0,0;1.5708rad)
  sketch-geometry (4):
    g0: LineSegment StartX=-217.243 StartY=-66.0316 StartZ=0 EndX=-217.243 EndY=-72.8316 EndZ=0
    g1: LineSegment StartX=-217.243 StartY=-72.8316 StartZ=0 EndX=-211.043 EndY=-72.8316 EndZ=0
    g2: LineSegment StartX=-211.043 StartY=-72.8316 StartZ=0 EndX=-211.043 EndY=-66.0316 EndZ=0
    g3: LineSegment StartX=-211.043 StartY=-66.0316 StartZ=0 EndX=-217.243 EndY=-66.0316 EndZ=0
  constraints (12):
    c: Coincident(g0,g1)
    c: Coincident(g1,g2)
    c: Coincident(g2,g3)
    c: Coincident(g3,g0)
    c: Vertical(g0)
    c: Vertical(g2)
    c: Horizontal(g1)
    c: Horizontal(g3)
    c: Distance(g0,g2) = 6.2
    c: Distance(g1,g3) = 6.8
    c: Tangent(g1,g-3)
    c: DistanceX(g0,g-3) = 3.8
FEATURE [Part::Extrusion] Extrude086  label="Extrude086 - scavo_pulsante_6x6_per_led_batteria"
  Base = -> Sketch146
  Dir = (0,-1,2e-16)
  DirMode = 2
  FaceMakerClass = Part::FaceMakerBullseye
  FaceMakerMode = 3
  LengthFwd = 4.2
  LengthRev = 0
  Placement = pos=(0,12.6,0) rot=(0,0,1;0rad)
  Solid = true
  Symmetric = false
FEATURE [Sketcher::SketchObject] Sketch147  label="scavo_led_stato_batteria"
  ArcFitTolerance = 1e-06
  AttachmentSupport = -> [XZ_Plane]
  ExternalGeometry = -> [Sketch016]
  FullyConstrained = true
  MakeInternals = false
  MapMode = 5
  Placement = pos=(0,0,0) rot=(1,0,0;1.5708rad)
  sketch-geometry (4):
    g0: LineSegment StartX=-215.943 StartY=-56.1316 StartZ=0 EndX=-215.943 EndY=-65.3316 EndZ=0
    g1: LineSegment StartX=-215.943 StartY=-65.3316 StartZ=0 EndX=-211.343 EndY=-65.3316 EndZ=0
    g2: LineSegment StartX=-211.343 StartY=-65.3316 StartZ=0 EndX=-211.343 EndY=-56.1316 EndZ=0
    g3: LineSegment StartX=-211.343 StartY=-56.1316 StartZ=0 EndX=-215.943 EndY=-56.1316 EndZ=0
  constraints (12):
    c: Coincident(g0,g1)
    c: Coincident(g1,g2)
    c: Coincident(g2,g3)
    c: Coincident(g3,g0)
    c: Distance(g0,g2) = 4.6
    c: Distance(g1,g3) = 9.2
    c: Equal(g0,g2)
    c: Equal(g1,g3)
    c: Perpendicular(g3,g0)
    c: DistanceY(g-3,g0) = 11.5
    c: DistanceX(g0,g-3) = 2.5
    c: Vertical(g2)
FEATURE [PartDesign::Body] Body  label="Struttura pistola"
  AllowCompound = false
  Group = -> [Sketch,Sketch002,Sketch004,DatumPlane,Sketch005,DatumPlane001,CopyCut,Sketch008,Sketch009,Sketch010,Sketch011,Sketch012,Sketch013,Sketch014,Sketch015,Sketch016,Sketch017,Sketch018,Sketch019,Sketch020,Sketch022,Sketch023,Sketch024,Sketch025,Sketch026,Sketch027,Sketch029,Sketch030,Sketch031,Sketch032,Sketch033,Sketch034,Sketch035,Sketch036,Sketch037,Sketch038,Sketch039,Sketch040,Sketch041,Sketch042,+27 more]
  Origin = -> Origin
FEATURE [Part::Extrusion] Extrude087  label="Extrude087 - scavo_led_stato_batteria"
  Base = -> Sketch147
  Dir = (0,-1,2e-16)
  DirMode = 2
  FaceMakerClass = Part::FaceMakerBullseye
  FaceMakerMode = 3
  LengthFwd = 2
  LengthRev = 0
  Placement = pos=(0,12.6,0) rot=(0,0,1;0rad)
  Solid = true
  Symmetric = false
FEATURE [Part::Cut] Cut051
  Base = -> Cut050
  Refine = true
  Tool = -> Extrude086
FEATURE [Part::Cut] Cut052
  Base = -> Cut051
  Refine = true
  Tool = -> Extrude087
FEATURE [Sketcher::SketchObject] Sketch148
  ArcFitTolerance = 1e-06
  AttachmentSupport = -> [Pad016]
  ExternalGeometry = -> [Pad016]
  FullyConstrained = true
  MakeInternals = false
  MapMode = 5
  Placement = pos=(0,0,-80.4316) rot=(1,0,0;3.14159rad)
  sketch-geometry (8):
    g0: LineSegment StartX=-176.685 StartY=3.6 StartZ=0 EndX=-186.685 EndY=3.6 EndZ=0
    g1: LineSegment StartX=-176.685 StartY=3.6 StartZ=0 EndX=-176.685 EndY=-9e-16 EndZ=0
    g2: LineSegment [constr] StartX=-186.685 StartY=3.6 StartZ=0 EndX=-186.685 EndY=-9e-16 EndZ=0
    g3: ArcOfEllipse CenterX=-186.685 CenterY=-1e-15 CenterZ=0 NormalX=0 NormalY=0 NormalZ=1 MajorRadius=10 MinorRadius=3.6 AngleXU=0 StartAngle=0 EndAngle=1.5708
    g4: LineSegment [constr] StartX=-176.685 StartY=-1e-15 StartZ=0 EndX=-196.685 EndY=-1e-15 EndZ=0
    g5: LineSegment [constr] StartX=-186.685 StartY=3.6 StartZ=0 EndX=-186.685 EndY=-3.6 EndZ=0
    g6: GeomPoint [constr] X=-177.356 Y=-1e-15 Z=0
    g7: GeomPoint [constr] X=-196.015 Y=-1e-15 Z=0
  constraints (13):
    c: Distance(g0) = 10
    c: Coincident(g0,g-5)
    c: PointOnObject(g0,g-3)
    c: Coincident(g1,g0)
    c: Coincident(g1,g-5)
    c: Coincident(g2,g0)
    c: Vertical(g2)
    c: PointOnObject(g2,g-4)
    c: InternalAlignment(g4-g7 -> g3) x4
    c: Coincident(g3,g2)
    c: Coincident(g3,g0)
    c: Coincident(g3,g1)
    c: Horizontal(g4)
FEATURE [PartDesign::SubtractivePipe] SubtractivePipe004
  AuxilleryCurvelinear = true
  AuxillerySpineTangent = false
  BaseFeature = -> Pad016
  Binormal = (0,0,0)
  Mode = 0
  Profile = -> Sketch148
  Refine = true
  Spine = -> Pad016 [Edge254]
  SpineTangent = false
  Suppressed = false
  Transformation = 0
  Transition = 0
FEATURE [Sketcher::SketchObject] Sketch149
  ArcFitTolerance = 1e-06
  AttachmentSupport = -> [Pad016]
  ExternalGeometry = -> [Pad016]
  FullyConstrained = true
  MakeInternals = false
  MapMode = 5
  Placement = pos=(0,0,-80.4316) rot=(1,0,0;3.14159rad)
  sketch-geometry (8):
    g0: LineSegment StartX=-215.932 StartY=3.6 StartZ=0 EndX=-205.932 EndY=3.6 EndZ=0
    g1: LineSegment StartX=-215.932 StartY=3.6 StartZ=0 EndX=-215.932 EndY=-4e-16 EndZ=0
    g2: LineSegment [constr] StartX=-205.932 StartY=3.6 StartZ=0 EndX=-205.932 EndY=-9e-16 EndZ=0
    g3: ArcOfEllipse CenterX=-205.932 CenterY=-1e-15 CenterZ=0 NormalX=0 NormalY=0 NormalZ=1 MajorRadius=10 MinorRadius=3.6 AngleXU=-3.14159 StartAngle=4.71239 EndAngle=6.28319
    g4: LineSegment [constr] StartX=-215.932 StartY=-1e-15 StartZ=0 EndX=-195.932 EndY=-1e-15 EndZ=0
    g5: LineSegment [constr] StartX=-205.932 StartY=-3.6 StartZ=0 EndX=-205.932 EndY=3.6 EndZ=0
    g6: GeomPoint [constr] X=-215.262 Y=-1.1e-15 Z=0
    g7: GeomPoint [constr] X=-196.602 Y=-9e-16 Z=0
  constraints (13):
    c: Distance(g0) = 10
    c: Coincident(g0,g-5)
    c: PointOnObject(g0,g-5)
    c: Coincident(g1,g0)
    c: Coincident(g1,g-4)
    c: Coincident(g2,g0)
    c: Vertical(g2)
    c: PointOnObject(g2,g-3)
    c: InternalAlignment(g4-g7 -> g3) x4
    c: Coincident(g3,g2)
    c: Coincident(g3,g0)
    c: Coincident(g3,g1)
    c: Horizontal(g4)
FEATURE [PartDesign::SubtractivePipe] SubtractivePipe005
  AuxilleryCurvelinear = true
  AuxillerySpineTangent = false
  BaseFeature = -> SubtractivePipe004
  Binormal = (0,0,0)
  Mode = 0
  Profile = -> Sketch149
  Refine = true
  Spine = -> Pad016 [Edge256,Edge251,Edge252]
  SpineTangent = false
  Suppressed = false
  Transformation = 0
  Transition = 0
FEATURE [PartDesign::SubtractiveLoft] SubtractiveLoft002
  BaseFeature = -> SubtractivePipe005
  Closed = false
  Profile = -> Sketch129
  Refine = true
  Ruled = false
  Sections = -> [Sketch130]
  Suppressed = false
FEATURE [PartDesign::SubtractiveLoft] SubtractiveLoft003
  BaseFeature = -> SubtractiveLoft002
  Closed = false
  Profile = -> Clone2D001
  Refine = true
  Ruled = false
  Sections = -> [Sketch131]
  Suppressed = false
FEATURE [PartDesign::Chamfer] Chamfer010
  Angle = 45
  Base = -> SubtractiveLoft003 [Edge203,Edge204,Edge202,Edge201,Edge195]
  BaseFeature = -> SubtractiveLoft003
  ChamferType = 0
  FlipDirection = false
  Refine = true
  Size = 1.5
  Size2 = 1
  SupportTransform = false
  Suppressed = false
  UseAllEdges = false
FEATURE [PartDesign::Chamfer] Chamfer011
  Angle = 45
  Base = -> Chamfer010 [Edge15]
  BaseFeature = -> Chamfer010
  ChamferType = 0
  FlipDirection = false
  Refine = true
  Size = 1.6
  Size2 = 1
  SupportTransform = false
  Suppressed = false
  UseAllEdges = false
FEATURE [PartDesign::Chamfer] Chamfer012
  Angle = 45
  Base = -> Chamfer011 [Edge10]
  BaseFeature = -> Chamfer011
  ChamferType = 0
  FlipDirection = false
  Refine = true
  Size = 3.5
  Size2 = 1
  SupportTransform = false
  Suppressed = false
  UseAllEdges = false
FEATURE [PartDesign::Chamfer] Chamfer013
  Angle = 45
  Base = -> Chamfer012 [Edge94]
  BaseFeature = -> Chamfer012
  ChamferType = 0
  FlipDirection = false
  Refine = true
  Size = 1.9
  Size2 = 1
  SupportTransform = false
  Suppressed = false
  UseAllEdges = false
FEATURE [PartDesign::Fillet] Fillet007
  Base = -> Chamfer013 [Edge83]
  BaseFeature = -> Chamfer013
  Radius = 1.1
  Refine = true
  SupportTransform = false
  Suppressed = false
  UseAllEdges = false
FEATURE [PartDesign::Fillet] Fillet008
  Base = -> Fillet007 [Edge75]
  BaseFeature = -> Fillet007
  Radius = 1.9
  Refine = true
  SupportTransform = false
  Suppressed = false
  UseAllEdges = false
FEATURE [PartDesign::Pocket] Pocket011
  BaseFeature = -> Fillet008
  Direction = (0,1,-2e-16)
  Length = 0.8
  Length2 = 5
  Profile = -> Sketch132
  ReferenceAxis = -> Sketch132 [N_Axis]
  Refine = true
  Suppressed = false
  Type = 0
FEATURE [PartDesign::Pocket] Pocket012
  BaseFeature = -> Pocket011
  Direction = (0,1,0)
  Length = 1
  Length2 = 5
  Profile = -> ShapeString
  ReferenceAxis = -> ShapeString [N_Axis]
  Refine = true
  Suppressed = false
  Type = 0
FEATURE [PartDesign::Body] Body007  label="lato DX"
  AllowCompound = false
  Group = -> [Binder001,Sketch114,Pad011,Chamfer014,Sketch115,Pocket006,Sketch116,Pad012,Sketch117,Pocket007,Sketch118,Pad013,Sketch119,Pocket008,Pad017,Chamfer009,Pocket009,Sketch123,Sketch120,Pad014,Pad018,Chamfer008,Pocket010,Sketch121,Pad015,Sketch122,Pad016,SubtractivePipe004,SubtractivePipe005,Sketch149,Sketch148,Sketch124,Sketch125,Sketch126,Sketch129,Sketch130,Clone2D001,Sketch131,SubtractiveLoft002,+11 more]
  Origin = -> Origin007
  Tip = -> Pocket012
FEATURE [Sketcher::SketchObject] Sketch150
  ArcFitTolerance = 1e-06
  AttachmentSupport = -> [Pad008]
  ExternalGeometry = -> [Pad008]
  FullyConstrained = true
  MakeInternals = false
  MapMode = 5
  Placement = pos=(0,3.6,0) rot=(0,0.707107,0.707107;3.14159rad)
  sketch-geometry (7):
    g0: LineSegment [constr] StartX=211.043 StartY=-66.0316 StartZ=0 EndX=211.043 EndY=-72.8316 EndZ=0
    g1: LineSegment [constr] StartX=211.043 StartY=-72.8316 StartZ=0 EndX=217.243 EndY=-72.8316 EndZ=0
    g2: LineSegment [constr] StartX=217.243 StartY=-72.8316 StartZ=0 EndX=217.243 EndY=-66.0316 EndZ=0
    g3: LineSegment [constr] StartX=217.243 StartY=-66.0316 StartZ=0 EndX=211.043 EndY=-66.0316 EndZ=0
    g4: LineSegment [constr] StartX=211.043 StartY=-72.8316 StartZ=0 EndX=217.243 EndY=-66.0316 EndZ=0
    g5: LineSegment [constr] StartX=211.043 StartY=-66.0316 StartZ=0 EndX=214.143 EndY=-69.4316 EndZ=0
    g6: Circle CenterX=214.143 CenterY=-69.4316 CenterZ=0 NormalX=0 NormalY=0 NormalZ=1 AngleXU=0 Radius=2
  constraints (18):
    c: Coincident(g0,g1)
    c: Coincident(g1,g2)
    c: Coincident(g2,g3)
    c: Coincident(g3,g0)
    c: Vertical(g0)
    c: Vertical(g2)
    c: Horizontal(g1)
    c: Horizontal(g3)
    c: Distance(g0,g2) = 6.2
    c: Distance(g1,g3) = 6.8
    c: DistanceY(g-3,g1) = 4
    c: DistanceX(g-3,g1) = 3.8
    c: Coincident(g4,g0)
    c: Coincident(g4,g2)
    c: Coincident(g5,g0)
    c: Symmetric(g0,g2,g5)
    c: Diameter(g6) = 4
    c: Coincident(g6,g5)
FEATURE [PartDesign::Pocket] Pocket018
  BaseFeature = -> Pocket013
  Direction = (0,-1,2e-16)
  Length = 3.6
  Length2 = 5
  Profile = -> Sketch150
  ReferenceAxis = -> Sketch150 [N_Axis]
  Refine = true
  Suppressed = false
  Type = 0
FEATURE [Sketcher::SketchObject] Sketch151
  ArcFitTolerance = 1e-06
  AttachmentSupport = -> [Pad008]
  ExternalGeometry = -> [Pad008]
  FullyConstrained = true
  MakeInternals = false
  MapMode = 5
  Placement = pos=(0,3.6,0) rot=(0,0.707107,0.707107;3.14159rad)
  sketch-geometry (10):
    g0: LineSegment [constr] StartX=211.343 StartY=-56.1316 StartZ=0 EndX=211.343 EndY=-65.3316 EndZ=0
    g1: LineSegment [constr] StartX=211.343 StartY=-65.3316 StartZ=0 EndX=215.943 EndY=-65.3316 EndZ=0
    g2: LineSegment [constr] StartX=215.943 StartY=-65.3316 StartZ=0 EndX=215.943 EndY=-56.1316 EndZ=0
    g3: LineSegment [constr] StartX=215.943 StartY=-56.1316 StartZ=0 EndX=211.343 EndY=-56.1316 EndZ=0
    g4: LineSegment StartX=212.443 StartY=-62.9316 StartZ=0 EndX=214.843 EndY=-62.9316 EndZ=0
    g5: LineSegment StartX=214.843 StartY=-62.9316 StartZ=0 EndX=214.843 EndY=-56.5316 EndZ=0
    g6: LineSegment StartX=214.843 StartY=-56.5316 StartZ=0 EndX=212.443 EndY=-56.5316 EndZ=0
    g7: LineSegment StartX=212.443 StartY=-56.5316 StartZ=0 EndX=212.443 EndY=-62.9316 EndZ=0
    g8: GeomPoint [constr] X=213.643 Y=-59.7316 Z=0
    g9: GeomPoint [constr] X=213.643 Y=-60.7316 Z=0
  constraints (26):
    c: Coincident(g0,g1)
    c: Coincident(g1,g2)
    c: Coincident(g2,g3)
    c: Coincident(g3,g0)
    c: Vertical(g0)
    c: Vertical(g2)
    c: Horizontal(g1)
    c: Horizontal(g3)
    c: Distance(g0,g2) = 4.6
    c: Distance(g1,g3) = 9.2
    c: DistanceY(g-3,g1) = 11.5
    c: DistanceX(g-3,g1) = 2.5
    c: Coincident(g4,g5)
    c: Coincident(g5,g6)
    c: Coincident(g6,g7)
    c: Coincident(g7,g4)
    c: Horizontal(g4)
    c: Horizontal(g6)
    c: Vertical(g5)
    c: Vertical(g7)
    c: Symmetric(g6,g4,g8)
    c: Distance(g5,g7) = 2.4
    c: Distance(g4,g6) = 6.4
    c: Symmetric(g2,g0,g9)
    c: Vertical(g8,g9)
    c: DistanceY(g1,g4) = 2.4
FEATURE [PartDesign::Pocket] Pocket019
  BaseFeature = -> Pocket018
  Direction = (0,-1,2e-16)
  Length = 3.6
  Length2 = 5
  Profile = -> Sketch151
  ReferenceAxis = -> Sketch151 [N_Axis]
  Refine = true
  Suppressed = false
  Type = 0
FEATURE [PartDesign::Body] Body006  label="lato SX"
  AllowCompound = false
  Group = -> [Binder,Pad019,Chamfer015,Pocket002,Sketch133,Sketch091,Pad005,Sketch092,Pocket001,Sketch093,Sketch094,Pad006,Sketch095,Pad007,Sketch096,Pad008,Sketch097,Pad009,Chamfer005,Pocket004,Sketch098,Pad010,Chamfer006,Pocket003,SubtractivePipe,SubtractivePipe001,Sketch099,Sketch106,Sketch107,Sketch108,Clone2D,Sketch109,SubtractiveLoft,SubtractiveLoft001,Sketch110,Sketch111,Sketch112,Chamfer016,Chamfer017,+11 more]
  Origin = -> Origin006
  Tip = -> Pocket019
note: 2 file-system paths scrubbed to <path> (originals preserved in the JSON sidecar)
